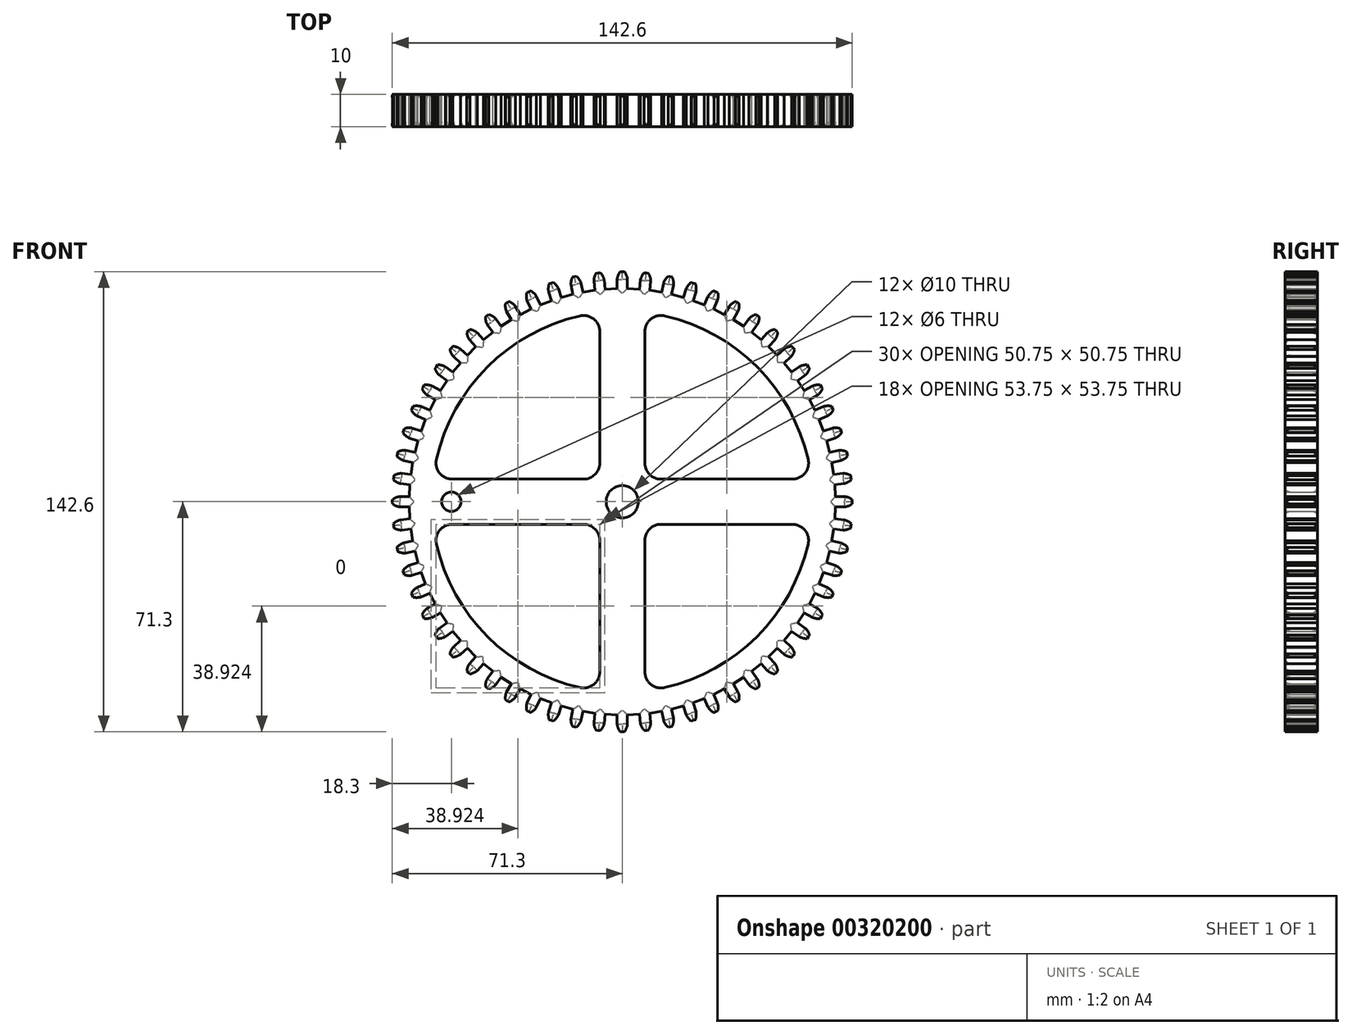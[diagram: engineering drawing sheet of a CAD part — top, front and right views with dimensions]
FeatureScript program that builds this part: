
annotation { "Feature Type Name" : "Feature", "Feature Type Description" : "" }
export const myFeature = defineFeature(function(context is Context, id is Id, definition is map)
    precondition{}
    {
        {
            var Q0;
            Q0=qCreatedBy(makeId("Front.planeOp"),FACE);
            var sketch = newSketch(context, id + "F0", { "sketchPlane" : qUnion([Q0])});
            skCircle(sketch, "E0", {"center": v(0, 0) * mm, "radius": 5 * mm});
            skLineSegment(sketch, "E1", {"start": v(1.6, 66.08) * mm, "end": v(1.6, 68.99) * mm});
            skArc(sketch, "E2", {"start": v(1.6, 67.83) * mm, "mid": v(1.47, 69.66) * mm, "end": v(0.66, 71.3) * mm});
            skLineSegment(sketch, "E3", {"start": v(0, 71.3) * mm, "end": v(0.66, 71.3) * mm});
            skLineSegment(sketch, "E4.MirrorCS", {"start": v(0, 71.3) * mm, "end": v(-0.66, 71.3) * mm});
            skArc(sketch, "E5.MirrorCS", {"start": v(-1.6, 67.83) * mm, "mid": v(-1.47, 69.66) * mm, "end": v(-0.66, 71.3) * mm});
            skLineSegment(sketch, "E6.MirrorCS", {"start": v(-1.6, 66.08) * mm, "end": v(-1.6, 68.99) * mm});
            skLineSegment(sketch, "E7.1.0", {"start": v(-8.5, 65.55) * mm, "end": v(-8.8, 68.44) * mm});
            skArc(sketch, "E7.1.1", {"start": v(-8.68, 67.3) * mm, "mid": v(-8.74, 69.12) * mm, "end": v(-8.1, 70.84) * mm});
            skLineSegment(sketch, "E7.1.2", {"start": v(-7.45, 70.9) * mm, "end": v(-8.1, 70.84) * mm});
            skLineSegment(sketch, "E7.1.3", {"start": v(-7.45, 70.9) * mm, "end": v(-6.8, 70.98) * mm});
            skArc(sketch, "E7.1.4", {"start": v(-5.5, 67.63) * mm, "mid": v(-5.82, 69.43) * mm, "end": v(-6.8, 70.98) * mm});
            skLineSegment(sketch, "E7.1.5", {"start": v(-5.32, 65.89) * mm, "end": v(-5.62, 68.78) * mm});
            skLineSegment(sketch, "E7.2.0", {"start": v(-15.3, 64.3) * mm, "end": v(-15.9, 67.15) * mm});
            skArc(sketch, "E7.2.1", {"start": v(-15.67, 66.02) * mm, "mid": v(-15.92, 67.83) * mm, "end": v(-15.47, 69.6) * mm});
            skLineSegment(sketch, "E7.2.2", {"start": v(-14.82, 69.74) * mm, "end": v(-15.47, 69.6) * mm});
            skLineSegment(sketch, "E7.2.3", {"start": v(-14.82, 69.74) * mm, "end": v(-14.18, 69.88) * mm});
            skArc(sketch, "E7.2.4", {"start": v(-12.54, 66.68) * mm, "mid": v(-13.05, 68.44) * mm, "end": v(-14.18, 69.88) * mm});
            skLineSegment(sketch, "E7.2.5", {"start": v(-12.17, 64.97) * mm, "end": v(-12.78, 67.81) * mm});
            skLineSegment(sketch, "E7.3.0", {"start": v(-21.94, 62.35) * mm, "end": v(-22.84, 65.12) * mm});
            skArc(sketch, "E7.3.1", {"start": v(-22.48, 64.02) * mm, "mid": v(-22.92, 65.8) * mm, "end": v(-22.66, 67.6) * mm});
            skLineSegment(sketch, "E7.3.2", {"start": v(-22.03, 67.81) * mm, "end": v(-22.66, 67.6) * mm});
            skLineSegment(sketch, "E7.3.3", {"start": v(-22.03, 67.81) * mm, "end": v(-21.4, 68.01) * mm});
            skArc(sketch, "E7.3.4", {"start": v(-19.44, 65) * mm, "mid": v(-20.13, 66.7) * mm, "end": v(-21.4, 68.01) * mm});
            skLineSegment(sketch, "E7.3.5", {"start": v(-18.9, 63.34) * mm, "end": v(-19.8, 66.1) * mm});
            skLineSegment(sketch, "E7.4.0", {"start": v(-28.34, 59.72) * mm, "end": v(-29.52, 62.37) * mm});
            skArc(sketch, "E7.4.1", {"start": v(-29.05, 61.32) * mm, "mid": v(-29.67, 63.04) * mm, "end": v(-29.6, 64.87) * mm});
            skLineSegment(sketch, "E7.4.2", {"start": v(-29, 65.14) * mm, "end": v(-29.6, 64.87) * mm});
            skLineSegment(sketch, "E7.4.3", {"start": v(-29, 65.14) * mm, "end": v(-28.4, 65.4) * mm});
            skArc(sketch, "E7.4.4", {"start": v(-26.13, 62.62) * mm, "mid": v(-26.99, 64.23) * mm, "end": v(-28.4, 65.4) * mm});
            skLineSegment(sketch, "E7.4.5", {"start": v(-25.42, 61.02) * mm, "end": v(-26.6, 63.68) * mm});
            skLineSegment(sketch, "E7.5.0", {"start": v(-34.43, 56.43) * mm, "end": v(-35.88, 58.95) * mm});
            skArc(sketch, "E7.5.1", {"start": v(-35.3, 57.94) * mm, "mid": v(-36.1, 59.59) * mm, "end": v(-36.22, 61.42) * mm});
            skLineSegment(sketch, "E7.5.2", {"start": v(-35.65, 61.75) * mm, "end": v(-36.22, 61.42) * mm});
            skLineSegment(sketch, "E7.5.3", {"start": v(-35.65, 61.75) * mm, "end": v(-35.08, 62.07) * mm});
            skArc(sketch, "E7.5.4", {"start": v(-32.53, 59.54) * mm, "mid": v(-33.56, 61.06) * mm, "end": v(-35.08, 62.07) * mm});
            skLineSegment(sketch, "E7.5.5", {"start": v(-31.65, 58.03) * mm, "end": v(-33.1, 60.55) * mm});
            skLineSegment(sketch, "E7.6.0", {"start": v(-40.14, 52.52) * mm, "end": v(-41.85, 54.87) * mm});
            skArc(sketch, "E7.6.1", {"start": v(-41.16, 53.94) * mm, "mid": v(-42.13, 55.49) * mm, "end": v(-42.44, 57.3) * mm});
            skLineSegment(sketch, "E7.6.2", {"start": v(-41.9, 57.68) * mm, "end": v(-42.44, 57.3) * mm});
            skLineSegment(sketch, "E7.6.3", {"start": v(-41.9, 57.68) * mm, "end": v(-41.38, 58.07) * mm});
            skArc(sketch, "E7.6.4", {"start": v(-38.58, 55.82) * mm, "mid": v(-39.75, 57.22) * mm, "end": v(-41.38, 58.07) * mm});
            skLineSegment(sketch, "E7.6.5", {"start": v(-37.55, 54.4) * mm, "end": v(-39.26, 56.75) * mm});
            skLineSegment(sketch, "E7.7.0", {"start": v(-45.4, 48.04) * mm, "end": v(-47.35, 50.2) * mm});
            skArc(sketch, "E7.7.1", {"start": v(-46.58, 49.34) * mm, "mid": v(-47.7, 50.78) * mm, "end": v(-48.2, 52.54) * mm});
            skLineSegment(sketch, "E7.7.2", {"start": v(-47.7, 52.99) * mm, "end": v(-48.2, 52.54) * mm});
            skLineSegment(sketch, "E7.7.3", {"start": v(-47.7, 52.99) * mm, "end": v(-47.22, 53.42) * mm});
            skArc(sketch, "E7.7.4", {"start": v(-44.2, 51.48) * mm, "mid": v(-45.52, 52.75) * mm, "end": v(-47.22, 53.42) * mm});
            skLineSegment(sketch, "E7.7.5", {"start": v(-43.03, 50.18) * mm, "end": v(-44.97, 52.34) * mm});
            skLineSegment(sketch, "E7.8.0", {"start": v(-50.18, 43.03) * mm, "end": v(-52.34, 44.97) * mm});
            skArc(sketch, "E7.8.1", {"start": v(-51.48, 44.2) * mm, "mid": v(-52.75, 45.52) * mm, "end": v(-53.42, 47.22) * mm});
            skLineSegment(sketch, "E7.8.2", {"start": v(-52.99, 47.7) * mm, "end": v(-53.42, 47.22) * mm});
            skLineSegment(sketch, "E7.8.3", {"start": v(-52.99, 47.7) * mm, "end": v(-52.54, 48.2) * mm});
            skArc(sketch, "E7.8.4", {"start": v(-49.34, 46.58) * mm, "mid": v(-50.78, 47.7) * mm, "end": v(-52.54, 48.2) * mm});
            skLineSegment(sketch, "E7.8.5", {"start": v(-48.04, 45.4) * mm, "end": v(-50.2, 47.35) * mm});
            skLineSegment(sketch, "E7.9.0", {"start": v(-54.4, 37.55) * mm, "end": v(-56.75, 39.26) * mm});
            skArc(sketch, "E7.9.1", {"start": v(-55.82, 38.58) * mm, "mid": v(-57.22, 39.75) * mm, "end": v(-58.07, 41.38) * mm});
            skLineSegment(sketch, "E7.9.2", {"start": v(-57.68, 41.9) * mm, "end": v(-58.07, 41.38) * mm});
            skLineSegment(sketch, "E7.9.3", {"start": v(-57.68, 41.9) * mm, "end": v(-57.3, 42.44) * mm});
            skArc(sketch, "E7.9.4", {"start": v(-53.94, 41.16) * mm, "mid": v(-55.49, 42.13) * mm, "end": v(-57.3, 42.44) * mm});
            skLineSegment(sketch, "E7.9.5", {"start": v(-52.52, 40.14) * mm, "end": v(-54.87, 41.85) * mm});
            skLineSegment(sketch, "E7.10.0", {"start": v(-58.03, 31.65) * mm, "end": v(-60.55, 33.1) * mm});
            skArc(sketch, "E7.10.1", {"start": v(-59.54, 32.53) * mm, "mid": v(-61.06, 33.56) * mm, "end": v(-62.07, 35.08) * mm});
            skLineSegment(sketch, "E7.10.2", {"start": v(-61.75, 35.65) * mm, "end": v(-62.07, 35.08) * mm});
            skLineSegment(sketch, "E7.10.3", {"start": v(-61.75, 35.65) * mm, "end": v(-61.42, 36.22) * mm});
            skArc(sketch, "E7.10.4", {"start": v(-57.94, 35.3) * mm, "mid": v(-59.59, 36.1) * mm, "end": v(-61.42, 36.22) * mm});
            skLineSegment(sketch, "E7.10.5", {"start": v(-56.43, 34.43) * mm, "end": v(-58.95, 35.88) * mm});
            skLineSegment(sketch, "E7.11.0", {"start": v(-61.02, 25.42) * mm, "end": v(-63.68, 26.6) * mm});
            skArc(sketch, "E7.11.1", {"start": v(-62.62, 26.13) * mm, "mid": v(-64.23, 26.99) * mm, "end": v(-65.4, 28.4) * mm});
            skLineSegment(sketch, "E7.11.2", {"start": v(-65.14, 29) * mm, "end": v(-65.4, 28.4) * mm});
            skLineSegment(sketch, "E7.11.3", {"start": v(-65.14, 29) * mm, "end": v(-64.87, 29.6) * mm});
            skArc(sketch, "E7.11.4", {"start": v(-61.32, 29.05) * mm, "mid": v(-63.04, 29.67) * mm, "end": v(-64.87, 29.6) * mm});
            skLineSegment(sketch, "E7.11.5", {"start": v(-59.72, 28.34) * mm, "end": v(-62.37, 29.52) * mm});
            skLineSegment(sketch, "E7.12.0", {"start": v(-63.34, 18.9) * mm, "end": v(-66.1, 19.8) * mm});
            skArc(sketch, "E7.12.1", {"start": v(-65, 19.44) * mm, "mid": v(-66.7, 20.13) * mm, "end": v(-68.01, 21.4) * mm});
            skLineSegment(sketch, "E7.12.2", {"start": v(-67.81, 22.03) * mm, "end": v(-68.01, 21.4) * mm});
            skLineSegment(sketch, "E7.12.3", {"start": v(-67.81, 22.03) * mm, "end": v(-67.6, 22.66) * mm});
            skArc(sketch, "E7.12.4", {"start": v(-64.02, 22.48) * mm, "mid": v(-65.8, 22.92) * mm, "end": v(-67.6, 22.66) * mm});
            skLineSegment(sketch, "E7.12.5", {"start": v(-62.35, 21.94) * mm, "end": v(-65.12, 22.84) * mm});
            skLineSegment(sketch, "E7.13.0", {"start": v(-64.97, 12.17) * mm, "end": v(-67.81, 12.78) * mm});
            skArc(sketch, "E7.13.1", {"start": v(-66.68, 12.54) * mm, "mid": v(-68.44, 13.05) * mm, "end": v(-69.88, 14.18) * mm});
            skLineSegment(sketch, "E7.13.2", {"start": v(-69.74, 14.82) * mm, "end": v(-69.88, 14.18) * mm});
            skLineSegment(sketch, "E7.13.3", {"start": v(-69.74, 14.82) * mm, "end": v(-69.6, 15.47) * mm});
            skArc(sketch, "E7.13.4", {"start": v(-66.02, 15.67) * mm, "mid": v(-67.83, 15.92) * mm, "end": v(-69.6, 15.47) * mm});
            skLineSegment(sketch, "E7.13.5", {"start": v(-64.3, 15.3) * mm, "end": v(-67.15, 15.9) * mm});
            skLineSegment(sketch, "E7.14.0", {"start": v(-65.89, 5.32) * mm, "end": v(-68.78, 5.62) * mm});
            skArc(sketch, "E7.14.1", {"start": v(-67.63, 5.5) * mm, "mid": v(-69.43, 5.82) * mm, "end": v(-70.98, 6.8) * mm});
            skLineSegment(sketch, "E7.14.2", {"start": v(-70.9, 7.45) * mm, "end": v(-70.98, 6.8) * mm});
            skLineSegment(sketch, "E7.14.3", {"start": v(-70.9, 7.45) * mm, "end": v(-70.84, 8.1) * mm});
            skArc(sketch, "E7.14.4", {"start": v(-67.3, 8.68) * mm, "mid": v(-69.12, 8.74) * mm, "end": v(-70.84, 8.1) * mm});
            skLineSegment(sketch, "E7.14.5", {"start": v(-65.55, 8.5) * mm, "end": v(-68.44, 8.8) * mm});
            skLineSegment(sketch, "E7.15.0", {"start": v(-66.08, -1.6) * mm, "end": v(-68.99, -1.6) * mm});
            skArc(sketch, "E7.15.1", {"start": v(-67.83, -1.6) * mm, "mid": v(-69.66, -1.47) * mm, "end": v(-71.3, -0.66) * mm});
            skLineSegment(sketch, "E7.15.2", {"start": v(-71.3, 0) * mm, "end": v(-71.3, -0.66) * mm});
            skLineSegment(sketch, "E7.15.3", {"start": v(-71.3, 0) * mm, "end": v(-71.3, 0.66) * mm});
            skArc(sketch, "E7.15.4", {"start": v(-67.83, 1.6) * mm, "mid": v(-69.66, 1.47) * mm, "end": v(-71.3, 0.66) * mm});
            skLineSegment(sketch, "E7.15.5", {"start": v(-66.08, 1.6) * mm, "end": v(-68.99, 1.6) * mm});
            skLineSegment(sketch, "E7.16.0", {"start": v(-65.55, -8.5) * mm, "end": v(-68.44, -8.8) * mm});
            skArc(sketch, "E7.16.1", {"start": v(-67.3, -8.68) * mm, "mid": v(-69.12, -8.74) * mm, "end": v(-70.84, -8.1) * mm});
            skLineSegment(sketch, "E7.16.2", {"start": v(-70.9, -7.45) * mm, "end": v(-70.84, -8.1) * mm});
            skLineSegment(sketch, "E7.16.3", {"start": v(-70.9, -7.45) * mm, "end": v(-70.98, -6.8) * mm});
            skArc(sketch, "E7.16.4", {"start": v(-67.63, -5.5) * mm, "mid": v(-69.43, -5.82) * mm, "end": v(-70.98, -6.8) * mm});
            skLineSegment(sketch, "E7.16.5", {"start": v(-65.89, -5.32) * mm, "end": v(-68.78, -5.62) * mm});
            skLineSegment(sketch, "E7.17.0", {"start": v(-64.3, -15.3) * mm, "end": v(-67.15, -15.9) * mm});
            skArc(sketch, "E7.17.1", {"start": v(-66.02, -15.67) * mm, "mid": v(-67.83, -15.92) * mm, "end": v(-69.6, -15.47) * mm});
            skLineSegment(sketch, "E7.17.2", {"start": v(-69.74, -14.82) * mm, "end": v(-69.6, -15.47) * mm});
            skLineSegment(sketch, "E7.17.3", {"start": v(-69.74, -14.82) * mm, "end": v(-69.88, -14.18) * mm});
            skArc(sketch, "E7.17.4", {"start": v(-66.68, -12.54) * mm, "mid": v(-68.44, -13.05) * mm, "end": v(-69.88, -14.18) * mm});
            skLineSegment(sketch, "E7.17.5", {"start": v(-64.97, -12.17) * mm, "end": v(-67.81, -12.78) * mm});
            skLineSegment(sketch, "E7.18.0", {"start": v(-62.35, -21.94) * mm, "end": v(-65.12, -22.84) * mm});
            skArc(sketch, "E7.18.1", {"start": v(-64.02, -22.48) * mm, "mid": v(-65.8, -22.92) * mm, "end": v(-67.6, -22.66) * mm});
            skLineSegment(sketch, "E7.18.2", {"start": v(-67.81, -22.03) * mm, "end": v(-67.6, -22.66) * mm});
            skLineSegment(sketch, "E7.18.3", {"start": v(-67.81, -22.03) * mm, "end": v(-68.01, -21.4) * mm});
            skArc(sketch, "E7.18.4", {"start": v(-65, -19.44) * mm, "mid": v(-66.7, -20.13) * mm, "end": v(-68.01, -21.4) * mm});
            skLineSegment(sketch, "E7.18.5", {"start": v(-63.34, -18.9) * mm, "end": v(-66.1, -19.8) * mm});
            skLineSegment(sketch, "E7.19.0", {"start": v(-59.72, -28.34) * mm, "end": v(-62.37, -29.52) * mm});
            skArc(sketch, "E7.19.1", {"start": v(-61.32, -29.05) * mm, "mid": v(-63.04, -29.67) * mm, "end": v(-64.87, -29.6) * mm});
            skLineSegment(sketch, "E7.19.2", {"start": v(-65.14, -29) * mm, "end": v(-64.87, -29.6) * mm});
            skLineSegment(sketch, "E7.19.3", {"start": v(-65.14, -29) * mm, "end": v(-65.4, -28.4) * mm});
            skArc(sketch, "E7.19.4", {"start": v(-62.62, -26.13) * mm, "mid": v(-64.23, -26.99) * mm, "end": v(-65.4, -28.4) * mm});
            skLineSegment(sketch, "E7.19.5", {"start": v(-61.02, -25.42) * mm, "end": v(-63.68, -26.6) * mm});
            skLineSegment(sketch, "E7.20.0", {"start": v(-56.43, -34.43) * mm, "end": v(-58.95, -35.88) * mm});
            skArc(sketch, "E7.20.1", {"start": v(-57.94, -35.3) * mm, "mid": v(-59.59, -36.1) * mm, "end": v(-61.42, -36.22) * mm});
            skLineSegment(sketch, "E7.20.2", {"start": v(-61.75, -35.65) * mm, "end": v(-61.42, -36.22) * mm});
            skLineSegment(sketch, "E7.20.3", {"start": v(-61.75, -35.65) * mm, "end": v(-62.07, -35.08) * mm});
            skArc(sketch, "E7.20.4", {"start": v(-59.54, -32.53) * mm, "mid": v(-61.06, -33.56) * mm, "end": v(-62.07, -35.08) * mm});
            skLineSegment(sketch, "E7.20.5", {"start": v(-58.03, -31.65) * mm, "end": v(-60.55, -33.1) * mm});
            skLineSegment(sketch, "E7.21.0", {"start": v(-52.52, -40.14) * mm, "end": v(-54.87, -41.85) * mm});
            skArc(sketch, "E7.21.1", {"start": v(-53.94, -41.16) * mm, "mid": v(-55.49, -42.13) * mm, "end": v(-57.3, -42.44) * mm});
            skLineSegment(sketch, "E7.21.2", {"start": v(-57.68, -41.9) * mm, "end": v(-57.3, -42.44) * mm});
            skLineSegment(sketch, "E7.21.3", {"start": v(-57.68, -41.9) * mm, "end": v(-58.07, -41.38) * mm});
            skArc(sketch, "E7.21.4", {"start": v(-55.82, -38.58) * mm, "mid": v(-57.22, -39.75) * mm, "end": v(-58.07, -41.38) * mm});
            skLineSegment(sketch, "E7.21.5", {"start": v(-54.4, -37.55) * mm, "end": v(-56.75, -39.26) * mm});
            skLineSegment(sketch, "E7.22.0", {"start": v(-48.04, -45.4) * mm, "end": v(-50.2, -47.35) * mm});
            skArc(sketch, "E7.22.1", {"start": v(-49.34, -46.58) * mm, "mid": v(-50.78, -47.7) * mm, "end": v(-52.54, -48.2) * mm});
            skLineSegment(sketch, "E7.22.2", {"start": v(-52.99, -47.7) * mm, "end": v(-52.54, -48.2) * mm});
            skLineSegment(sketch, "E7.22.3", {"start": v(-52.99, -47.7) * mm, "end": v(-53.42, -47.22) * mm});
            skArc(sketch, "E7.22.4", {"start": v(-51.48, -44.2) * mm, "mid": v(-52.75, -45.52) * mm, "end": v(-53.42, -47.22) * mm});
            skLineSegment(sketch, "E7.22.5", {"start": v(-50.18, -43.03) * mm, "end": v(-52.34, -44.97) * mm});
            skLineSegment(sketch, "E7.23.0", {"start": v(-43.03, -50.18) * mm, "end": v(-44.97, -52.34) * mm});
            skArc(sketch, "E7.23.1", {"start": v(-44.2, -51.48) * mm, "mid": v(-45.52, -52.75) * mm, "end": v(-47.22, -53.42) * mm});
            skLineSegment(sketch, "E7.23.2", {"start": v(-47.7, -52.99) * mm, "end": v(-47.22, -53.42) * mm});
            skLineSegment(sketch, "E7.23.3", {"start": v(-47.7, -52.99) * mm, "end": v(-48.2, -52.54) * mm});
            skArc(sketch, "E7.23.4", {"start": v(-46.58, -49.34) * mm, "mid": v(-47.7, -50.78) * mm, "end": v(-48.2, -52.54) * mm});
            skLineSegment(sketch, "E7.23.5", {"start": v(-45.4, -48.04) * mm, "end": v(-47.35, -50.2) * mm});
            skLineSegment(sketch, "E7.24.0", {"start": v(-37.55, -54.4) * mm, "end": v(-39.26, -56.75) * mm});
            skArc(sketch, "E7.24.1", {"start": v(-38.58, -55.82) * mm, "mid": v(-39.75, -57.22) * mm, "end": v(-41.38, -58.07) * mm});
            skLineSegment(sketch, "E7.24.2", {"start": v(-41.9, -57.68) * mm, "end": v(-41.38, -58.07) * mm});
            skLineSegment(sketch, "E7.24.3", {"start": v(-41.9, -57.68) * mm, "end": v(-42.44, -57.3) * mm});
            skArc(sketch, "E7.24.4", {"start": v(-41.16, -53.94) * mm, "mid": v(-42.13, -55.49) * mm, "end": v(-42.44, -57.3) * mm});
            skLineSegment(sketch, "E7.24.5", {"start": v(-40.14, -52.52) * mm, "end": v(-41.85, -54.87) * mm});
            skLineSegment(sketch, "E7.25.0", {"start": v(-31.65, -58.03) * mm, "end": v(-33.1, -60.55) * mm});
            skArc(sketch, "E7.25.1", {"start": v(-32.53, -59.54) * mm, "mid": v(-33.56, -61.06) * mm, "end": v(-35.08, -62.07) * mm});
            skLineSegment(sketch, "E7.25.2", {"start": v(-35.65, -61.75) * mm, "end": v(-35.08, -62.07) * mm});
            skLineSegment(sketch, "E7.25.3", {"start": v(-35.65, -61.75) * mm, "end": v(-36.22, -61.42) * mm});
            skArc(sketch, "E7.25.4", {"start": v(-35.3, -57.94) * mm, "mid": v(-36.1, -59.59) * mm, "end": v(-36.22, -61.42) * mm});
            skLineSegment(sketch, "E7.25.5", {"start": v(-34.43, -56.43) * mm, "end": v(-35.88, -58.95) * mm});
            skLineSegment(sketch, "E7.26.0", {"start": v(-25.42, -61.02) * mm, "end": v(-26.6, -63.68) * mm});
            skArc(sketch, "E7.26.1", {"start": v(-26.13, -62.62) * mm, "mid": v(-26.99, -64.23) * mm, "end": v(-28.4, -65.4) * mm});
            skLineSegment(sketch, "E7.26.2", {"start": v(-29, -65.14) * mm, "end": v(-28.4, -65.4) * mm});
            skLineSegment(sketch, "E7.26.3", {"start": v(-29, -65.14) * mm, "end": v(-29.6, -64.87) * mm});
            skArc(sketch, "E7.26.4", {"start": v(-29.05, -61.32) * mm, "mid": v(-29.67, -63.04) * mm, "end": v(-29.6, -64.87) * mm});
            skLineSegment(sketch, "E7.26.5", {"start": v(-28.34, -59.72) * mm, "end": v(-29.52, -62.37) * mm});
            skLineSegment(sketch, "E7.27.0", {"start": v(-18.9, -63.34) * mm, "end": v(-19.8, -66.1) * mm});
            skArc(sketch, "E7.27.1", {"start": v(-19.44, -65) * mm, "mid": v(-20.13, -66.7) * mm, "end": v(-21.4, -68.01) * mm});
            skLineSegment(sketch, "E7.27.2", {"start": v(-22.03, -67.81) * mm, "end": v(-21.4, -68.01) * mm});
            skLineSegment(sketch, "E7.27.3", {"start": v(-22.03, -67.81) * mm, "end": v(-22.66, -67.6) * mm});
            skArc(sketch, "E7.27.4", {"start": v(-22.48, -64.02) * mm, "mid": v(-22.92, -65.8) * mm, "end": v(-22.66, -67.6) * mm});
            skLineSegment(sketch, "E7.27.5", {"start": v(-21.94, -62.35) * mm, "end": v(-22.84, -65.12) * mm});
            skLineSegment(sketch, "E7.28.0", {"start": v(-12.17, -64.97) * mm, "end": v(-12.78, -67.81) * mm});
            skArc(sketch, "E7.28.1", {"start": v(-12.54, -66.68) * mm, "mid": v(-13.05, -68.44) * mm, "end": v(-14.18, -69.88) * mm});
            skLineSegment(sketch, "E7.28.2", {"start": v(-14.82, -69.74) * mm, "end": v(-14.18, -69.88) * mm});
            skLineSegment(sketch, "E7.28.3", {"start": v(-14.82, -69.74) * mm, "end": v(-15.47, -69.6) * mm});
            skArc(sketch, "E7.28.4", {"start": v(-15.67, -66.02) * mm, "mid": v(-15.92, -67.83) * mm, "end": v(-15.47, -69.6) * mm});
            skLineSegment(sketch, "E7.28.5", {"start": v(-15.3, -64.3) * mm, "end": v(-15.9, -67.15) * mm});
            skLineSegment(sketch, "E7.29.0", {"start": v(-5.32, -65.89) * mm, "end": v(-5.62, -68.78) * mm});
            skArc(sketch, "E7.29.1", {"start": v(-5.5, -67.63) * mm, "mid": v(-5.82, -69.43) * mm, "end": v(-6.8, -70.98) * mm});
            skLineSegment(sketch, "E7.29.2", {"start": v(-7.45, -70.9) * mm, "end": v(-6.8, -70.98) * mm});
            skLineSegment(sketch, "E7.29.3", {"start": v(-7.45, -70.9) * mm, "end": v(-8.1, -70.84) * mm});
            skArc(sketch, "E7.29.4", {"start": v(-8.68, -67.3) * mm, "mid": v(-8.74, -69.12) * mm, "end": v(-8.1, -70.84) * mm});
            skLineSegment(sketch, "E7.29.5", {"start": v(-8.5, -65.55) * mm, "end": v(-8.8, -68.44) * mm});
            skLineSegment(sketch, "E7.30.0", {"start": v(1.6, -66.08) * mm, "end": v(1.6, -68.99) * mm});
            skArc(sketch, "E7.30.1", {"start": v(1.6, -67.83) * mm, "mid": v(1.47, -69.66) * mm, "end": v(0.66, -71.3) * mm});
            skLineSegment(sketch, "E7.30.2", {"start": v(0, -71.3) * mm, "end": v(0.66, -71.3) * mm});
            skLineSegment(sketch, "E7.30.3", {"start": v(0, -71.3) * mm, "end": v(-0.66, -71.3) * mm});
            skArc(sketch, "E7.30.4", {"start": v(-1.6, -67.83) * mm, "mid": v(-1.47, -69.66) * mm, "end": v(-0.66, -71.3) * mm});
            skLineSegment(sketch, "E7.30.5", {"start": v(-1.6, -66.08) * mm, "end": v(-1.6, -68.99) * mm});
            skLineSegment(sketch, "E7.31.0", {"start": v(8.5, -65.55) * mm, "end": v(8.8, -68.44) * mm});
            skArc(sketch, "E7.31.1", {"start": v(8.68, -67.3) * mm, "mid": v(8.74, -69.12) * mm, "end": v(8.1, -70.84) * mm});
            skLineSegment(sketch, "E7.31.2", {"start": v(7.45, -70.9) * mm, "end": v(8.1, -70.84) * mm});
            skLineSegment(sketch, "E7.31.3", {"start": v(7.45, -70.9) * mm, "end": v(6.8, -70.98) * mm});
            skArc(sketch, "E7.31.4", {"start": v(5.5, -67.63) * mm, "mid": v(5.82, -69.43) * mm, "end": v(6.8, -70.98) * mm});
            skLineSegment(sketch, "E7.31.5", {"start": v(5.32, -65.89) * mm, "end": v(5.62, -68.78) * mm});
            skLineSegment(sketch, "E7.32.0", {"start": v(15.3, -64.3) * mm, "end": v(15.9, -67.15) * mm});
            skArc(sketch, "E7.32.1", {"start": v(15.67, -66.02) * mm, "mid": v(15.92, -67.83) * mm, "end": v(15.47, -69.6) * mm});
            skLineSegment(sketch, "E7.32.2", {"start": v(14.82, -69.74) * mm, "end": v(15.47, -69.6) * mm});
            skLineSegment(sketch, "E7.32.3", {"start": v(14.82, -69.74) * mm, "end": v(14.18, -69.88) * mm});
            skArc(sketch, "E7.32.4", {"start": v(12.54, -66.68) * mm, "mid": v(13.05, -68.44) * mm, "end": v(14.18, -69.88) * mm});
            skLineSegment(sketch, "E7.32.5", {"start": v(12.17, -64.97) * mm, "end": v(12.78, -67.81) * mm});
            skLineSegment(sketch, "E7.33.0", {"start": v(21.94, -62.35) * mm, "end": v(22.84, -65.12) * mm});
            skArc(sketch, "E7.33.1", {"start": v(22.48, -64.02) * mm, "mid": v(22.92, -65.8) * mm, "end": v(22.66, -67.6) * mm});
            skLineSegment(sketch, "E7.33.2", {"start": v(22.03, -67.81) * mm, "end": v(22.66, -67.6) * mm});
            skLineSegment(sketch, "E7.33.3", {"start": v(22.03, -67.81) * mm, "end": v(21.4, -68.01) * mm});
            skArc(sketch, "E7.33.4", {"start": v(19.44, -65) * mm, "mid": v(20.13, -66.7) * mm, "end": v(21.4, -68.01) * mm});
            skLineSegment(sketch, "E7.33.5", {"start": v(18.9, -63.34) * mm, "end": v(19.8, -66.1) * mm});
            skLineSegment(sketch, "E7.34.0", {"start": v(28.34, -59.72) * mm, "end": v(29.52, -62.37) * mm});
            skArc(sketch, "E7.34.1", {"start": v(29.05, -61.32) * mm, "mid": v(29.67, -63.04) * mm, "end": v(29.6, -64.87) * mm});
            skLineSegment(sketch, "E7.34.2", {"start": v(29, -65.14) * mm, "end": v(29.6, -64.87) * mm});
            skLineSegment(sketch, "E7.34.3", {"start": v(29, -65.14) * mm, "end": v(28.4, -65.4) * mm});
            skArc(sketch, "E7.34.4", {"start": v(26.13, -62.62) * mm, "mid": v(26.99, -64.23) * mm, "end": v(28.4, -65.4) * mm});
            skLineSegment(sketch, "E7.34.5", {"start": v(25.42, -61.02) * mm, "end": v(26.6, -63.68) * mm});
            skLineSegment(sketch, "E7.35.0", {"start": v(34.43, -56.43) * mm, "end": v(35.88, -58.95) * mm});
            skArc(sketch, "E7.35.1", {"start": v(35.3, -57.94) * mm, "mid": v(36.1, -59.59) * mm, "end": v(36.22, -61.42) * mm});
            skLineSegment(sketch, "E7.35.2", {"start": v(35.65, -61.75) * mm, "end": v(36.22, -61.42) * mm});
            skLineSegment(sketch, "E7.35.3", {"start": v(35.65, -61.75) * mm, "end": v(35.08, -62.07) * mm});
            skArc(sketch, "E7.35.4", {"start": v(32.53, -59.54) * mm, "mid": v(33.56, -61.06) * mm, "end": v(35.08, -62.07) * mm});
            skLineSegment(sketch, "E7.35.5", {"start": v(31.65, -58.03) * mm, "end": v(33.1, -60.55) * mm});
            skLineSegment(sketch, "E7.36.0", {"start": v(40.14, -52.52) * mm, "end": v(41.85, -54.87) * mm});
            skArc(sketch, "E7.36.1", {"start": v(41.16, -53.94) * mm, "mid": v(42.13, -55.49) * mm, "end": v(42.44, -57.3) * mm});
            skLineSegment(sketch, "E7.36.2", {"start": v(41.9, -57.68) * mm, "end": v(42.44, -57.3) * mm});
            skLineSegment(sketch, "E7.36.3", {"start": v(41.9, -57.68) * mm, "end": v(41.38, -58.07) * mm});
            skArc(sketch, "E7.36.4", {"start": v(38.58, -55.82) * mm, "mid": v(39.75, -57.22) * mm, "end": v(41.38, -58.07) * mm});
            skLineSegment(sketch, "E7.36.5", {"start": v(37.55, -54.4) * mm, "end": v(39.26, -56.75) * mm});
            skLineSegment(sketch, "E7.37.0", {"start": v(45.4, -48.04) * mm, "end": v(47.35, -50.2) * mm});
            skArc(sketch, "E7.37.1", {"start": v(46.58, -49.34) * mm, "mid": v(47.7, -50.78) * mm, "end": v(48.2, -52.54) * mm});
            skLineSegment(sketch, "E7.37.2", {"start": v(47.7, -52.99) * mm, "end": v(48.2, -52.54) * mm});
            skLineSegment(sketch, "E7.37.3", {"start": v(47.7, -52.99) * mm, "end": v(47.22, -53.42) * mm});
            skArc(sketch, "E7.37.4", {"start": v(44.2, -51.48) * mm, "mid": v(45.52, -52.75) * mm, "end": v(47.22, -53.42) * mm});
            skLineSegment(sketch, "E7.37.5", {"start": v(43.03, -50.18) * mm, "end": v(44.97, -52.34) * mm});
            skLineSegment(sketch, "E7.38.0", {"start": v(50.18, -43.03) * mm, "end": v(52.34, -44.97) * mm});
            skArc(sketch, "E7.38.1", {"start": v(51.48, -44.2) * mm, "mid": v(52.75, -45.52) * mm, "end": v(53.42, -47.22) * mm});
            skLineSegment(sketch, "E7.38.2", {"start": v(52.99, -47.7) * mm, "end": v(53.42, -47.22) * mm});
            skLineSegment(sketch, "E7.38.3", {"start": v(52.99, -47.7) * mm, "end": v(52.54, -48.2) * mm});
            skArc(sketch, "E7.38.4", {"start": v(49.34, -46.58) * mm, "mid": v(50.78, -47.7) * mm, "end": v(52.54, -48.2) * mm});
            skLineSegment(sketch, "E7.38.5", {"start": v(48.04, -45.4) * mm, "end": v(50.2, -47.35) * mm});
            skLineSegment(sketch, "E7.39.0", {"start": v(54.4, -37.55) * mm, "end": v(56.75, -39.26) * mm});
            skArc(sketch, "E7.39.1", {"start": v(55.82, -38.58) * mm, "mid": v(57.22, -39.75) * mm, "end": v(58.07, -41.38) * mm});
            skLineSegment(sketch, "E7.39.2", {"start": v(57.68, -41.9) * mm, "end": v(58.07, -41.38) * mm});
            skLineSegment(sketch, "E7.39.3", {"start": v(57.68, -41.9) * mm, "end": v(57.3, -42.44) * mm});
            skArc(sketch, "E7.39.4", {"start": v(53.94, -41.16) * mm, "mid": v(55.49, -42.13) * mm, "end": v(57.3, -42.44) * mm});
            skLineSegment(sketch, "E7.39.5", {"start": v(52.52, -40.14) * mm, "end": v(54.87, -41.85) * mm});
            skLineSegment(sketch, "E7.40.0", {"start": v(58.03, -31.65) * mm, "end": v(60.55, -33.1) * mm});
            skArc(sketch, "E7.40.1", {"start": v(59.54, -32.53) * mm, "mid": v(61.06, -33.56) * mm, "end": v(62.07, -35.08) * mm});
            skLineSegment(sketch, "E7.40.2", {"start": v(61.75, -35.65) * mm, "end": v(62.07, -35.08) * mm});
            skLineSegment(sketch, "E7.40.3", {"start": v(61.75, -35.65) * mm, "end": v(61.42, -36.22) * mm});
            skArc(sketch, "E7.40.4", {"start": v(57.94, -35.3) * mm, "mid": v(59.59, -36.1) * mm, "end": v(61.42, -36.22) * mm});
            skLineSegment(sketch, "E7.40.5", {"start": v(56.43, -34.43) * mm, "end": v(58.95, -35.88) * mm});
            skLineSegment(sketch, "E7.41.0", {"start": v(61.02, -25.42) * mm, "end": v(63.68, -26.6) * mm});
            skArc(sketch, "E7.41.1", {"start": v(62.62, -26.13) * mm, "mid": v(64.23, -26.99) * mm, "end": v(65.4, -28.4) * mm});
            skLineSegment(sketch, "E7.41.2", {"start": v(65.14, -29) * mm, "end": v(65.4, -28.4) * mm});
            skLineSegment(sketch, "E7.41.3", {"start": v(65.14, -29) * mm, "end": v(64.87, -29.6) * mm});
            skArc(sketch, "E7.41.4", {"start": v(61.32, -29.05) * mm, "mid": v(63.04, -29.67) * mm, "end": v(64.87, -29.6) * mm});
            skLineSegment(sketch, "E7.41.5", {"start": v(59.72, -28.34) * mm, "end": v(62.37, -29.52) * mm});
            skLineSegment(sketch, "E7.42.0", {"start": v(63.34, -18.9) * mm, "end": v(66.1, -19.8) * mm});
            skArc(sketch, "E7.42.1", {"start": v(65, -19.44) * mm, "mid": v(66.7, -20.13) * mm, "end": v(68.01, -21.4) * mm});
            skLineSegment(sketch, "E7.42.2", {"start": v(67.81, -22.03) * mm, "end": v(68.01, -21.4) * mm});
            skLineSegment(sketch, "E7.42.3", {"start": v(67.81, -22.03) * mm, "end": v(67.6, -22.66) * mm});
            skArc(sketch, "E7.42.4", {"start": v(64.02, -22.48) * mm, "mid": v(65.8, -22.92) * mm, "end": v(67.6, -22.66) * mm});
            skLineSegment(sketch, "E7.42.5", {"start": v(62.35, -21.94) * mm, "end": v(65.12, -22.84) * mm});
            skLineSegment(sketch, "E7.43.0", {"start": v(64.97, -12.17) * mm, "end": v(67.81, -12.78) * mm});
            skArc(sketch, "E7.43.1", {"start": v(66.68, -12.54) * mm, "mid": v(68.44, -13.05) * mm, "end": v(69.88, -14.18) * mm});
            skLineSegment(sketch, "E7.43.2", {"start": v(69.74, -14.82) * mm, "end": v(69.88, -14.18) * mm});
            skLineSegment(sketch, "E7.43.3", {"start": v(69.74, -14.82) * mm, "end": v(69.6, -15.47) * mm});
            skArc(sketch, "E7.43.4", {"start": v(66.02, -15.67) * mm, "mid": v(67.83, -15.92) * mm, "end": v(69.6, -15.47) * mm});
            skLineSegment(sketch, "E7.43.5", {"start": v(64.3, -15.3) * mm, "end": v(67.15, -15.9) * mm});
            skLineSegment(sketch, "E7.44.0", {"start": v(65.89, -5.32) * mm, "end": v(68.78, -5.62) * mm});
            skArc(sketch, "E7.44.1", {"start": v(67.63, -5.5) * mm, "mid": v(69.43, -5.82) * mm, "end": v(70.98, -6.8) * mm});
            skLineSegment(sketch, "E7.44.2", {"start": v(70.9, -7.45) * mm, "end": v(70.98, -6.8) * mm});
            skLineSegment(sketch, "E7.44.3", {"start": v(70.9, -7.45) * mm, "end": v(70.84, -8.1) * mm});
            skArc(sketch, "E7.44.4", {"start": v(67.3, -8.68) * mm, "mid": v(69.12, -8.74) * mm, "end": v(70.84, -8.1) * mm});
            skLineSegment(sketch, "E7.44.5", {"start": v(65.55, -8.5) * mm, "end": v(68.44, -8.8) * mm});
            skLineSegment(sketch, "E7.45.0", {"start": v(66.08, 1.6) * mm, "end": v(68.99, 1.6) * mm});
            skArc(sketch, "E7.45.1", {"start": v(67.83, 1.6) * mm, "mid": v(69.66, 1.47) * mm, "end": v(71.3, 0.66) * mm});
            skLineSegment(sketch, "E7.45.2", {"start": v(71.3, 0) * mm, "end": v(71.3, 0.66) * mm});
            skLineSegment(sketch, "E7.45.3", {"start": v(71.3, 0) * mm, "end": v(71.3, -0.66) * mm});
            skArc(sketch, "E7.45.4", {"start": v(67.83, -1.6) * mm, "mid": v(69.66, -1.47) * mm, "end": v(71.3, -0.66) * mm});
            skLineSegment(sketch, "E7.45.5", {"start": v(66.08, -1.6) * mm, "end": v(68.99, -1.6) * mm});
            skLineSegment(sketch, "E7.46.0", {"start": v(65.55, 8.5) * mm, "end": v(68.44, 8.8) * mm});
            skArc(sketch, "E7.46.1", {"start": v(67.3, 8.68) * mm, "mid": v(69.12, 8.74) * mm, "end": v(70.84, 8.1) * mm});
            skLineSegment(sketch, "E7.46.2", {"start": v(70.9, 7.45) * mm, "end": v(70.84, 8.1) * mm});
            skLineSegment(sketch, "E7.46.3", {"start": v(70.9, 7.45) * mm, "end": v(70.98, 6.8) * mm});
            skArc(sketch, "E7.46.4", {"start": v(67.63, 5.5) * mm, "mid": v(69.43, 5.82) * mm, "end": v(70.98, 6.8) * mm});
            skLineSegment(sketch, "E7.46.5", {"start": v(65.89, 5.32) * mm, "end": v(68.78, 5.62) * mm});
            skLineSegment(sketch, "E7.47.0", {"start": v(64.3, 15.3) * mm, "end": v(67.15, 15.9) * mm});
            skArc(sketch, "E7.47.1", {"start": v(66.02, 15.67) * mm, "mid": v(67.83, 15.92) * mm, "end": v(69.6, 15.47) * mm});
            skLineSegment(sketch, "E7.47.2", {"start": v(69.74, 14.82) * mm, "end": v(69.6, 15.47) * mm});
            skLineSegment(sketch, "E7.47.3", {"start": v(69.74, 14.82) * mm, "end": v(69.88, 14.18) * mm});
            skArc(sketch, "E7.47.4", {"start": v(66.68, 12.54) * mm, "mid": v(68.44, 13.05) * mm, "end": v(69.88, 14.18) * mm});
            skLineSegment(sketch, "E7.47.5", {"start": v(64.97, 12.17) * mm, "end": v(67.81, 12.78) * mm});
            skLineSegment(sketch, "E7.48.0", {"start": v(62.35, 21.94) * mm, "end": v(65.12, 22.84) * mm});
            skArc(sketch, "E7.48.1", {"start": v(64.02, 22.48) * mm, "mid": v(65.8, 22.92) * mm, "end": v(67.6, 22.66) * mm});
            skLineSegment(sketch, "E7.48.2", {"start": v(67.81, 22.03) * mm, "end": v(67.6, 22.66) * mm});
            skLineSegment(sketch, "E7.48.3", {"start": v(67.81, 22.03) * mm, "end": v(68.01, 21.4) * mm});
            skArc(sketch, "E7.48.4", {"start": v(65, 19.44) * mm, "mid": v(66.7, 20.13) * mm, "end": v(68.01, 21.4) * mm});
            skLineSegment(sketch, "E7.48.5", {"start": v(63.34, 18.9) * mm, "end": v(66.1, 19.8) * mm});
            skLineSegment(sketch, "E7.49.0", {"start": v(59.72, 28.34) * mm, "end": v(62.37, 29.52) * mm});
            skArc(sketch, "E7.49.1", {"start": v(61.32, 29.05) * mm, "mid": v(63.04, 29.67) * mm, "end": v(64.87, 29.6) * mm});
            skLineSegment(sketch, "E7.49.2", {"start": v(65.14, 29) * mm, "end": v(64.87, 29.6) * mm});
            skLineSegment(sketch, "E7.49.3", {"start": v(65.14, 29) * mm, "end": v(65.4, 28.4) * mm});
            skArc(sketch, "E7.49.4", {"start": v(62.62, 26.13) * mm, "mid": v(64.23, 26.99) * mm, "end": v(65.4, 28.4) * mm});
            skLineSegment(sketch, "E7.49.5", {"start": v(61.02, 25.42) * mm, "end": v(63.68, 26.6) * mm});
            skLineSegment(sketch, "E7.50.0", {"start": v(56.43, 34.43) * mm, "end": v(58.95, 35.88) * mm});
            skArc(sketch, "E7.50.1", {"start": v(57.94, 35.3) * mm, "mid": v(59.59, 36.1) * mm, "end": v(61.42, 36.22) * mm});
            skLineSegment(sketch, "E7.50.2", {"start": v(61.75, 35.65) * mm, "end": v(61.42, 36.22) * mm});
            skLineSegment(sketch, "E7.50.3", {"start": v(61.75, 35.65) * mm, "end": v(62.07, 35.08) * mm});
            skArc(sketch, "E7.50.4", {"start": v(59.54, 32.53) * mm, "mid": v(61.06, 33.56) * mm, "end": v(62.07, 35.08) * mm});
            skLineSegment(sketch, "E7.50.5", {"start": v(58.03, 31.65) * mm, "end": v(60.55, 33.1) * mm});
            skLineSegment(sketch, "E7.51.0", {"start": v(52.52, 40.14) * mm, "end": v(54.87, 41.85) * mm});
            skArc(sketch, "E7.51.1", {"start": v(53.94, 41.16) * mm, "mid": v(55.49, 42.13) * mm, "end": v(57.3, 42.44) * mm});
            skLineSegment(sketch, "E7.51.2", {"start": v(57.68, 41.9) * mm, "end": v(57.3, 42.44) * mm});
            skLineSegment(sketch, "E7.51.3", {"start": v(57.68, 41.9) * mm, "end": v(58.07, 41.38) * mm});
            skArc(sketch, "E7.51.4", {"start": v(55.82, 38.58) * mm, "mid": v(57.22, 39.75) * mm, "end": v(58.07, 41.38) * mm});
            skLineSegment(sketch, "E7.51.5", {"start": v(54.4, 37.55) * mm, "end": v(56.75, 39.26) * mm});
            skLineSegment(sketch, "E7.52.0", {"start": v(48.04, 45.4) * mm, "end": v(50.2, 47.35) * mm});
            skArc(sketch, "E7.52.1", {"start": v(49.34, 46.58) * mm, "mid": v(50.78, 47.7) * mm, "end": v(52.54, 48.2) * mm});
            skLineSegment(sketch, "E7.52.2", {"start": v(52.99, 47.7) * mm, "end": v(52.54, 48.2) * mm});
            skLineSegment(sketch, "E7.52.3", {"start": v(52.99, 47.7) * mm, "end": v(53.42, 47.22) * mm});
            skArc(sketch, "E7.52.4", {"start": v(51.48, 44.2) * mm, "mid": v(52.75, 45.52) * mm, "end": v(53.42, 47.22) * mm});
            skLineSegment(sketch, "E7.52.5", {"start": v(50.18, 43.03) * mm, "end": v(52.34, 44.97) * mm});
            skLineSegment(sketch, "E7.53.0", {"start": v(43.03, 50.18) * mm, "end": v(44.97, 52.34) * mm});
            skArc(sketch, "E7.53.1", {"start": v(44.2, 51.48) * mm, "mid": v(45.52, 52.75) * mm, "end": v(47.22, 53.42) * mm});
            skLineSegment(sketch, "E7.53.2", {"start": v(47.7, 52.99) * mm, "end": v(47.22, 53.42) * mm});
            skLineSegment(sketch, "E7.53.3", {"start": v(47.7, 52.99) * mm, "end": v(48.2, 52.54) * mm});
            skArc(sketch, "E7.53.4", {"start": v(46.58, 49.34) * mm, "mid": v(47.7, 50.78) * mm, "end": v(48.2, 52.54) * mm});
            skLineSegment(sketch, "E7.53.5", {"start": v(45.4, 48.04) * mm, "end": v(47.35, 50.2) * mm});
            skLineSegment(sketch, "E7.54.0", {"start": v(37.55, 54.4) * mm, "end": v(39.26, 56.75) * mm});
            skArc(sketch, "E7.54.1", {"start": v(38.58, 55.82) * mm, "mid": v(39.75, 57.22) * mm, "end": v(41.38, 58.07) * mm});
            skLineSegment(sketch, "E7.54.2", {"start": v(41.9, 57.68) * mm, "end": v(41.38, 58.07) * mm});
            skLineSegment(sketch, "E7.54.3", {"start": v(41.9, 57.68) * mm, "end": v(42.44, 57.3) * mm});
            skArc(sketch, "E7.54.4", {"start": v(41.16, 53.94) * mm, "mid": v(42.13, 55.49) * mm, "end": v(42.44, 57.3) * mm});
            skLineSegment(sketch, "E7.54.5", {"start": v(40.14, 52.52) * mm, "end": v(41.85, 54.87) * mm});
            skLineSegment(sketch, "E7.55.0", {"start": v(31.65, 58.03) * mm, "end": v(33.1, 60.55) * mm});
            skArc(sketch, "E7.55.1", {"start": v(32.53, 59.54) * mm, "mid": v(33.56, 61.06) * mm, "end": v(35.08, 62.07) * mm});
            skLineSegment(sketch, "E7.55.2", {"start": v(35.65, 61.75) * mm, "end": v(35.08, 62.07) * mm});
            skLineSegment(sketch, "E7.55.3", {"start": v(35.65, 61.75) * mm, "end": v(36.22, 61.42) * mm});
            skArc(sketch, "E7.55.4", {"start": v(35.3, 57.94) * mm, "mid": v(36.1, 59.59) * mm, "end": v(36.22, 61.42) * mm});
            skLineSegment(sketch, "E7.55.5", {"start": v(34.43, 56.43) * mm, "end": v(35.88, 58.95) * mm});
            skLineSegment(sketch, "E7.56.0", {"start": v(25.42, 61.02) * mm, "end": v(26.6, 63.68) * mm});
            skArc(sketch, "E7.56.1", {"start": v(26.13, 62.62) * mm, "mid": v(26.99, 64.23) * mm, "end": v(28.4, 65.4) * mm});
            skLineSegment(sketch, "E7.56.2", {"start": v(29, 65.14) * mm, "end": v(28.4, 65.4) * mm});
            skLineSegment(sketch, "E7.56.3", {"start": v(29, 65.14) * mm, "end": v(29.6, 64.87) * mm});
            skArc(sketch, "E7.56.4", {"start": v(29.05, 61.32) * mm, "mid": v(29.67, 63.04) * mm, "end": v(29.6, 64.87) * mm});
            skLineSegment(sketch, "E7.56.5", {"start": v(28.34, 59.72) * mm, "end": v(29.52, 62.37) * mm});
            skLineSegment(sketch, "E7.57.0", {"start": v(18.9, 63.34) * mm, "end": v(19.8, 66.1) * mm});
            skArc(sketch, "E7.57.1", {"start": v(19.44, 65) * mm, "mid": v(20.13, 66.7) * mm, "end": v(21.4, 68.01) * mm});
            skLineSegment(sketch, "E7.57.2", {"start": v(22.03, 67.81) * mm, "end": v(21.4, 68.01) * mm});
            skLineSegment(sketch, "E7.57.3", {"start": v(22.03, 67.81) * mm, "end": v(22.66, 67.6) * mm});
            skArc(sketch, "E7.57.4", {"start": v(22.48, 64.02) * mm, "mid": v(22.92, 65.8) * mm, "end": v(22.66, 67.6) * mm});
            skLineSegment(sketch, "E7.57.5", {"start": v(21.94, 62.35) * mm, "end": v(22.84, 65.12) * mm});
            skLineSegment(sketch, "E7.58.0", {"start": v(12.17, 64.97) * mm, "end": v(12.78, 67.81) * mm});
            skArc(sketch, "E7.58.1", {"start": v(12.54, 66.68) * mm, "mid": v(13.05, 68.44) * mm, "end": v(14.18, 69.88) * mm});
            skLineSegment(sketch, "E7.58.2", {"start": v(14.82, 69.74) * mm, "end": v(14.18, 69.88) * mm});
            skLineSegment(sketch, "E7.58.3", {"start": v(14.82, 69.74) * mm, "end": v(15.47, 69.6) * mm});
            skArc(sketch, "E7.58.4", {"start": v(15.67, 66.02) * mm, "mid": v(15.92, 67.83) * mm, "end": v(15.47, 69.6) * mm});
            skLineSegment(sketch, "E7.58.5", {"start": v(15.3, 64.3) * mm, "end": v(15.9, 67.15) * mm});
            skLineSegment(sketch, "E7.59.0", {"start": v(5.32, 65.89) * mm, "end": v(5.62, 68.78) * mm});
            skArc(sketch, "E7.59.1", {"start": v(5.5, 67.63) * mm, "mid": v(5.82, 69.43) * mm, "end": v(6.8, 70.98) * mm});
            skLineSegment(sketch, "E7.59.2", {"start": v(7.45, 70.9) * mm, "end": v(6.8, 70.98) * mm});
            skLineSegment(sketch, "E7.59.3", {"start": v(7.45, 70.9) * mm, "end": v(8.1, 70.84) * mm});
            skArc(sketch, "E7.59.4", {"start": v(8.68, 67.3) * mm, "mid": v(8.74, 69.12) * mm, "end": v(8.1, 70.84) * mm});
            skLineSegment(sketch, "E7.59.5", {"start": v(8.5, 65.55) * mm, "end": v(8.8, 68.44) * mm});
            skArc(sketch, "E8", {"start": v(-57.63, 13.1) * mm, "mid": v(-41.8, 41.8) * mm, "end": v(-13.1, 57.63) * mm});
            skLineSegment(sketch, "E9", {"start": v(-52.75, 7) * mm, "end": v(-12, 7) * mm});
            skLineSegment(sketch, "E10", {"start": v(-7, 12) * mm, "end": v(-7, 52.75) * mm});
            skPoint(sketch, "E11.visualSharp", {"position": v(-7, 58.68) * mm});
            skArc(sketch, "E11.filletArc", {"start": v(-7, 52.75) * mm, "mid": v(-8.88, 56.66) * mm, "end": v(-13.1, 57.63) * mm});
            skPoint(sketch, "E12.visualSharp", {"position": v(-58.68, 7) * mm});
            skArc(sketch, "E12.filletArc", {"start": v(-57.63, 13.1) * mm, "mid": v(-56.66, 8.88) * mm, "end": v(-52.75, 7) * mm});
            skPoint(sketch, "E13.visualSharp", {"position": v(-7, 7) * mm});
            skArc(sketch, "E13.filletArc", {"start": v(-12, 7) * mm, "mid": v(-8.46, 8.46) * mm, "end": v(-7, 12) * mm});
            skLineSegment(sketch, "E14.MirrorCS", {"start": v(7, 12) * mm, "end": v(7, 52.75) * mm});
            skArc(sketch, "E15.MirrorCS", {"start": v(7, 52.75) * mm, "mid": v(8.88, 56.66) * mm, "end": v(13.1, 57.63) * mm});
            skArc(sketch, "E16.MirrorCS", {"start": v(57.63, 13.1) * mm, "mid": v(41.8, 41.8) * mm, "end": v(13.1, 57.63) * mm});
            skArc(sketch, "E17.MirrorCS", {"start": v(57.63, 13.1) * mm, "mid": v(56.66, 8.88) * mm, "end": v(52.75, 7) * mm});
            skLineSegment(sketch, "E18.MirrorCS", {"start": v(52.75, 7) * mm, "end": v(12, 7) * mm});
            skArc(sketch, "E19.MirrorCS", {"start": v(12, 7) * mm, "mid": v(8.46, 8.46) * mm, "end": v(7, 12) * mm});
            skArc(sketch, "E20.MirrorCS", {"start": v(12, -7) * mm, "mid": v(8.46, -8.46) * mm, "end": v(7, -12) * mm});
            skLineSegment(sketch, "E21.MirrorCS", {"start": v(7, -12) * mm, "end": v(7, -52.75) * mm});
            skArc(sketch, "E22.MirrorCS", {"start": v(7, -52.75) * mm, "mid": v(8.88, -56.66) * mm, "end": v(13.1, -57.63) * mm});
            skArc(sketch, "E23.MirrorCS", {"start": v(57.63, -13.1) * mm, "mid": v(41.8, -41.8) * mm, "end": v(13.1, -57.63) * mm});
            skArc(sketch, "E24.MirrorCS", {"start": v(57.63, -13.1) * mm, "mid": v(56.66, -8.88) * mm, "end": v(52.75, -7) * mm});
            skLineSegment(sketch, "E25.MirrorCS", {"start": v(52.75, -7) * mm, "end": v(12, -7) * mm});
            skPoint(sketch, "E26.MirrorP", {"position": v(-7, -58.68) * mm});
            skLineSegment(sketch, "E27.MirrorCS", {"start": v(-7, -12) * mm, "end": v(-7, -52.75) * mm});
            skArc(sketch, "E28.MirrorCS", {"start": v(-57.63, -13.1) * mm, "mid": v(-56.66, -8.88) * mm, "end": v(-52.75, -7) * mm});
            skLineSegment(sketch, "E29.MirrorCS", {"start": v(-52.75, -7) * mm, "end": v(-12, -7) * mm});
            skArc(sketch, "E30.MirrorCS", {"start": v(-57.63, -13.1) * mm, "mid": v(-41.8, -41.8) * mm, "end": v(-13.1, -57.63) * mm});
            skArc(sketch, "E31.MirrorCS", {"start": v(-7, -52.75) * mm, "mid": v(-8.88, -56.66) * mm, "end": v(-13.1, -57.63) * mm});
            skArc(sketch, "E32.MirrorCS", {"start": v(-12, -7) * mm, "mid": v(-8.46, -8.46) * mm, "end": v(-7, -12) * mm});
            skLineSegment(sketch, "E33", {"start": v(-5.32, 65.89) * mm, "end": v(-1.6, 66.08) * mm});
            skLineSegment(sketch, "E34.1.0", {"start": v(-12.17, 64.97) * mm, "end": v(-8.5, 65.55) * mm});
            skLineSegment(sketch, "E34.2.0", {"start": v(-18.9, 63.34) * mm, "end": v(-15.3, 64.3) * mm});
            skLineSegment(sketch, "E34.3.0", {"start": v(-25.42, 61.02) * mm, "end": v(-21.94, 62.35) * mm});
            skLineSegment(sketch, "E34.4.0", {"start": v(-31.65, 58.03) * mm, "end": v(-28.34, 59.72) * mm});
            skLineSegment(sketch, "E34.5.0", {"start": v(-37.55, 54.4) * mm, "end": v(-34.43, 56.43) * mm});
            skLineSegment(sketch, "E34.6.0", {"start": v(-43.03, 50.18) * mm, "end": v(-40.14, 52.52) * mm});
            skLineSegment(sketch, "E34.7.0", {"start": v(-48.04, 45.4) * mm, "end": v(-45.4, 48.04) * mm});
            skLineSegment(sketch, "E34.8.0", {"start": v(-52.52, 40.14) * mm, "end": v(-50.18, 43.03) * mm});
            skLineSegment(sketch, "E34.9.0", {"start": v(-56.43, 34.43) * mm, "end": v(-54.4, 37.55) * mm});
            skLineSegment(sketch, "E34.10.0", {"start": v(-59.72, 28.34) * mm, "end": v(-58.03, 31.65) * mm});
            skLineSegment(sketch, "E34.11.0", {"start": v(-62.35, 21.94) * mm, "end": v(-61.02, 25.42) * mm});
            skLineSegment(sketch, "E34.12.0", {"start": v(-64.3, 15.3) * mm, "end": v(-63.34, 18.9) * mm});
            skLineSegment(sketch, "E34.13.0", {"start": v(-65.55, 8.5) * mm, "end": v(-64.97, 12.17) * mm});
            skLineSegment(sketch, "E34.14.0", {"start": v(-66.08, 1.6) * mm, "end": v(-65.89, 5.32) * mm});
            skLineSegment(sketch, "E34.15.0", {"start": v(-65.89, -5.32) * mm, "end": v(-66.08, -1.6) * mm});
            skLineSegment(sketch, "E34.16.0", {"start": v(-64.97, -12.17) * mm, "end": v(-65.55, -8.5) * mm});
            skLineSegment(sketch, "E34.17.0", {"start": v(-63.34, -18.9) * mm, "end": v(-64.3, -15.3) * mm});
            skLineSegment(sketch, "E34.18.0", {"start": v(-61.02, -25.42) * mm, "end": v(-62.35, -21.94) * mm});
            skLineSegment(sketch, "E34.19.0", {"start": v(-58.03, -31.65) * mm, "end": v(-59.72, -28.34) * mm});
            skLineSegment(sketch, "E34.20.0", {"start": v(-54.4, -37.55) * mm, "end": v(-56.43, -34.43) * mm});
            skLineSegment(sketch, "E34.21.0", {"start": v(-50.18, -43.03) * mm, "end": v(-52.52, -40.14) * mm});
            skLineSegment(sketch, "E34.22.0", {"start": v(-45.4, -48.04) * mm, "end": v(-48.04, -45.4) * mm});
            skLineSegment(sketch, "E34.23.0", {"start": v(-40.14, -52.52) * mm, "end": v(-43.03, -50.18) * mm});
            skLineSegment(sketch, "E34.24.0", {"start": v(-34.43, -56.43) * mm, "end": v(-37.55, -54.4) * mm});
            skLineSegment(sketch, "E34.25.0", {"start": v(-28.34, -59.72) * mm, "end": v(-31.65, -58.03) * mm});
            skLineSegment(sketch, "E34.26.0", {"start": v(-21.94, -62.35) * mm, "end": v(-25.42, -61.02) * mm});
            skLineSegment(sketch, "E34.27.0", {"start": v(-15.3, -64.3) * mm, "end": v(-18.9, -63.34) * mm});
            skLineSegment(sketch, "E34.28.0", {"start": v(-8.5, -65.55) * mm, "end": v(-12.17, -64.97) * mm});
            skLineSegment(sketch, "E34.29.0", {"start": v(-1.6, -66.08) * mm, "end": v(-5.32, -65.89) * mm});
            skLineSegment(sketch, "E34.30.0", {"start": v(5.32, -65.89) * mm, "end": v(1.6, -66.08) * mm});
            skLineSegment(sketch, "E34.31.0", {"start": v(12.17, -64.97) * mm, "end": v(8.5, -65.55) * mm});
            skLineSegment(sketch, "E34.32.0", {"start": v(18.9, -63.34) * mm, "end": v(15.3, -64.3) * mm});
            skLineSegment(sketch, "E34.33.0", {"start": v(25.42, -61.02) * mm, "end": v(21.94, -62.35) * mm});
            skLineSegment(sketch, "E34.34.0", {"start": v(31.65, -58.03) * mm, "end": v(28.34, -59.72) * mm});
            skLineSegment(sketch, "E34.35.0", {"start": v(37.55, -54.4) * mm, "end": v(34.43, -56.43) * mm});
            skLineSegment(sketch, "E34.36.0", {"start": v(43.03, -50.18) * mm, "end": v(40.14, -52.52) * mm});
            skLineSegment(sketch, "E34.37.0", {"start": v(48.04, -45.4) * mm, "end": v(45.4, -48.04) * mm});
            skLineSegment(sketch, "E34.38.0", {"start": v(52.52, -40.14) * mm, "end": v(50.18, -43.03) * mm});
            skLineSegment(sketch, "E34.39.0", {"start": v(56.43, -34.43) * mm, "end": v(54.4, -37.55) * mm});
            skLineSegment(sketch, "E34.40.0", {"start": v(59.72, -28.34) * mm, "end": v(58.03, -31.65) * mm});
            skLineSegment(sketch, "E34.41.0", {"start": v(62.35, -21.94) * mm, "end": v(61.02, -25.42) * mm});
            skLineSegment(sketch, "E34.42.0", {"start": v(64.3, -15.3) * mm, "end": v(63.34, -18.9) * mm});
            skLineSegment(sketch, "E34.43.0", {"start": v(65.55, -8.5) * mm, "end": v(64.97, -12.17) * mm});
            skLineSegment(sketch, "E34.44.0", {"start": v(66.08, -1.6) * mm, "end": v(65.89, -5.32) * mm});
            skLineSegment(sketch, "E34.45.0", {"start": v(65.89, 5.32) * mm, "end": v(66.08, 1.6) * mm});
            skLineSegment(sketch, "E34.46.0", {"start": v(64.97, 12.17) * mm, "end": v(65.55, 8.5) * mm});
            skLineSegment(sketch, "E34.47.0", {"start": v(63.34, 18.9) * mm, "end": v(64.3, 15.3) * mm});
            skLineSegment(sketch, "E34.48.0", {"start": v(61.02, 25.42) * mm, "end": v(62.35, 21.94) * mm});
            skLineSegment(sketch, "E34.49.0", {"start": v(58.03, 31.65) * mm, "end": v(59.72, 28.34) * mm});
            skLineSegment(sketch, "E34.50.0", {"start": v(54.4, 37.55) * mm, "end": v(56.43, 34.43) * mm});
            skLineSegment(sketch, "E34.51.0", {"start": v(50.18, 43.03) * mm, "end": v(52.52, 40.14) * mm});
            skLineSegment(sketch, "E34.52.0", {"start": v(45.4, 48.04) * mm, "end": v(48.04, 45.4) * mm});
            skLineSegment(sketch, "E34.53.0", {"start": v(40.14, 52.52) * mm, "end": v(43.03, 50.18) * mm});
            skLineSegment(sketch, "E34.54.0", {"start": v(34.43, 56.43) * mm, "end": v(37.55, 54.4) * mm});
            skLineSegment(sketch, "E34.55.0", {"start": v(28.34, 59.72) * mm, "end": v(31.65, 58.03) * mm});
            skLineSegment(sketch, "E34.56.0", {"start": v(21.94, 62.35) * mm, "end": v(25.42, 61.02) * mm});
            skLineSegment(sketch, "E34.57.0", {"start": v(15.3, 64.3) * mm, "end": v(18.9, 63.34) * mm});
            skLineSegment(sketch, "E34.58.0", {"start": v(8.5, 65.55) * mm, "end": v(12.17, 64.97) * mm});
            skLineSegment(sketch, "E34.59.0", {"start": v(1.6, 66.08) * mm, "end": v(5.32, 65.89) * mm});
            skCircle(sketch, "E35", {"center": v(-53, 0) * mm, "radius": 3 * mm});
            skSolve(sketch);
        }
        {
            var Q0;
            Q0=makeQuery(id+"F0.imprint","IMPRINT",FACE,{"disambiguationData":[TD([[makeQuery(id+"F0.imprint","IMPRINT",EDGE,{"derivedFrom":sQuery(id+"F0.wireOp",EDGE,"E0")}),-1.0]])]});
            extrude(context, id + "F1", {"entities" : qUnion([Q0]), "endBound" : BoundingType.SYMMETRIC, "depth" : 10 * mm});
        }
        {
            var Q0;
            Q0=makeQuery(id+"F1.opExtrude","SWEPT_BODY",BODY,{"disambiguationData":[OSD([sQuery(id+"F0.wireOp",EDGE,"E0"),sQuery(id+"F0.wireOp",EDGE,"E1"),sQuery(id+"F0.wireOp",EDGE,"E2"),sQuery(id+"F0.wireOp",EDGE,"E3"),sQuery(id+"F0.wireOp",EDGE,"E4.MirrorCS"),sQuery(id+"F0.wireOp",EDGE,"E5.MirrorCS"),sQuery(id+"F0.wireOp",EDGE,"E6.MirrorCS"),sQuery(id+"F0.wireOp",EDGE,"E7.1.0"),sQuery(id+"F0.wireOp",EDGE,"E7.1.1"),sQuery(id+"F0.wireOp",EDGE,"E7.1.2"),sQuery(id+"F0.wireOp",EDGE,"E7.1.3"),sQuery(id+"F0.wireOp",EDGE,"E7.1.4"),sQuery(id+"F0.wireOp",EDGE,"E7.1.5"),sQuery(id+"F0.wireOp",EDGE,"E7.2.0"),sQuery(id+"F0.wireOp",EDGE,"E7.2.1"),sQuery(id+"F0.wireOp",EDGE,"E7.2.2"),sQuery(id+"F0.wireOp",EDGE,"E7.2.3"),sQuery(id+"F0.wireOp",EDGE,"E7.2.4"),sQuery(id+"F0.wireOp",EDGE,"E7.2.5"),sQuery(id+"F0.wireOp",EDGE,"E7.3.0"),sQuery(id+"F0.wireOp",EDGE,"E7.3.1"),sQuery(id+"F0.wireOp",EDGE,"E7.3.2"),sQuery(id+"F0.wireOp",EDGE,"E7.3.3"),sQuery(id+"F0.wireOp",EDGE,"E7.3.4"),sQuery(id+"F0.wireOp",EDGE,"E7.3.5"),sQuery(id+"F0.wireOp",EDGE,"E7.4.0"),sQuery(id+"F0.wireOp",EDGE,"E7.4.1"),sQuery(id+"F0.wireOp",EDGE,"E7.4.2"),sQuery(id+"F0.wireOp",EDGE,"E7.4.3"),sQuery(id+"F0.wireOp",EDGE,"E7.4.4"),sQuery(id+"F0.wireOp",EDGE,"E7.4.5"),sQuery(id+"F0.wireOp",EDGE,"E7.5.0"),sQuery(id+"F0.wireOp",EDGE,"E7.5.1"),sQuery(id+"F0.wireOp",EDGE,"E7.5.2"),sQuery(id+"F0.wireOp",EDGE,"E7.5.3"),sQuery(id+"F0.wireOp",EDGE,"E7.5.4"),sQuery(id+"F0.wireOp",EDGE,"E7.5.5"),sQuery(id+"F0.wireOp",EDGE,"E7.6.0"),sQuery(id+"F0.wireOp",EDGE,"E7.6.1"),sQuery(id+"F0.wireOp",EDGE,"E7.6.2"),sQuery(id+"F0.wireOp",EDGE,"E7.6.3"),sQuery(id+"F0.wireOp",EDGE,"E7.6.4"),sQuery(id+"F0.wireOp",EDGE,"E7.6.5"),sQuery(id+"F0.wireOp",EDGE,"E7.7.0"),sQuery(id+"F0.wireOp",EDGE,"E7.7.1"),sQuery(id+"F0.wireOp",EDGE,"E7.7.2"),sQuery(id+"F0.wireOp",EDGE,"E7.7.3"),sQuery(id+"F0.wireOp",EDGE,"E7.7.4"),sQuery(id+"F0.wireOp",EDGE,"E7.7.5"),sQuery(id+"F0.wireOp",EDGE,"E7.8.0"),sQuery(id+"F0.wireOp",EDGE,"E7.8.1"),sQuery(id+"F0.wireOp",EDGE,"E7.8.2"),sQuery(id+"F0.wireOp",EDGE,"E7.8.3"),sQuery(id+"F0.wireOp",EDGE,"E7.8.4"),sQuery(id+"F0.wireOp",EDGE,"E7.8.5"),sQuery(id+"F0.wireOp",EDGE,"E7.9.0"),sQuery(id+"F0.wireOp",EDGE,"E7.9.1"),sQuery(id+"F0.wireOp",EDGE,"E7.9.2"),sQuery(id+"F0.wireOp",EDGE,"E7.9.3"),sQuery(id+"F0.wireOp",EDGE,"E7.9.4"),sQuery(id+"F0.wireOp",EDGE,"E7.9.5"),sQuery(id+"F0.wireOp",EDGE,"E7.10.0"),sQuery(id+"F0.wireOp",EDGE,"E7.10.1"),sQuery(id+"F0.wireOp",EDGE,"E7.10.2"),sQuery(id+"F0.wireOp",EDGE,"E7.10.3"),sQuery(id+"F0.wireOp",EDGE,"E7.10.4"),sQuery(id+"F0.wireOp",EDGE,"E7.10.5"),sQuery(id+"F0.wireOp",EDGE,"E7.11.0"),sQuery(id+"F0.wireOp",EDGE,"E7.11.1"),sQuery(id+"F0.wireOp",EDGE,"E7.11.2"),sQuery(id+"F0.wireOp",EDGE,"E7.11.3"),sQuery(id+"F0.wireOp",EDGE,"E7.11.4"),sQuery(id+"F0.wireOp",EDGE,"E7.11.5"),sQuery(id+"F0.wireOp",EDGE,"E7.12.0"),sQuery(id+"F0.wireOp",EDGE,"E7.12.1"),sQuery(id+"F0.wireOp",EDGE,"E7.12.2"),sQuery(id+"F0.wireOp",EDGE,"E7.12.3"),sQuery(id+"F0.wireOp",EDGE,"E7.12.4"),sQuery(id+"F0.wireOp",EDGE,"E7.12.5"),sQuery(id+"F0.wireOp",EDGE,"E7.13.0"),sQuery(id+"F0.wireOp",EDGE,"E7.13.1"),sQuery(id+"F0.wireOp",EDGE,"E7.13.2"),sQuery(id+"F0.wireOp",EDGE,"E7.13.3"),sQuery(id+"F0.wireOp",EDGE,"E7.13.4"),sQuery(id+"F0.wireOp",EDGE,"E7.13.5"),sQuery(id+"F0.wireOp",EDGE,"E7.14.0"),sQuery(id+"F0.wireOp",EDGE,"E7.14.1"),sQuery(id+"F0.wireOp",EDGE,"E7.14.2"),sQuery(id+"F0.wireOp",EDGE,"E7.14.3"),sQuery(id+"F0.wireOp",EDGE,"E7.14.4"),sQuery(id+"F0.wireOp",EDGE,"E7.14.5"),sQuery(id+"F0.wireOp",EDGE,"E7.15.0"),sQuery(id+"F0.wireOp",EDGE,"E7.15.1"),sQuery(id+"F0.wireOp",EDGE,"E7.15.2"),sQuery(id+"F0.wireOp",EDGE,"E7.15.3"),sQuery(id+"F0.wireOp",EDGE,"E7.15.4"),sQuery(id+"F0.wireOp",EDGE,"E7.15.5"),sQuery(id+"F0.wireOp",EDGE,"E7.16.0"),sQuery(id+"F0.wireOp",EDGE,"E7.16.1"),sQuery(id+"F0.wireOp",EDGE,"E7.16.2"),sQuery(id+"F0.wireOp",EDGE,"E7.16.3"),sQuery(id+"F0.wireOp",EDGE,"E7.16.4"),sQuery(id+"F0.wireOp",EDGE,"E7.16.5"),sQuery(id+"F0.wireOp",EDGE,"E7.17.0"),sQuery(id+"F0.wireOp",EDGE,"E7.17.1"),sQuery(id+"F0.wireOp",EDGE,"E7.17.2"),sQuery(id+"F0.wireOp",EDGE,"E7.17.3"),sQuery(id+"F0.wireOp",EDGE,"E7.17.4"),sQuery(id+"F0.wireOp",EDGE,"E7.17.5"),sQuery(id+"F0.wireOp",EDGE,"E7.18.0"),sQuery(id+"F0.wireOp",EDGE,"E7.18.1"),sQuery(id+"F0.wireOp",EDGE,"E7.18.2"),sQuery(id+"F0.wireOp",EDGE,"E7.18.3"),sQuery(id+"F0.wireOp",EDGE,"E7.18.4"),sQuery(id+"F0.wireOp",EDGE,"E7.18.5"),sQuery(id+"F0.wireOp",EDGE,"E7.19.0"),sQuery(id+"F0.wireOp",EDGE,"E7.19.1"),sQuery(id+"F0.wireOp",EDGE,"E7.19.2"),sQuery(id+"F0.wireOp",EDGE,"E7.19.3"),sQuery(id+"F0.wireOp",EDGE,"E7.19.4"),sQuery(id+"F0.wireOp",EDGE,"E7.19.5"),sQuery(id+"F0.wireOp",EDGE,"E7.20.0"),sQuery(id+"F0.wireOp",EDGE,"E7.20.1"),sQuery(id+"F0.wireOp",EDGE,"E7.20.2"),sQuery(id+"F0.wireOp",EDGE,"E7.20.3"),sQuery(id+"F0.wireOp",EDGE,"E7.20.4"),sQuery(id+"F0.wireOp",EDGE,"E7.20.5"),sQuery(id+"F0.wireOp",EDGE,"E7.21.0"),sQuery(id+"F0.wireOp",EDGE,"E7.21.1"),sQuery(id+"F0.wireOp",EDGE,"E7.21.2"),sQuery(id+"F0.wireOp",EDGE,"E7.21.3"),sQuery(id+"F0.wireOp",EDGE,"E7.21.4"),sQuery(id+"F0.wireOp",EDGE,"E7.21.5"),sQuery(id+"F0.wireOp",EDGE,"E7.22.0"),sQuery(id+"F0.wireOp",EDGE,"E7.22.1"),sQuery(id+"F0.wireOp",EDGE,"E7.22.2"),sQuery(id+"F0.wireOp",EDGE,"E7.22.3"),sQuery(id+"F0.wireOp",EDGE,"E7.22.4"),sQuery(id+"F0.wireOp",EDGE,"E7.22.5"),sQuery(id+"F0.wireOp",EDGE,"E7.23.0"),sQuery(id+"F0.wireOp",EDGE,"E7.23.1"),sQuery(id+"F0.wireOp",EDGE,"E7.23.2"),sQuery(id+"F0.wireOp",EDGE,"E7.23.3"),sQuery(id+"F0.wireOp",EDGE,"E7.23.4"),sQuery(id+"F0.wireOp",EDGE,"E7.23.5"),sQuery(id+"F0.wireOp",EDGE,"E7.24.0"),sQuery(id+"F0.wireOp",EDGE,"E7.24.1"),sQuery(id+"F0.wireOp",EDGE,"E7.24.2"),sQuery(id+"F0.wireOp",EDGE,"E7.24.3"),sQuery(id+"F0.wireOp",EDGE,"E7.24.4"),sQuery(id+"F0.wireOp",EDGE,"E7.24.5"),sQuery(id+"F0.wireOp",EDGE,"E7.25.0"),sQuery(id+"F0.wireOp",EDGE,"E7.25.1"),sQuery(id+"F0.wireOp",EDGE,"E7.25.2"),sQuery(id+"F0.wireOp",EDGE,"E7.25.3"),sQuery(id+"F0.wireOp",EDGE,"E7.25.4"),sQuery(id+"F0.wireOp",EDGE,"E7.25.5"),sQuery(id+"F0.wireOp",EDGE,"E7.26.0"),sQuery(id+"F0.wireOp",EDGE,"E7.26.1"),sQuery(id+"F0.wireOp",EDGE,"E7.26.2"),sQuery(id+"F0.wireOp",EDGE,"E7.26.3"),sQuery(id+"F0.wireOp",EDGE,"E7.26.4"),sQuery(id+"F0.wireOp",EDGE,"E7.26.5"),sQuery(id+"F0.wireOp",EDGE,"E7.27.0"),sQuery(id+"F0.wireOp",EDGE,"E7.27.1"),sQuery(id+"F0.wireOp",EDGE,"E7.27.2"),sQuery(id+"F0.wireOp",EDGE,"E7.27.3"),sQuery(id+"F0.wireOp",EDGE,"E7.27.4"),sQuery(id+"F0.wireOp",EDGE,"E7.27.5"),sQuery(id+"F0.wireOp",EDGE,"E7.28.0"),sQuery(id+"F0.wireOp",EDGE,"E7.28.1"),sQuery(id+"F0.wireOp",EDGE,"E7.28.2"),sQuery(id+"F0.wireOp",EDGE,"E7.28.3"),sQuery(id+"F0.wireOp",EDGE,"E7.28.4"),sQuery(id+"F0.wireOp",EDGE,"E7.28.5"),sQuery(id+"F0.wireOp",EDGE,"E7.29.0"),sQuery(id+"F0.wireOp",EDGE,"E7.29.1"),sQuery(id+"F0.wireOp",EDGE,"E7.29.2"),sQuery(id+"F0.wireOp",EDGE,"E7.29.3"),sQuery(id+"F0.wireOp",EDGE,"E7.29.4"),sQuery(id+"F0.wireOp",EDGE,"E7.29.5"),sQuery(id+"F0.wireOp",EDGE,"E7.30.0"),sQuery(id+"F0.wireOp",EDGE,"E7.30.1"),sQuery(id+"F0.wireOp",EDGE,"E7.30.2"),sQuery(id+"F0.wireOp",EDGE,"E7.30.3"),sQuery(id+"F0.wireOp",EDGE,"E7.30.4"),sQuery(id+"F0.wireOp",EDGE,"E7.30.5"),sQuery(id+"F0.wireOp",EDGE,"E7.31.0"),sQuery(id+"F0.wireOp",EDGE,"E7.31.1"),sQuery(id+"F0.wireOp",EDGE,"E7.31.2"),sQuery(id+"F0.wireOp",EDGE,"E7.31.3"),sQuery(id+"F0.wireOp",EDGE,"E7.31.4"),sQuery(id+"F0.wireOp",EDGE,"E7.31.5"),sQuery(id+"F0.wireOp",EDGE,"E7.32.0"),sQuery(id+"F0.wireOp",EDGE,"E7.32.1"),sQuery(id+"F0.wireOp",EDGE,"E7.32.2"),sQuery(id+"F0.wireOp",EDGE,"E7.32.3"),sQuery(id+"F0.wireOp",EDGE,"E7.32.4"),sQuery(id+"F0.wireOp",EDGE,"E7.32.5"),sQuery(id+"F0.wireOp",EDGE,"E7.33.0"),sQuery(id+"F0.wireOp",EDGE,"E7.33.1"),sQuery(id+"F0.wireOp",EDGE,"E7.33.2"),sQuery(id+"F0.wireOp",EDGE,"E7.33.3"),sQuery(id+"F0.wireOp",EDGE,"E7.33.4"),sQuery(id+"F0.wireOp",EDGE,"E7.33.5"),sQuery(id+"F0.wireOp",EDGE,"E7.34.0"),sQuery(id+"F0.wireOp",EDGE,"E7.34.1"),sQuery(id+"F0.wireOp",EDGE,"E7.34.2"),sQuery(id+"F0.wireOp",EDGE,"E7.34.3"),sQuery(id+"F0.wireOp",EDGE,"E7.34.4"),sQuery(id+"F0.wireOp",EDGE,"E7.34.5"),sQuery(id+"F0.wireOp",EDGE,"E7.35.0"),sQuery(id+"F0.wireOp",EDGE,"E7.35.1"),sQuery(id+"F0.wireOp",EDGE,"E7.35.2"),sQuery(id+"F0.wireOp",EDGE,"E7.35.3"),sQuery(id+"F0.wireOp",EDGE,"E7.35.4"),sQuery(id+"F0.wireOp",EDGE,"E7.35.5"),sQuery(id+"F0.wireOp",EDGE,"E7.36.0"),sQuery(id+"F0.wireOp",EDGE,"E7.36.1"),sQuery(id+"F0.wireOp",EDGE,"E7.36.2"),sQuery(id+"F0.wireOp",EDGE,"E7.36.3"),sQuery(id+"F0.wireOp",EDGE,"E7.36.4"),sQuery(id+"F0.wireOp",EDGE,"E7.36.5"),sQuery(id+"F0.wireOp",EDGE,"E7.37.0"),sQuery(id+"F0.wireOp",EDGE,"E7.37.1"),sQuery(id+"F0.wireOp",EDGE,"E7.37.2"),sQuery(id+"F0.wireOp",EDGE,"E7.37.3"),sQuery(id+"F0.wireOp",EDGE,"E7.37.4"),sQuery(id+"F0.wireOp",EDGE,"E7.37.5"),sQuery(id+"F0.wireOp",EDGE,"E7.38.0"),sQuery(id+"F0.wireOp",EDGE,"E7.38.1"),sQuery(id+"F0.wireOp",EDGE,"E7.38.2"),sQuery(id+"F0.wireOp",EDGE,"E7.38.3"),sQuery(id+"F0.wireOp",EDGE,"E7.38.4"),sQuery(id+"F0.wireOp",EDGE,"E7.38.5"),sQuery(id+"F0.wireOp",EDGE,"E7.39.0"),sQuery(id+"F0.wireOp",EDGE,"E7.39.1"),sQuery(id+"F0.wireOp",EDGE,"E7.39.2"),sQuery(id+"F0.wireOp",EDGE,"E7.39.3"),sQuery(id+"F0.wireOp",EDGE,"E7.39.4"),sQuery(id+"F0.wireOp",EDGE,"E7.39.5"),sQuery(id+"F0.wireOp",EDGE,"E7.40.0"),sQuery(id+"F0.wireOp",EDGE,"E7.40.1"),sQuery(id+"F0.wireOp",EDGE,"E7.40.2"),sQuery(id+"F0.wireOp",EDGE,"E7.40.3"),sQuery(id+"F0.wireOp",EDGE,"E7.40.4"),sQuery(id+"F0.wireOp",EDGE,"E7.40.5"),sQuery(id+"F0.wireOp",EDGE,"E7.41.0"),sQuery(id+"F0.wireOp",EDGE,"E7.41.1"),sQuery(id+"F0.wireOp",EDGE,"E7.41.2"),sQuery(id+"F0.wireOp",EDGE,"E7.41.3"),sQuery(id+"F0.wireOp",EDGE,"E7.41.4"),sQuery(id+"F0.wireOp",EDGE,"E7.41.5"),sQuery(id+"F0.wireOp",EDGE,"E7.42.0"),sQuery(id+"F0.wireOp",EDGE,"E7.42.1"),sQuery(id+"F0.wireOp",EDGE,"E7.42.2"),sQuery(id+"F0.wireOp",EDGE,"E7.42.3"),sQuery(id+"F0.wireOp",EDGE,"E7.42.4"),sQuery(id+"F0.wireOp",EDGE,"E7.42.5"),sQuery(id+"F0.wireOp",EDGE,"E7.43.0"),sQuery(id+"F0.wireOp",EDGE,"E7.43.1"),sQuery(id+"F0.wireOp",EDGE,"E7.43.2"),sQuery(id+"F0.wireOp",EDGE,"E7.43.3"),sQuery(id+"F0.wireOp",EDGE,"E7.43.4"),sQuery(id+"F0.wireOp",EDGE,"E7.43.5"),sQuery(id+"F0.wireOp",EDGE,"E7.44.0"),sQuery(id+"F0.wireOp",EDGE,"E7.44.1"),sQuery(id+"F0.wireOp",EDGE,"E7.44.2"),sQuery(id+"F0.wireOp",EDGE,"E7.44.3"),sQuery(id+"F0.wireOp",EDGE,"E7.44.4"),sQuery(id+"F0.wireOp",EDGE,"E7.44.5"),sQuery(id+"F0.wireOp",EDGE,"E7.45.0"),sQuery(id+"F0.wireOp",EDGE,"E7.45.1"),sQuery(id+"F0.wireOp",EDGE,"E7.45.2"),sQuery(id+"F0.wireOp",EDGE,"E7.45.3"),sQuery(id+"F0.wireOp",EDGE,"E7.45.4"),sQuery(id+"F0.wireOp",EDGE,"E7.45.5"),sQuery(id+"F0.wireOp",EDGE,"E7.46.0"),sQuery(id+"F0.wireOp",EDGE,"E7.46.1"),sQuery(id+"F0.wireOp",EDGE,"E7.46.2"),sQuery(id+"F0.wireOp",EDGE,"E7.46.3"),sQuery(id+"F0.wireOp",EDGE,"E7.46.4"),sQuery(id+"F0.wireOp",EDGE,"E7.46.5"),sQuery(id+"F0.wireOp",EDGE,"E7.47.0"),sQuery(id+"F0.wireOp",EDGE,"E7.47.1"),sQuery(id+"F0.wireOp",EDGE,"E7.47.2"),sQuery(id+"F0.wireOp",EDGE,"E7.47.3"),sQuery(id+"F0.wireOp",EDGE,"E7.47.4"),sQuery(id+"F0.wireOp",EDGE,"E7.47.5"),sQuery(id+"F0.wireOp",EDGE,"E7.48.0"),sQuery(id+"F0.wireOp",EDGE,"E7.48.1"),sQuery(id+"F0.wireOp",EDGE,"E7.48.2"),sQuery(id+"F0.wireOp",EDGE,"E7.48.3"),sQuery(id+"F0.wireOp",EDGE,"E7.48.4"),sQuery(id+"F0.wireOp",EDGE,"E7.48.5"),sQuery(id+"F0.wireOp",EDGE,"E7.49.0"),sQuery(id+"F0.wireOp",EDGE,"E7.49.1"),sQuery(id+"F0.wireOp",EDGE,"E7.49.2"),sQuery(id+"F0.wireOp",EDGE,"E7.49.3"),sQuery(id+"F0.wireOp",EDGE,"E7.49.4"),sQuery(id+"F0.wireOp",EDGE,"E7.49.5"),sQuery(id+"F0.wireOp",EDGE,"E7.50.0"),sQuery(id+"F0.wireOp",EDGE,"E7.50.1"),sQuery(id+"F0.wireOp",EDGE,"E7.50.2"),sQuery(id+"F0.wireOp",EDGE,"E7.50.3"),sQuery(id+"F0.wireOp",EDGE,"E7.50.4"),sQuery(id+"F0.wireOp",EDGE,"E7.50.5"),sQuery(id+"F0.wireOp",EDGE,"E7.51.0"),sQuery(id+"F0.wireOp",EDGE,"E7.51.1"),sQuery(id+"F0.wireOp",EDGE,"E7.51.2"),sQuery(id+"F0.wireOp",EDGE,"E7.51.3"),sQuery(id+"F0.wireOp",EDGE,"E7.51.4"),sQuery(id+"F0.wireOp",EDGE,"E7.51.5"),sQuery(id+"F0.wireOp",EDGE,"E7.52.0"),sQuery(id+"F0.wireOp",EDGE,"E7.52.1"),sQuery(id+"F0.wireOp",EDGE,"E7.52.2"),sQuery(id+"F0.wireOp",EDGE,"E7.52.3"),sQuery(id+"F0.wireOp",EDGE,"E7.52.4"),sQuery(id+"F0.wireOp",EDGE,"E7.52.5"),sQuery(id+"F0.wireOp",EDGE,"E7.53.0"),sQuery(id+"F0.wireOp",EDGE,"E7.53.1"),sQuery(id+"F0.wireOp",EDGE,"E7.53.2"),sQuery(id+"F0.wireOp",EDGE,"E7.53.3"),sQuery(id+"F0.wireOp",EDGE,"E7.53.4"),sQuery(id+"F0.wireOp",EDGE,"E7.53.5"),sQuery(id+"F0.wireOp",EDGE,"E7.54.0"),sQuery(id+"F0.wireOp",EDGE,"E7.54.1"),sQuery(id+"F0.wireOp",EDGE,"E7.54.2"),sQuery(id+"F0.wireOp",EDGE,"E7.54.3"),sQuery(id+"F0.wireOp",EDGE,"E7.54.4"),sQuery(id+"F0.wireOp",EDGE,"E7.54.5"),sQuery(id+"F0.wireOp",EDGE,"E7.55.0"),sQuery(id+"F0.wireOp",EDGE,"E7.55.1"),sQuery(id+"F0.wireOp",EDGE,"E7.55.2"),sQuery(id+"F0.wireOp",EDGE,"E7.55.3"),sQuery(id+"F0.wireOp",EDGE,"E7.55.4"),sQuery(id+"F0.wireOp",EDGE,"E7.55.5"),sQuery(id+"F0.wireOp",EDGE,"E7.56.0"),sQuery(id+"F0.wireOp",EDGE,"E7.56.1"),sQuery(id+"F0.wireOp",EDGE,"E7.56.2"),sQuery(id+"F0.wireOp",EDGE,"E7.56.3"),sQuery(id+"F0.wireOp",EDGE,"E7.56.4"),sQuery(id+"F0.wireOp",EDGE,"E7.56.5"),sQuery(id+"F0.wireOp",EDGE,"E7.57.0"),sQuery(id+"F0.wireOp",EDGE,"E7.57.1"),sQuery(id+"F0.wireOp",EDGE,"E7.57.2"),sQuery(id+"F0.wireOp",EDGE,"E7.57.3"),sQuery(id+"F0.wireOp",EDGE,"E7.57.4"),sQuery(id+"F0.wireOp",EDGE,"E7.57.5"),sQuery(id+"F0.wireOp",EDGE,"E7.58.0"),sQuery(id+"F0.wireOp",EDGE,"E7.58.1"),sQuery(id+"F0.wireOp",EDGE,"E7.58.2"),sQuery(id+"F0.wireOp",EDGE,"E7.58.3"),sQuery(id+"F0.wireOp",EDGE,"E7.58.4"),sQuery(id+"F0.wireOp",EDGE,"E7.58.5"),sQuery(id+"F0.wireOp",EDGE,"E7.59.0"),sQuery(id+"F0.wireOp",EDGE,"E7.59.1"),sQuery(id+"F0.wireOp",EDGE,"E7.59.2"),sQuery(id+"F0.wireOp",EDGE,"E7.59.3"),sQuery(id+"F0.wireOp",EDGE,"E7.59.4"),sQuery(id+"F0.wireOp",EDGE,"E7.59.5"),sQuery(id+"F0.wireOp",EDGE,"E8"),sQuery(id+"F0.wireOp",EDGE,"E9"),sQuery(id+"F0.wireOp",EDGE,"E10"),sQuery(id+"F0.wireOp",EDGE,"E11.filletArc"),sQuery(id+"F0.wireOp",EDGE,"E12.filletArc"),sQuery(id+"F0.wireOp",EDGE,"E13.filletArc"),sQuery(id+"F0.wireOp",EDGE,"E14.MirrorCS"),sQuery(id+"F0.wireOp",EDGE,"E15.MirrorCS"),sQuery(id+"F0.wireOp",EDGE,"E16.MirrorCS"),sQuery(id+"F0.wireOp",EDGE,"E17.MirrorCS"),sQuery(id+"F0.wireOp",EDGE,"E18.MirrorCS"),sQuery(id+"F0.wireOp",EDGE,"E19.MirrorCS"),sQuery(id+"F0.wireOp",EDGE,"E21.MirrorCS"),sQuery(id+"F0.wireOp",EDGE,"E22.MirrorCS"),sQuery(id+"F0.wireOp",EDGE,"E23.MirrorCS"),sQuery(id+"F0.wireOp",EDGE,"E24.MirrorCS"),sQuery(id+"F0.wireOp",EDGE,"E25.MirrorCS"),sQuery(id+"F0.wireOp",EDGE,"E20.MirrorCS"),sQuery(id+"F0.wireOp",EDGE,"E27.MirrorCS"),sQuery(id+"F0.wireOp",EDGE,"E28.MirrorCS"),sQuery(id+"F0.wireOp",EDGE,"E29.MirrorCS"),sQuery(id+"F0.wireOp",EDGE,"E30.MirrorCS"),sQuery(id+"F0.wireOp",EDGE,"E31.MirrorCS"),sQuery(id+"F0.wireOp",EDGE,"E32.MirrorCS"),sQuery(id+"F0.wireOp",EDGE,"E33"),sQuery(id+"F0.wireOp",EDGE,"E34.1.0"),sQuery(id+"F0.wireOp",EDGE,"E34.2.0"),sQuery(id+"F0.wireOp",EDGE,"E34.3.0"),sQuery(id+"F0.wireOp",EDGE,"E34.4.0"),sQuery(id+"F0.wireOp",EDGE,"E34.5.0"),sQuery(id+"F0.wireOp",EDGE,"E34.6.0"),sQuery(id+"F0.wireOp",EDGE,"E34.7.0"),sQuery(id+"F0.wireOp",EDGE,"E34.8.0"),sQuery(id+"F0.wireOp",EDGE,"E34.9.0"),sQuery(id+"F0.wireOp",EDGE,"E34.10.0"),sQuery(id+"F0.wireOp",EDGE,"E34.11.0"),sQuery(id+"F0.wireOp",EDGE,"E34.12.0"),sQuery(id+"F0.wireOp",EDGE,"E34.13.0"),sQuery(id+"F0.wireOp",EDGE,"E34.14.0"),sQuery(id+"F0.wireOp",EDGE,"E34.15.0"),sQuery(id+"F0.wireOp",EDGE,"E34.16.0"),sQuery(id+"F0.wireOp",EDGE,"E34.17.0"),sQuery(id+"F0.wireOp",EDGE,"E34.18.0"),sQuery(id+"F0.wireOp",EDGE,"E34.19.0"),sQuery(id+"F0.wireOp",EDGE,"E34.20.0"),sQuery(id+"F0.wireOp",EDGE,"E34.21.0"),sQuery(id+"F0.wireOp",EDGE,"E34.22.0"),sQuery(id+"F0.wireOp",EDGE,"E34.23.0"),sQuery(id+"F0.wireOp",EDGE,"E34.24.0"),sQuery(id+"F0.wireOp",EDGE,"E34.25.0"),sQuery(id+"F0.wireOp",EDGE,"E34.26.0"),sQuery(id+"F0.wireOp",EDGE,"E34.27.0"),sQuery(id+"F0.wireOp",EDGE,"E34.28.0"),sQuery(id+"F0.wireOp",EDGE,"E34.29.0"),sQuery(id+"F0.wireOp",EDGE,"E34.30.0"),sQuery(id+"F0.wireOp",EDGE,"E34.31.0"),sQuery(id+"F0.wireOp",EDGE,"E34.32.0"),sQuery(id+"F0.wireOp",EDGE,"E34.33.0"),sQuery(id+"F0.wireOp",EDGE,"E34.34.0"),sQuery(id+"F0.wireOp",EDGE,"E34.35.0"),sQuery(id+"F0.wireOp",EDGE,"E34.36.0"),sQuery(id+"F0.wireOp",EDGE,"E34.37.0"),sQuery(id+"F0.wireOp",EDGE,"E34.38.0"),sQuery(id+"F0.wireOp",EDGE,"E34.39.0"),sQuery(id+"F0.wireOp",EDGE,"E34.40.0"),sQuery(id+"F0.wireOp",EDGE,"E34.41.0"),sQuery(id+"F0.wireOp",EDGE,"E34.42.0"),sQuery(id+"F0.wireOp",EDGE,"E34.43.0"),sQuery(id+"F0.wireOp",EDGE,"E34.44.0"),sQuery(id+"F0.wireOp",EDGE,"E34.45.0"),sQuery(id+"F0.wireOp",EDGE,"E34.46.0"),sQuery(id+"F0.wireOp",EDGE,"E34.47.0"),sQuery(id+"F0.wireOp",EDGE,"E34.48.0"),sQuery(id+"F0.wireOp",EDGE,"E34.49.0"),sQuery(id+"F0.wireOp",EDGE,"E34.50.0"),sQuery(id+"F0.wireOp",EDGE,"E34.51.0"),sQuery(id+"F0.wireOp",EDGE,"E34.52.0"),sQuery(id+"F0.wireOp",EDGE,"E34.53.0"),sQuery(id+"F0.wireOp",EDGE,"E34.54.0"),sQuery(id+"F0.wireOp",EDGE,"E34.55.0"),sQuery(id+"F0.wireOp",EDGE,"E34.56.0"),sQuery(id+"F0.wireOp",EDGE,"E34.57.0"),sQuery(id+"F0.wireOp",EDGE,"E34.58.0"),sQuery(id+"F0.wireOp",EDGE,"E34.59.0")])]});
            transform(context, id + "F2", {"entities" : qUnion([Q0]), "transformType" : TransformType.TRANSLATION_3D, "dx" : 0 * mm, "dy" : 0 * mm, "dz" : 0 * mm, "makeCopy" : true});
        }
        {
            var Q0;
            Q0=makeQuery(id+"F1.opExtrude","SWEPT_BODY",BODY,{"disambiguationData":[OSD([sQuery(id+"F0.wireOp",EDGE,"E0"),sQuery(id+"F0.wireOp",EDGE,"E1"),sQuery(id+"F0.wireOp",EDGE,"E2"),sQuery(id+"F0.wireOp",EDGE,"E3"),sQuery(id+"F0.wireOp",EDGE,"E4.MirrorCS"),sQuery(id+"F0.wireOp",EDGE,"E5.MirrorCS"),sQuery(id+"F0.wireOp",EDGE,"E6.MirrorCS"),sQuery(id+"F0.wireOp",EDGE,"E7.1.0"),sQuery(id+"F0.wireOp",EDGE,"E7.1.1"),sQuery(id+"F0.wireOp",EDGE,"E7.1.2"),sQuery(id+"F0.wireOp",EDGE,"E7.1.3"),sQuery(id+"F0.wireOp",EDGE,"E7.1.4"),sQuery(id+"F0.wireOp",EDGE,"E7.1.5"),sQuery(id+"F0.wireOp",EDGE,"E7.2.0"),sQuery(id+"F0.wireOp",EDGE,"E7.2.1"),sQuery(id+"F0.wireOp",EDGE,"E7.2.2"),sQuery(id+"F0.wireOp",EDGE,"E7.2.3"),sQuery(id+"F0.wireOp",EDGE,"E7.2.4"),sQuery(id+"F0.wireOp",EDGE,"E7.2.5"),sQuery(id+"F0.wireOp",EDGE,"E7.3.0"),sQuery(id+"F0.wireOp",EDGE,"E7.3.1"),sQuery(id+"F0.wireOp",EDGE,"E7.3.2"),sQuery(id+"F0.wireOp",EDGE,"E7.3.3"),sQuery(id+"F0.wireOp",EDGE,"E7.3.4"),sQuery(id+"F0.wireOp",EDGE,"E7.3.5"),sQuery(id+"F0.wireOp",EDGE,"E7.4.0"),sQuery(id+"F0.wireOp",EDGE,"E7.4.1"),sQuery(id+"F0.wireOp",EDGE,"E7.4.2"),sQuery(id+"F0.wireOp",EDGE,"E7.4.3"),sQuery(id+"F0.wireOp",EDGE,"E7.4.4"),sQuery(id+"F0.wireOp",EDGE,"E7.4.5"),sQuery(id+"F0.wireOp",EDGE,"E7.5.0"),sQuery(id+"F0.wireOp",EDGE,"E7.5.1"),sQuery(id+"F0.wireOp",EDGE,"E7.5.2"),sQuery(id+"F0.wireOp",EDGE,"E7.5.3"),sQuery(id+"F0.wireOp",EDGE,"E7.5.4"),sQuery(id+"F0.wireOp",EDGE,"E7.5.5"),sQuery(id+"F0.wireOp",EDGE,"E7.6.0"),sQuery(id+"F0.wireOp",EDGE,"E7.6.1"),sQuery(id+"F0.wireOp",EDGE,"E7.6.2"),sQuery(id+"F0.wireOp",EDGE,"E7.6.3"),sQuery(id+"F0.wireOp",EDGE,"E7.6.4"),sQuery(id+"F0.wireOp",EDGE,"E7.6.5"),sQuery(id+"F0.wireOp",EDGE,"E7.7.0"),sQuery(id+"F0.wireOp",EDGE,"E7.7.1"),sQuery(id+"F0.wireOp",EDGE,"E7.7.2"),sQuery(id+"F0.wireOp",EDGE,"E7.7.3"),sQuery(id+"F0.wireOp",EDGE,"E7.7.4"),sQuery(id+"F0.wireOp",EDGE,"E7.7.5"),sQuery(id+"F0.wireOp",EDGE,"E7.8.0"),sQuery(id+"F0.wireOp",EDGE,"E7.8.1"),sQuery(id+"F0.wireOp",EDGE,"E7.8.2"),sQuery(id+"F0.wireOp",EDGE,"E7.8.3"),sQuery(id+"F0.wireOp",EDGE,"E7.8.4"),sQuery(id+"F0.wireOp",EDGE,"E7.8.5"),sQuery(id+"F0.wireOp",EDGE,"E7.9.0"),sQuery(id+"F0.wireOp",EDGE,"E7.9.1"),sQuery(id+"F0.wireOp",EDGE,"E7.9.2"),sQuery(id+"F0.wireOp",EDGE,"E7.9.3"),sQuery(id+"F0.wireOp",EDGE,"E7.9.4"),sQuery(id+"F0.wireOp",EDGE,"E7.9.5"),sQuery(id+"F0.wireOp",EDGE,"E7.10.0"),sQuery(id+"F0.wireOp",EDGE,"E7.10.1"),sQuery(id+"F0.wireOp",EDGE,"E7.10.2"),sQuery(id+"F0.wireOp",EDGE,"E7.10.3"),sQuery(id+"F0.wireOp",EDGE,"E7.10.4"),sQuery(id+"F0.wireOp",EDGE,"E7.10.5"),sQuery(id+"F0.wireOp",EDGE,"E7.11.0"),sQuery(id+"F0.wireOp",EDGE,"E7.11.1"),sQuery(id+"F0.wireOp",EDGE,"E7.11.2"),sQuery(id+"F0.wireOp",EDGE,"E7.11.3"),sQuery(id+"F0.wireOp",EDGE,"E7.11.4"),sQuery(id+"F0.wireOp",EDGE,"E7.11.5"),sQuery(id+"F0.wireOp",EDGE,"E7.12.0"),sQuery(id+"F0.wireOp",EDGE,"E7.12.1"),sQuery(id+"F0.wireOp",EDGE,"E7.12.2"),sQuery(id+"F0.wireOp",EDGE,"E7.12.3"),sQuery(id+"F0.wireOp",EDGE,"E7.12.4"),sQuery(id+"F0.wireOp",EDGE,"E7.12.5"),sQuery(id+"F0.wireOp",EDGE,"E7.13.0"),sQuery(id+"F0.wireOp",EDGE,"E7.13.1"),sQuery(id+"F0.wireOp",EDGE,"E7.13.2"),sQuery(id+"F0.wireOp",EDGE,"E7.13.3"),sQuery(id+"F0.wireOp",EDGE,"E7.13.4"),sQuery(id+"F0.wireOp",EDGE,"E7.13.5"),sQuery(id+"F0.wireOp",EDGE,"E7.14.0"),sQuery(id+"F0.wireOp",EDGE,"E7.14.1"),sQuery(id+"F0.wireOp",EDGE,"E7.14.2"),sQuery(id+"F0.wireOp",EDGE,"E7.14.3"),sQuery(id+"F0.wireOp",EDGE,"E7.14.4"),sQuery(id+"F0.wireOp",EDGE,"E7.14.5"),sQuery(id+"F0.wireOp",EDGE,"E7.15.0"),sQuery(id+"F0.wireOp",EDGE,"E7.15.1"),sQuery(id+"F0.wireOp",EDGE,"E7.15.2"),sQuery(id+"F0.wireOp",EDGE,"E7.15.3"),sQuery(id+"F0.wireOp",EDGE,"E7.15.4"),sQuery(id+"F0.wireOp",EDGE,"E7.15.5"),sQuery(id+"F0.wireOp",EDGE,"E7.16.0"),sQuery(id+"F0.wireOp",EDGE,"E7.16.1"),sQuery(id+"F0.wireOp",EDGE,"E7.16.2"),sQuery(id+"F0.wireOp",EDGE,"E7.16.3"),sQuery(id+"F0.wireOp",EDGE,"E7.16.4"),sQuery(id+"F0.wireOp",EDGE,"E7.16.5"),sQuery(id+"F0.wireOp",EDGE,"E7.17.0"),sQuery(id+"F0.wireOp",EDGE,"E7.17.1"),sQuery(id+"F0.wireOp",EDGE,"E7.17.2"),sQuery(id+"F0.wireOp",EDGE,"E7.17.3"),sQuery(id+"F0.wireOp",EDGE,"E7.17.4"),sQuery(id+"F0.wireOp",EDGE,"E7.17.5"),sQuery(id+"F0.wireOp",EDGE,"E7.18.0"),sQuery(id+"F0.wireOp",EDGE,"E7.18.1"),sQuery(id+"F0.wireOp",EDGE,"E7.18.2"),sQuery(id+"F0.wireOp",EDGE,"E7.18.3"),sQuery(id+"F0.wireOp",EDGE,"E7.18.4"),sQuery(id+"F0.wireOp",EDGE,"E7.18.5"),sQuery(id+"F0.wireOp",EDGE,"E7.19.0"),sQuery(id+"F0.wireOp",EDGE,"E7.19.1"),sQuery(id+"F0.wireOp",EDGE,"E7.19.2"),sQuery(id+"F0.wireOp",EDGE,"E7.19.3"),sQuery(id+"F0.wireOp",EDGE,"E7.19.4"),sQuery(id+"F0.wireOp",EDGE,"E7.19.5"),sQuery(id+"F0.wireOp",EDGE,"E7.20.0"),sQuery(id+"F0.wireOp",EDGE,"E7.20.1"),sQuery(id+"F0.wireOp",EDGE,"E7.20.2"),sQuery(id+"F0.wireOp",EDGE,"E7.20.3"),sQuery(id+"F0.wireOp",EDGE,"E7.20.4"),sQuery(id+"F0.wireOp",EDGE,"E7.20.5"),sQuery(id+"F0.wireOp",EDGE,"E7.21.0"),sQuery(id+"F0.wireOp",EDGE,"E7.21.1"),sQuery(id+"F0.wireOp",EDGE,"E7.21.2"),sQuery(id+"F0.wireOp",EDGE,"E7.21.3"),sQuery(id+"F0.wireOp",EDGE,"E7.21.4"),sQuery(id+"F0.wireOp",EDGE,"E7.21.5"),sQuery(id+"F0.wireOp",EDGE,"E7.22.0"),sQuery(id+"F0.wireOp",EDGE,"E7.22.1"),sQuery(id+"F0.wireOp",EDGE,"E7.22.2"),sQuery(id+"F0.wireOp",EDGE,"E7.22.3"),sQuery(id+"F0.wireOp",EDGE,"E7.22.4"),sQuery(id+"F0.wireOp",EDGE,"E7.22.5"),sQuery(id+"F0.wireOp",EDGE,"E7.23.0"),sQuery(id+"F0.wireOp",EDGE,"E7.23.1"),sQuery(id+"F0.wireOp",EDGE,"E7.23.2"),sQuery(id+"F0.wireOp",EDGE,"E7.23.3"),sQuery(id+"F0.wireOp",EDGE,"E7.23.4"),sQuery(id+"F0.wireOp",EDGE,"E7.23.5"),sQuery(id+"F0.wireOp",EDGE,"E7.24.0"),sQuery(id+"F0.wireOp",EDGE,"E7.24.1"),sQuery(id+"F0.wireOp",EDGE,"E7.24.2"),sQuery(id+"F0.wireOp",EDGE,"E7.24.3"),sQuery(id+"F0.wireOp",EDGE,"E7.24.4"),sQuery(id+"F0.wireOp",EDGE,"E7.24.5"),sQuery(id+"F0.wireOp",EDGE,"E7.25.0"),sQuery(id+"F0.wireOp",EDGE,"E7.25.1"),sQuery(id+"F0.wireOp",EDGE,"E7.25.2"),sQuery(id+"F0.wireOp",EDGE,"E7.25.3"),sQuery(id+"F0.wireOp",EDGE,"E7.25.4"),sQuery(id+"F0.wireOp",EDGE,"E7.25.5"),sQuery(id+"F0.wireOp",EDGE,"E7.26.0"),sQuery(id+"F0.wireOp",EDGE,"E7.26.1"),sQuery(id+"F0.wireOp",EDGE,"E7.26.2"),sQuery(id+"F0.wireOp",EDGE,"E7.26.3"),sQuery(id+"F0.wireOp",EDGE,"E7.26.4"),sQuery(id+"F0.wireOp",EDGE,"E7.26.5"),sQuery(id+"F0.wireOp",EDGE,"E7.27.0"),sQuery(id+"F0.wireOp",EDGE,"E7.27.1"),sQuery(id+"F0.wireOp",EDGE,"E7.27.2"),sQuery(id+"F0.wireOp",EDGE,"E7.27.3"),sQuery(id+"F0.wireOp",EDGE,"E7.27.4"),sQuery(id+"F0.wireOp",EDGE,"E7.27.5"),sQuery(id+"F0.wireOp",EDGE,"E7.28.0"),sQuery(id+"F0.wireOp",EDGE,"E7.28.1"),sQuery(id+"F0.wireOp",EDGE,"E7.28.2"),sQuery(id+"F0.wireOp",EDGE,"E7.28.3"),sQuery(id+"F0.wireOp",EDGE,"E7.28.4"),sQuery(id+"F0.wireOp",EDGE,"E7.28.5"),sQuery(id+"F0.wireOp",EDGE,"E7.29.0"),sQuery(id+"F0.wireOp",EDGE,"E7.29.1"),sQuery(id+"F0.wireOp",EDGE,"E7.29.2"),sQuery(id+"F0.wireOp",EDGE,"E7.29.3"),sQuery(id+"F0.wireOp",EDGE,"E7.29.4"),sQuery(id+"F0.wireOp",EDGE,"E7.29.5"),sQuery(id+"F0.wireOp",EDGE,"E7.30.0"),sQuery(id+"F0.wireOp",EDGE,"E7.30.1"),sQuery(id+"F0.wireOp",EDGE,"E7.30.2"),sQuery(id+"F0.wireOp",EDGE,"E7.30.3"),sQuery(id+"F0.wireOp",EDGE,"E7.30.4"),sQuery(id+"F0.wireOp",EDGE,"E7.30.5"),sQuery(id+"F0.wireOp",EDGE,"E7.31.0"),sQuery(id+"F0.wireOp",EDGE,"E7.31.1"),sQuery(id+"F0.wireOp",EDGE,"E7.31.2"),sQuery(id+"F0.wireOp",EDGE,"E7.31.3"),sQuery(id+"F0.wireOp",EDGE,"E7.31.4"),sQuery(id+"F0.wireOp",EDGE,"E7.31.5"),sQuery(id+"F0.wireOp",EDGE,"E7.32.0"),sQuery(id+"F0.wireOp",EDGE,"E7.32.1"),sQuery(id+"F0.wireOp",EDGE,"E7.32.2"),sQuery(id+"F0.wireOp",EDGE,"E7.32.3"),sQuery(id+"F0.wireOp",EDGE,"E7.32.4"),sQuery(id+"F0.wireOp",EDGE,"E7.32.5"),sQuery(id+"F0.wireOp",EDGE,"E7.33.0"),sQuery(id+"F0.wireOp",EDGE,"E7.33.1"),sQuery(id+"F0.wireOp",EDGE,"E7.33.2"),sQuery(id+"F0.wireOp",EDGE,"E7.33.3"),sQuery(id+"F0.wireOp",EDGE,"E7.33.4"),sQuery(id+"F0.wireOp",EDGE,"E7.33.5"),sQuery(id+"F0.wireOp",EDGE,"E7.34.0"),sQuery(id+"F0.wireOp",EDGE,"E7.34.1"),sQuery(id+"F0.wireOp",EDGE,"E7.34.2"),sQuery(id+"F0.wireOp",EDGE,"E7.34.3"),sQuery(id+"F0.wireOp",EDGE,"E7.34.4"),sQuery(id+"F0.wireOp",EDGE,"E7.34.5"),sQuery(id+"F0.wireOp",EDGE,"E7.35.0"),sQuery(id+"F0.wireOp",EDGE,"E7.35.1"),sQuery(id+"F0.wireOp",EDGE,"E7.35.2"),sQuery(id+"F0.wireOp",EDGE,"E7.35.3"),sQuery(id+"F0.wireOp",EDGE,"E7.35.4"),sQuery(id+"F0.wireOp",EDGE,"E7.35.5"),sQuery(id+"F0.wireOp",EDGE,"E7.36.0"),sQuery(id+"F0.wireOp",EDGE,"E7.36.1"),sQuery(id+"F0.wireOp",EDGE,"E7.36.2"),sQuery(id+"F0.wireOp",EDGE,"E7.36.3"),sQuery(id+"F0.wireOp",EDGE,"E7.36.4"),sQuery(id+"F0.wireOp",EDGE,"E7.36.5"),sQuery(id+"F0.wireOp",EDGE,"E7.37.0"),sQuery(id+"F0.wireOp",EDGE,"E7.37.1"),sQuery(id+"F0.wireOp",EDGE,"E7.37.2"),sQuery(id+"F0.wireOp",EDGE,"E7.37.3"),sQuery(id+"F0.wireOp",EDGE,"E7.37.4"),sQuery(id+"F0.wireOp",EDGE,"E7.37.5"),sQuery(id+"F0.wireOp",EDGE,"E7.38.0"),sQuery(id+"F0.wireOp",EDGE,"E7.38.1"),sQuery(id+"F0.wireOp",EDGE,"E7.38.2"),sQuery(id+"F0.wireOp",EDGE,"E7.38.3"),sQuery(id+"F0.wireOp",EDGE,"E7.38.4"),sQuery(id+"F0.wireOp",EDGE,"E7.38.5"),sQuery(id+"F0.wireOp",EDGE,"E7.39.0"),sQuery(id+"F0.wireOp",EDGE,"E7.39.1"),sQuery(id+"F0.wireOp",EDGE,"E7.39.2"),sQuery(id+"F0.wireOp",EDGE,"E7.39.3"),sQuery(id+"F0.wireOp",EDGE,"E7.39.4"),sQuery(id+"F0.wireOp",EDGE,"E7.39.5"),sQuery(id+"F0.wireOp",EDGE,"E7.40.0"),sQuery(id+"F0.wireOp",EDGE,"E7.40.1"),sQuery(id+"F0.wireOp",EDGE,"E7.40.2"),sQuery(id+"F0.wireOp",EDGE,"E7.40.3"),sQuery(id+"F0.wireOp",EDGE,"E7.40.4"),sQuery(id+"F0.wireOp",EDGE,"E7.40.5"),sQuery(id+"F0.wireOp",EDGE,"E7.41.0"),sQuery(id+"F0.wireOp",EDGE,"E7.41.1"),sQuery(id+"F0.wireOp",EDGE,"E7.41.2"),sQuery(id+"F0.wireOp",EDGE,"E7.41.3"),sQuery(id+"F0.wireOp",EDGE,"E7.41.4"),sQuery(id+"F0.wireOp",EDGE,"E7.41.5"),sQuery(id+"F0.wireOp",EDGE,"E7.42.0"),sQuery(id+"F0.wireOp",EDGE,"E7.42.1"),sQuery(id+"F0.wireOp",EDGE,"E7.42.2"),sQuery(id+"F0.wireOp",EDGE,"E7.42.3"),sQuery(id+"F0.wireOp",EDGE,"E7.42.4"),sQuery(id+"F0.wireOp",EDGE,"E7.42.5"),sQuery(id+"F0.wireOp",EDGE,"E7.43.0"),sQuery(id+"F0.wireOp",EDGE,"E7.43.1"),sQuery(id+"F0.wireOp",EDGE,"E7.43.2"),sQuery(id+"F0.wireOp",EDGE,"E7.43.3"),sQuery(id+"F0.wireOp",EDGE,"E7.43.4"),sQuery(id+"F0.wireOp",EDGE,"E7.43.5"),sQuery(id+"F0.wireOp",EDGE,"E7.44.0"),sQuery(id+"F0.wireOp",EDGE,"E7.44.1"),sQuery(id+"F0.wireOp",EDGE,"E7.44.2"),sQuery(id+"F0.wireOp",EDGE,"E7.44.3"),sQuery(id+"F0.wireOp",EDGE,"E7.44.4"),sQuery(id+"F0.wireOp",EDGE,"E7.44.5"),sQuery(id+"F0.wireOp",EDGE,"E7.45.0"),sQuery(id+"F0.wireOp",EDGE,"E7.45.1"),sQuery(id+"F0.wireOp",EDGE,"E7.45.2"),sQuery(id+"F0.wireOp",EDGE,"E7.45.3"),sQuery(id+"F0.wireOp",EDGE,"E7.45.4"),sQuery(id+"F0.wireOp",EDGE,"E7.45.5"),sQuery(id+"F0.wireOp",EDGE,"E7.46.0"),sQuery(id+"F0.wireOp",EDGE,"E7.46.1"),sQuery(id+"F0.wireOp",EDGE,"E7.46.2"),sQuery(id+"F0.wireOp",EDGE,"E7.46.3"),sQuery(id+"F0.wireOp",EDGE,"E7.46.4"),sQuery(id+"F0.wireOp",EDGE,"E7.46.5"),sQuery(id+"F0.wireOp",EDGE,"E7.47.0"),sQuery(id+"F0.wireOp",EDGE,"E7.47.1"),sQuery(id+"F0.wireOp",EDGE,"E7.47.2"),sQuery(id+"F0.wireOp",EDGE,"E7.47.3"),sQuery(id+"F0.wireOp",EDGE,"E7.47.4"),sQuery(id+"F0.wireOp",EDGE,"E7.47.5"),sQuery(id+"F0.wireOp",EDGE,"E7.48.0"),sQuery(id+"F0.wireOp",EDGE,"E7.48.1"),sQuery(id+"F0.wireOp",EDGE,"E7.48.2"),sQuery(id+"F0.wireOp",EDGE,"E7.48.3"),sQuery(id+"F0.wireOp",EDGE,"E7.48.4"),sQuery(id+"F0.wireOp",EDGE,"E7.48.5"),sQuery(id+"F0.wireOp",EDGE,"E7.49.0"),sQuery(id+"F0.wireOp",EDGE,"E7.49.1"),sQuery(id+"F0.wireOp",EDGE,"E7.49.2"),sQuery(id+"F0.wireOp",EDGE,"E7.49.3"),sQuery(id+"F0.wireOp",EDGE,"E7.49.4"),sQuery(id+"F0.wireOp",EDGE,"E7.49.5"),sQuery(id+"F0.wireOp",EDGE,"E7.50.0"),sQuery(id+"F0.wireOp",EDGE,"E7.50.1"),sQuery(id+"F0.wireOp",EDGE,"E7.50.2"),sQuery(id+"F0.wireOp",EDGE,"E7.50.3"),sQuery(id+"F0.wireOp",EDGE,"E7.50.4"),sQuery(id+"F0.wireOp",EDGE,"E7.50.5"),sQuery(id+"F0.wireOp",EDGE,"E7.51.0"),sQuery(id+"F0.wireOp",EDGE,"E7.51.1"),sQuery(id+"F0.wireOp",EDGE,"E7.51.2"),sQuery(id+"F0.wireOp",EDGE,"E7.51.3"),sQuery(id+"F0.wireOp",EDGE,"E7.51.4"),sQuery(id+"F0.wireOp",EDGE,"E7.51.5"),sQuery(id+"F0.wireOp",EDGE,"E7.52.0"),sQuery(id+"F0.wireOp",EDGE,"E7.52.1"),sQuery(id+"F0.wireOp",EDGE,"E7.52.2"),sQuery(id+"F0.wireOp",EDGE,"E7.52.3"),sQuery(id+"F0.wireOp",EDGE,"E7.52.4"),sQuery(id+"F0.wireOp",EDGE,"E7.52.5"),sQuery(id+"F0.wireOp",EDGE,"E7.53.0"),sQuery(id+"F0.wireOp",EDGE,"E7.53.1"),sQuery(id+"F0.wireOp",EDGE,"E7.53.2"),sQuery(id+"F0.wireOp",EDGE,"E7.53.3"),sQuery(id+"F0.wireOp",EDGE,"E7.53.4"),sQuery(id+"F0.wireOp",EDGE,"E7.53.5"),sQuery(id+"F0.wireOp",EDGE,"E7.54.0"),sQuery(id+"F0.wireOp",EDGE,"E7.54.1"),sQuery(id+"F0.wireOp",EDGE,"E7.54.2"),sQuery(id+"F0.wireOp",EDGE,"E7.54.3"),sQuery(id+"F0.wireOp",EDGE,"E7.54.4"),sQuery(id+"F0.wireOp",EDGE,"E7.54.5"),sQuery(id+"F0.wireOp",EDGE,"E7.55.0"),sQuery(id+"F0.wireOp",EDGE,"E7.55.1"),sQuery(id+"F0.wireOp",EDGE,"E7.55.2"),sQuery(id+"F0.wireOp",EDGE,"E7.55.3"),sQuery(id+"F0.wireOp",EDGE,"E7.55.4"),sQuery(id+"F0.wireOp",EDGE,"E7.55.5"),sQuery(id+"F0.wireOp",EDGE,"E7.56.0"),sQuery(id+"F0.wireOp",EDGE,"E7.56.1"),sQuery(id+"F0.wireOp",EDGE,"E7.56.2"),sQuery(id+"F0.wireOp",EDGE,"E7.56.3"),sQuery(id+"F0.wireOp",EDGE,"E7.56.4"),sQuery(id+"F0.wireOp",EDGE,"E7.56.5"),sQuery(id+"F0.wireOp",EDGE,"E7.57.0"),sQuery(id+"F0.wireOp",EDGE,"E7.57.1"),sQuery(id+"F0.wireOp",EDGE,"E7.57.2"),sQuery(id+"F0.wireOp",EDGE,"E7.57.3"),sQuery(id+"F0.wireOp",EDGE,"E7.57.4"),sQuery(id+"F0.wireOp",EDGE,"E7.57.5"),sQuery(id+"F0.wireOp",EDGE,"E7.58.0"),sQuery(id+"F0.wireOp",EDGE,"E7.58.1"),sQuery(id+"F0.wireOp",EDGE,"E7.58.2"),sQuery(id+"F0.wireOp",EDGE,"E7.58.3"),sQuery(id+"F0.wireOp",EDGE,"E7.58.4"),sQuery(id+"F0.wireOp",EDGE,"E7.58.5"),sQuery(id+"F0.wireOp",EDGE,"E7.59.0"),sQuery(id+"F0.wireOp",EDGE,"E7.59.1"),sQuery(id+"F0.wireOp",EDGE,"E7.59.2"),sQuery(id+"F0.wireOp",EDGE,"E7.59.3"),sQuery(id+"F0.wireOp",EDGE,"E7.59.4"),sQuery(id+"F0.wireOp",EDGE,"E7.59.5"),sQuery(id+"F0.wireOp",EDGE,"E8"),sQuery(id+"F0.wireOp",EDGE,"E9"),sQuery(id+"F0.wireOp",EDGE,"E10"),sQuery(id+"F0.wireOp",EDGE,"E11.filletArc"),sQuery(id+"F0.wireOp",EDGE,"E12.filletArc"),sQuery(id+"F0.wireOp",EDGE,"E13.filletArc"),sQuery(id+"F0.wireOp",EDGE,"E14.MirrorCS"),sQuery(id+"F0.wireOp",EDGE,"E15.MirrorCS"),sQuery(id+"F0.wireOp",EDGE,"E16.MirrorCS"),sQuery(id+"F0.wireOp",EDGE,"E17.MirrorCS"),sQuery(id+"F0.wireOp",EDGE,"E18.MirrorCS"),sQuery(id+"F0.wireOp",EDGE,"E19.MirrorCS"),sQuery(id+"F0.wireOp",EDGE,"E21.MirrorCS"),sQuery(id+"F0.wireOp",EDGE,"E22.MirrorCS"),sQuery(id+"F0.wireOp",EDGE,"E23.MirrorCS"),sQuery(id+"F0.wireOp",EDGE,"E24.MirrorCS"),sQuery(id+"F0.wireOp",EDGE,"E25.MirrorCS"),sQuery(id+"F0.wireOp",EDGE,"E20.MirrorCS"),sQuery(id+"F0.wireOp",EDGE,"E27.MirrorCS"),sQuery(id+"F0.wireOp",EDGE,"E28.MirrorCS"),sQuery(id+"F0.wireOp",EDGE,"E29.MirrorCS"),sQuery(id+"F0.wireOp",EDGE,"E30.MirrorCS"),sQuery(id+"F0.wireOp",EDGE,"E31.MirrorCS"),sQuery(id+"F0.wireOp",EDGE,"E32.MirrorCS"),sQuery(id+"F0.wireOp",EDGE,"E33"),sQuery(id+"F0.wireOp",EDGE,"E34.1.0"),sQuery(id+"F0.wireOp",EDGE,"E34.2.0"),sQuery(id+"F0.wireOp",EDGE,"E34.3.0"),sQuery(id+"F0.wireOp",EDGE,"E34.4.0"),sQuery(id+"F0.wireOp",EDGE,"E34.5.0"),sQuery(id+"F0.wireOp",EDGE,"E34.6.0"),sQuery(id+"F0.wireOp",EDGE,"E34.7.0"),sQuery(id+"F0.wireOp",EDGE,"E34.8.0"),sQuery(id+"F0.wireOp",EDGE,"E34.9.0"),sQuery(id+"F0.wireOp",EDGE,"E34.10.0"),sQuery(id+"F0.wireOp",EDGE,"E34.11.0"),sQuery(id+"F0.wireOp",EDGE,"E34.12.0"),sQuery(id+"F0.wireOp",EDGE,"E34.13.0"),sQuery(id+"F0.wireOp",EDGE,"E34.14.0"),sQuery(id+"F0.wireOp",EDGE,"E34.15.0"),sQuery(id+"F0.wireOp",EDGE,"E34.16.0"),sQuery(id+"F0.wireOp",EDGE,"E34.17.0"),sQuery(id+"F0.wireOp",EDGE,"E34.18.0"),sQuery(id+"F0.wireOp",EDGE,"E34.19.0"),sQuery(id+"F0.wireOp",EDGE,"E34.20.0"),sQuery(id+"F0.wireOp",EDGE,"E34.21.0"),sQuery(id+"F0.wireOp",EDGE,"E34.22.0"),sQuery(id+"F0.wireOp",EDGE,"E34.23.0"),sQuery(id+"F0.wireOp",EDGE,"E34.24.0"),sQuery(id+"F0.wireOp",EDGE,"E34.25.0"),sQuery(id+"F0.wireOp",EDGE,"E34.26.0"),sQuery(id+"F0.wireOp",EDGE,"E34.27.0"),sQuery(id+"F0.wireOp",EDGE,"E34.28.0"),sQuery(id+"F0.wireOp",EDGE,"E34.29.0"),sQuery(id+"F0.wireOp",EDGE,"E34.30.0"),sQuery(id+"F0.wireOp",EDGE,"E34.31.0"),sQuery(id+"F0.wireOp",EDGE,"E34.32.0"),sQuery(id+"F0.wireOp",EDGE,"E34.33.0"),sQuery(id+"F0.wireOp",EDGE,"E34.34.0"),sQuery(id+"F0.wireOp",EDGE,"E34.35.0"),sQuery(id+"F0.wireOp",EDGE,"E34.36.0"),sQuery(id+"F0.wireOp",EDGE,"E34.37.0"),sQuery(id+"F0.wireOp",EDGE,"E34.38.0"),sQuery(id+"F0.wireOp",EDGE,"E34.39.0"),sQuery(id+"F0.wireOp",EDGE,"E34.40.0"),sQuery(id+"F0.wireOp",EDGE,"E34.41.0"),sQuery(id+"F0.wireOp",EDGE,"E34.42.0"),sQuery(id+"F0.wireOp",EDGE,"E34.43.0"),sQuery(id+"F0.wireOp",EDGE,"E34.44.0"),sQuery(id+"F0.wireOp",EDGE,"E34.45.0"),sQuery(id+"F0.wireOp",EDGE,"E34.46.0"),sQuery(id+"F0.wireOp",EDGE,"E34.47.0"),sQuery(id+"F0.wireOp",EDGE,"E34.48.0"),sQuery(id+"F0.wireOp",EDGE,"E34.49.0"),sQuery(id+"F0.wireOp",EDGE,"E34.50.0"),sQuery(id+"F0.wireOp",EDGE,"E34.51.0"),sQuery(id+"F0.wireOp",EDGE,"E34.52.0"),sQuery(id+"F0.wireOp",EDGE,"E34.53.0"),sQuery(id+"F0.wireOp",EDGE,"E34.54.0"),sQuery(id+"F0.wireOp",EDGE,"E34.55.0"),sQuery(id+"F0.wireOp",EDGE,"E34.56.0"),sQuery(id+"F0.wireOp",EDGE,"E34.57.0"),sQuery(id+"F0.wireOp",EDGE,"E34.58.0"),sQuery(id+"F0.wireOp",EDGE,"E34.59.0")])]});
            transform(context, id + "F3", {"entities" : qUnion([Q0]), "transformType" : TransformType.TRANSLATION_3D, "dx" : 0 * mm, "dy" : 0 * mm, "dz" : 0 * mm, "makeCopy" : true});
        }
        {
            var Q0;
            Q0=makeQuery(id+"F3.opPattern","COPY",BODY,{"derivedFrom":makeQuery(id+"F1.opExtrude","SWEPT_BODY",BODY,{"disambiguationData":[OSD([sQuery(id+"F0.wireOp",EDGE,"E0"),sQuery(id+"F0.wireOp",EDGE,"E1"),sQuery(id+"F0.wireOp",EDGE,"E2"),sQuery(id+"F0.wireOp",EDGE,"E3"),sQuery(id+"F0.wireOp",EDGE,"E4.MirrorCS"),sQuery(id+"F0.wireOp",EDGE,"E5.MirrorCS"),sQuery(id+"F0.wireOp",EDGE,"E6.MirrorCS"),sQuery(id+"F0.wireOp",EDGE,"E7.1.0"),sQuery(id+"F0.wireOp",EDGE,"E7.1.1"),sQuery(id+"F0.wireOp",EDGE,"E7.1.2"),sQuery(id+"F0.wireOp",EDGE,"E7.1.3"),sQuery(id+"F0.wireOp",EDGE,"E7.1.4"),sQuery(id+"F0.wireOp",EDGE,"E7.1.5"),sQuery(id+"F0.wireOp",EDGE,"E7.2.0"),sQuery(id+"F0.wireOp",EDGE,"E7.2.1"),sQuery(id+"F0.wireOp",EDGE,"E7.2.2"),sQuery(id+"F0.wireOp",EDGE,"E7.2.3"),sQuery(id+"F0.wireOp",EDGE,"E7.2.4"),sQuery(id+"F0.wireOp",EDGE,"E7.2.5"),sQuery(id+"F0.wireOp",EDGE,"E7.3.0"),sQuery(id+"F0.wireOp",EDGE,"E7.3.1"),sQuery(id+"F0.wireOp",EDGE,"E7.3.2"),sQuery(id+"F0.wireOp",EDGE,"E7.3.3"),sQuery(id+"F0.wireOp",EDGE,"E7.3.4"),sQuery(id+"F0.wireOp",EDGE,"E7.3.5"),sQuery(id+"F0.wireOp",EDGE,"E7.4.0"),sQuery(id+"F0.wireOp",EDGE,"E7.4.1"),sQuery(id+"F0.wireOp",EDGE,"E7.4.2"),sQuery(id+"F0.wireOp",EDGE,"E7.4.3"),sQuery(id+"F0.wireOp",EDGE,"E7.4.4"),sQuery(id+"F0.wireOp",EDGE,"E7.4.5"),sQuery(id+"F0.wireOp",EDGE,"E7.5.0"),sQuery(id+"F0.wireOp",EDGE,"E7.5.1"),sQuery(id+"F0.wireOp",EDGE,"E7.5.2"),sQuery(id+"F0.wireOp",EDGE,"E7.5.3"),sQuery(id+"F0.wireOp",EDGE,"E7.5.4"),sQuery(id+"F0.wireOp",EDGE,"E7.5.5"),sQuery(id+"F0.wireOp",EDGE,"E7.6.0"),sQuery(id+"F0.wireOp",EDGE,"E7.6.1"),sQuery(id+"F0.wireOp",EDGE,"E7.6.2"),sQuery(id+"F0.wireOp",EDGE,"E7.6.3"),sQuery(id+"F0.wireOp",EDGE,"E7.6.4"),sQuery(id+"F0.wireOp",EDGE,"E7.6.5"),sQuery(id+"F0.wireOp",EDGE,"E7.7.0"),sQuery(id+"F0.wireOp",EDGE,"E7.7.1"),sQuery(id+"F0.wireOp",EDGE,"E7.7.2"),sQuery(id+"F0.wireOp",EDGE,"E7.7.3"),sQuery(id+"F0.wireOp",EDGE,"E7.7.4"),sQuery(id+"F0.wireOp",EDGE,"E7.7.5"),sQuery(id+"F0.wireOp",EDGE,"E7.8.0"),sQuery(id+"F0.wireOp",EDGE,"E7.8.1"),sQuery(id+"F0.wireOp",EDGE,"E7.8.2"),sQuery(id+"F0.wireOp",EDGE,"E7.8.3"),sQuery(id+"F0.wireOp",EDGE,"E7.8.4"),sQuery(id+"F0.wireOp",EDGE,"E7.8.5"),sQuery(id+"F0.wireOp",EDGE,"E7.9.0"),sQuery(id+"F0.wireOp",EDGE,"E7.9.1"),sQuery(id+"F0.wireOp",EDGE,"E7.9.2"),sQuery(id+"F0.wireOp",EDGE,"E7.9.3"),sQuery(id+"F0.wireOp",EDGE,"E7.9.4"),sQuery(id+"F0.wireOp",EDGE,"E7.9.5"),sQuery(id+"F0.wireOp",EDGE,"E7.10.0"),sQuery(id+"F0.wireOp",EDGE,"E7.10.1"),sQuery(id+"F0.wireOp",EDGE,"E7.10.2"),sQuery(id+"F0.wireOp",EDGE,"E7.10.3"),sQuery(id+"F0.wireOp",EDGE,"E7.10.4"),sQuery(id+"F0.wireOp",EDGE,"E7.10.5"),sQuery(id+"F0.wireOp",EDGE,"E7.11.0"),sQuery(id+"F0.wireOp",EDGE,"E7.11.1"),sQuery(id+"F0.wireOp",EDGE,"E7.11.2"),sQuery(id+"F0.wireOp",EDGE,"E7.11.3"),sQuery(id+"F0.wireOp",EDGE,"E7.11.4"),sQuery(id+"F0.wireOp",EDGE,"E7.11.5"),sQuery(id+"F0.wireOp",EDGE,"E7.12.0"),sQuery(id+"F0.wireOp",EDGE,"E7.12.1"),sQuery(id+"F0.wireOp",EDGE,"E7.12.2"),sQuery(id+"F0.wireOp",EDGE,"E7.12.3"),sQuery(id+"F0.wireOp",EDGE,"E7.12.4"),sQuery(id+"F0.wireOp",EDGE,"E7.12.5"),sQuery(id+"F0.wireOp",EDGE,"E7.13.0"),sQuery(id+"F0.wireOp",EDGE,"E7.13.1"),sQuery(id+"F0.wireOp",EDGE,"E7.13.2"),sQuery(id+"F0.wireOp",EDGE,"E7.13.3"),sQuery(id+"F0.wireOp",EDGE,"E7.13.4"),sQuery(id+"F0.wireOp",EDGE,"E7.13.5"),sQuery(id+"F0.wireOp",EDGE,"E7.14.0"),sQuery(id+"F0.wireOp",EDGE,"E7.14.1"),sQuery(id+"F0.wireOp",EDGE,"E7.14.2"),sQuery(id+"F0.wireOp",EDGE,"E7.14.3"),sQuery(id+"F0.wireOp",EDGE,"E7.14.4"),sQuery(id+"F0.wireOp",EDGE,"E7.14.5"),sQuery(id+"F0.wireOp",EDGE,"E7.15.0"),sQuery(id+"F0.wireOp",EDGE,"E7.15.1"),sQuery(id+"F0.wireOp",EDGE,"E7.15.2"),sQuery(id+"F0.wireOp",EDGE,"E7.15.3"),sQuery(id+"F0.wireOp",EDGE,"E7.15.4"),sQuery(id+"F0.wireOp",EDGE,"E7.15.5"),sQuery(id+"F0.wireOp",EDGE,"E7.16.0"),sQuery(id+"F0.wireOp",EDGE,"E7.16.1"),sQuery(id+"F0.wireOp",EDGE,"E7.16.2"),sQuery(id+"F0.wireOp",EDGE,"E7.16.3"),sQuery(id+"F0.wireOp",EDGE,"E7.16.4"),sQuery(id+"F0.wireOp",EDGE,"E7.16.5"),sQuery(id+"F0.wireOp",EDGE,"E7.17.0"),sQuery(id+"F0.wireOp",EDGE,"E7.17.1"),sQuery(id+"F0.wireOp",EDGE,"E7.17.2"),sQuery(id+"F0.wireOp",EDGE,"E7.17.3"),sQuery(id+"F0.wireOp",EDGE,"E7.17.4"),sQuery(id+"F0.wireOp",EDGE,"E7.17.5"),sQuery(id+"F0.wireOp",EDGE,"E7.18.0"),sQuery(id+"F0.wireOp",EDGE,"E7.18.1"),sQuery(id+"F0.wireOp",EDGE,"E7.18.2"),sQuery(id+"F0.wireOp",EDGE,"E7.18.3"),sQuery(id+"F0.wireOp",EDGE,"E7.18.4"),sQuery(id+"F0.wireOp",EDGE,"E7.18.5"),sQuery(id+"F0.wireOp",EDGE,"E7.19.0"),sQuery(id+"F0.wireOp",EDGE,"E7.19.1"),sQuery(id+"F0.wireOp",EDGE,"E7.19.2"),sQuery(id+"F0.wireOp",EDGE,"E7.19.3"),sQuery(id+"F0.wireOp",EDGE,"E7.19.4"),sQuery(id+"F0.wireOp",EDGE,"E7.19.5"),sQuery(id+"F0.wireOp",EDGE,"E7.20.0"),sQuery(id+"F0.wireOp",EDGE,"E7.20.1"),sQuery(id+"F0.wireOp",EDGE,"E7.20.2"),sQuery(id+"F0.wireOp",EDGE,"E7.20.3"),sQuery(id+"F0.wireOp",EDGE,"E7.20.4"),sQuery(id+"F0.wireOp",EDGE,"E7.20.5"),sQuery(id+"F0.wireOp",EDGE,"E7.21.0"),sQuery(id+"F0.wireOp",EDGE,"E7.21.1"),sQuery(id+"F0.wireOp",EDGE,"E7.21.2"),sQuery(id+"F0.wireOp",EDGE,"E7.21.3"),sQuery(id+"F0.wireOp",EDGE,"E7.21.4"),sQuery(id+"F0.wireOp",EDGE,"E7.21.5"),sQuery(id+"F0.wireOp",EDGE,"E7.22.0"),sQuery(id+"F0.wireOp",EDGE,"E7.22.1"),sQuery(id+"F0.wireOp",EDGE,"E7.22.2"),sQuery(id+"F0.wireOp",EDGE,"E7.22.3"),sQuery(id+"F0.wireOp",EDGE,"E7.22.4"),sQuery(id+"F0.wireOp",EDGE,"E7.22.5"),sQuery(id+"F0.wireOp",EDGE,"E7.23.0"),sQuery(id+"F0.wireOp",EDGE,"E7.23.1"),sQuery(id+"F0.wireOp",EDGE,"E7.23.2"),sQuery(id+"F0.wireOp",EDGE,"E7.23.3"),sQuery(id+"F0.wireOp",EDGE,"E7.23.4"),sQuery(id+"F0.wireOp",EDGE,"E7.23.5"),sQuery(id+"F0.wireOp",EDGE,"E7.24.0"),sQuery(id+"F0.wireOp",EDGE,"E7.24.1"),sQuery(id+"F0.wireOp",EDGE,"E7.24.2"),sQuery(id+"F0.wireOp",EDGE,"E7.24.3"),sQuery(id+"F0.wireOp",EDGE,"E7.24.4"),sQuery(id+"F0.wireOp",EDGE,"E7.24.5"),sQuery(id+"F0.wireOp",EDGE,"E7.25.0"),sQuery(id+"F0.wireOp",EDGE,"E7.25.1"),sQuery(id+"F0.wireOp",EDGE,"E7.25.2"),sQuery(id+"F0.wireOp",EDGE,"E7.25.3"),sQuery(id+"F0.wireOp",EDGE,"E7.25.4"),sQuery(id+"F0.wireOp",EDGE,"E7.25.5"),sQuery(id+"F0.wireOp",EDGE,"E7.26.0"),sQuery(id+"F0.wireOp",EDGE,"E7.26.1"),sQuery(id+"F0.wireOp",EDGE,"E7.26.2"),sQuery(id+"F0.wireOp",EDGE,"E7.26.3"),sQuery(id+"F0.wireOp",EDGE,"E7.26.4"),sQuery(id+"F0.wireOp",EDGE,"E7.26.5"),sQuery(id+"F0.wireOp",EDGE,"E7.27.0"),sQuery(id+"F0.wireOp",EDGE,"E7.27.1"),sQuery(id+"F0.wireOp",EDGE,"E7.27.2"),sQuery(id+"F0.wireOp",EDGE,"E7.27.3"),sQuery(id+"F0.wireOp",EDGE,"E7.27.4"),sQuery(id+"F0.wireOp",EDGE,"E7.27.5"),sQuery(id+"F0.wireOp",EDGE,"E7.28.0"),sQuery(id+"F0.wireOp",EDGE,"E7.28.1"),sQuery(id+"F0.wireOp",EDGE,"E7.28.2"),sQuery(id+"F0.wireOp",EDGE,"E7.28.3"),sQuery(id+"F0.wireOp",EDGE,"E7.28.4"),sQuery(id+"F0.wireOp",EDGE,"E7.28.5"),sQuery(id+"F0.wireOp",EDGE,"E7.29.0"),sQuery(id+"F0.wireOp",EDGE,"E7.29.1"),sQuery(id+"F0.wireOp",EDGE,"E7.29.2"),sQuery(id+"F0.wireOp",EDGE,"E7.29.3"),sQuery(id+"F0.wireOp",EDGE,"E7.29.4"),sQuery(id+"F0.wireOp",EDGE,"E7.29.5"),sQuery(id+"F0.wireOp",EDGE,"E7.30.0"),sQuery(id+"F0.wireOp",EDGE,"E7.30.1"),sQuery(id+"F0.wireOp",EDGE,"E7.30.2"),sQuery(id+"F0.wireOp",EDGE,"E7.30.3"),sQuery(id+"F0.wireOp",EDGE,"E7.30.4"),sQuery(id+"F0.wireOp",EDGE,"E7.30.5"),sQuery(id+"F0.wireOp",EDGE,"E7.31.0"),sQuery(id+"F0.wireOp",EDGE,"E7.31.1"),sQuery(id+"F0.wireOp",EDGE,"E7.31.2"),sQuery(id+"F0.wireOp",EDGE,"E7.31.3"),sQuery(id+"F0.wireOp",EDGE,"E7.31.4"),sQuery(id+"F0.wireOp",EDGE,"E7.31.5"),sQuery(id+"F0.wireOp",EDGE,"E7.32.0"),sQuery(id+"F0.wireOp",EDGE,"E7.32.1"),sQuery(id+"F0.wireOp",EDGE,"E7.32.2"),sQuery(id+"F0.wireOp",EDGE,"E7.32.3"),sQuery(id+"F0.wireOp",EDGE,"E7.32.4"),sQuery(id+"F0.wireOp",EDGE,"E7.32.5"),sQuery(id+"F0.wireOp",EDGE,"E7.33.0"),sQuery(id+"F0.wireOp",EDGE,"E7.33.1"),sQuery(id+"F0.wireOp",EDGE,"E7.33.2"),sQuery(id+"F0.wireOp",EDGE,"E7.33.3"),sQuery(id+"F0.wireOp",EDGE,"E7.33.4"),sQuery(id+"F0.wireOp",EDGE,"E7.33.5"),sQuery(id+"F0.wireOp",EDGE,"E7.34.0"),sQuery(id+"F0.wireOp",EDGE,"E7.34.1"),sQuery(id+"F0.wireOp",EDGE,"E7.34.2"),sQuery(id+"F0.wireOp",EDGE,"E7.34.3"),sQuery(id+"F0.wireOp",EDGE,"E7.34.4"),sQuery(id+"F0.wireOp",EDGE,"E7.34.5"),sQuery(id+"F0.wireOp",EDGE,"E7.35.0"),sQuery(id+"F0.wireOp",EDGE,"E7.35.1"),sQuery(id+"F0.wireOp",EDGE,"E7.35.2"),sQuery(id+"F0.wireOp",EDGE,"E7.35.3"),sQuery(id+"F0.wireOp",EDGE,"E7.35.4"),sQuery(id+"F0.wireOp",EDGE,"E7.35.5"),sQuery(id+"F0.wireOp",EDGE,"E7.36.0"),sQuery(id+"F0.wireOp",EDGE,"E7.36.1"),sQuery(id+"F0.wireOp",EDGE,"E7.36.2"),sQuery(id+"F0.wireOp",EDGE,"E7.36.3"),sQuery(id+"F0.wireOp",EDGE,"E7.36.4"),sQuery(id+"F0.wireOp",EDGE,"E7.36.5"),sQuery(id+"F0.wireOp",EDGE,"E7.37.0"),sQuery(id+"F0.wireOp",EDGE,"E7.37.1"),sQuery(id+"F0.wireOp",EDGE,"E7.37.2"),sQuery(id+"F0.wireOp",EDGE,"E7.37.3"),sQuery(id+"F0.wireOp",EDGE,"E7.37.4"),sQuery(id+"F0.wireOp",EDGE,"E7.37.5"),sQuery(id+"F0.wireOp",EDGE,"E7.38.0"),sQuery(id+"F0.wireOp",EDGE,"E7.38.1"),sQuery(id+"F0.wireOp",EDGE,"E7.38.2"),sQuery(id+"F0.wireOp",EDGE,"E7.38.3"),sQuery(id+"F0.wireOp",EDGE,"E7.38.4"),sQuery(id+"F0.wireOp",EDGE,"E7.38.5"),sQuery(id+"F0.wireOp",EDGE,"E7.39.0"),sQuery(id+"F0.wireOp",EDGE,"E7.39.1"),sQuery(id+"F0.wireOp",EDGE,"E7.39.2"),sQuery(id+"F0.wireOp",EDGE,"E7.39.3"),sQuery(id+"F0.wireOp",EDGE,"E7.39.4"),sQuery(id+"F0.wireOp",EDGE,"E7.39.5"),sQuery(id+"F0.wireOp",EDGE,"E7.40.0"),sQuery(id+"F0.wireOp",EDGE,"E7.40.1"),sQuery(id+"F0.wireOp",EDGE,"E7.40.2"),sQuery(id+"F0.wireOp",EDGE,"E7.40.3"),sQuery(id+"F0.wireOp",EDGE,"E7.40.4"),sQuery(id+"F0.wireOp",EDGE,"E7.40.5"),sQuery(id+"F0.wireOp",EDGE,"E7.41.0"),sQuery(id+"F0.wireOp",EDGE,"E7.41.1"),sQuery(id+"F0.wireOp",EDGE,"E7.41.2"),sQuery(id+"F0.wireOp",EDGE,"E7.41.3"),sQuery(id+"F0.wireOp",EDGE,"E7.41.4"),sQuery(id+"F0.wireOp",EDGE,"E7.41.5"),sQuery(id+"F0.wireOp",EDGE,"E7.42.0"),sQuery(id+"F0.wireOp",EDGE,"E7.42.1"),sQuery(id+"F0.wireOp",EDGE,"E7.42.2"),sQuery(id+"F0.wireOp",EDGE,"E7.42.3"),sQuery(id+"F0.wireOp",EDGE,"E7.42.4"),sQuery(id+"F0.wireOp",EDGE,"E7.42.5"),sQuery(id+"F0.wireOp",EDGE,"E7.43.0"),sQuery(id+"F0.wireOp",EDGE,"E7.43.1"),sQuery(id+"F0.wireOp",EDGE,"E7.43.2"),sQuery(id+"F0.wireOp",EDGE,"E7.43.3"),sQuery(id+"F0.wireOp",EDGE,"E7.43.4"),sQuery(id+"F0.wireOp",EDGE,"E7.43.5"),sQuery(id+"F0.wireOp",EDGE,"E7.44.0"),sQuery(id+"F0.wireOp",EDGE,"E7.44.1"),sQuery(id+"F0.wireOp",EDGE,"E7.44.2"),sQuery(id+"F0.wireOp",EDGE,"E7.44.3"),sQuery(id+"F0.wireOp",EDGE,"E7.44.4"),sQuery(id+"F0.wireOp",EDGE,"E7.44.5"),sQuery(id+"F0.wireOp",EDGE,"E7.45.0"),sQuery(id+"F0.wireOp",EDGE,"E7.45.1"),sQuery(id+"F0.wireOp",EDGE,"E7.45.2"),sQuery(id+"F0.wireOp",EDGE,"E7.45.3"),sQuery(id+"F0.wireOp",EDGE,"E7.45.4"),sQuery(id+"F0.wireOp",EDGE,"E7.45.5"),sQuery(id+"F0.wireOp",EDGE,"E7.46.0"),sQuery(id+"F0.wireOp",EDGE,"E7.46.1"),sQuery(id+"F0.wireOp",EDGE,"E7.46.2"),sQuery(id+"F0.wireOp",EDGE,"E7.46.3"),sQuery(id+"F0.wireOp",EDGE,"E7.46.4"),sQuery(id+"F0.wireOp",EDGE,"E7.46.5"),sQuery(id+"F0.wireOp",EDGE,"E7.47.0"),sQuery(id+"F0.wireOp",EDGE,"E7.47.1"),sQuery(id+"F0.wireOp",EDGE,"E7.47.2"),sQuery(id+"F0.wireOp",EDGE,"E7.47.3"),sQuery(id+"F0.wireOp",EDGE,"E7.47.4"),sQuery(id+"F0.wireOp",EDGE,"E7.47.5"),sQuery(id+"F0.wireOp",EDGE,"E7.48.0"),sQuery(id+"F0.wireOp",EDGE,"E7.48.1"),sQuery(id+"F0.wireOp",EDGE,"E7.48.2"),sQuery(id+"F0.wireOp",EDGE,"E7.48.3"),sQuery(id+"F0.wireOp",EDGE,"E7.48.4"),sQuery(id+"F0.wireOp",EDGE,"E7.48.5"),sQuery(id+"F0.wireOp",EDGE,"E7.49.0"),sQuery(id+"F0.wireOp",EDGE,"E7.49.1"),sQuery(id+"F0.wireOp",EDGE,"E7.49.2"),sQuery(id+"F0.wireOp",EDGE,"E7.49.3"),sQuery(id+"F0.wireOp",EDGE,"E7.49.4"),sQuery(id+"F0.wireOp",EDGE,"E7.49.5"),sQuery(id+"F0.wireOp",EDGE,"E7.50.0"),sQuery(id+"F0.wireOp",EDGE,"E7.50.1"),sQuery(id+"F0.wireOp",EDGE,"E7.50.2"),sQuery(id+"F0.wireOp",EDGE,"E7.50.3"),sQuery(id+"F0.wireOp",EDGE,"E7.50.4"),sQuery(id+"F0.wireOp",EDGE,"E7.50.5"),sQuery(id+"F0.wireOp",EDGE,"E7.51.0"),sQuery(id+"F0.wireOp",EDGE,"E7.51.1"),sQuery(id+"F0.wireOp",EDGE,"E7.51.2"),sQuery(id+"F0.wireOp",EDGE,"E7.51.3"),sQuery(id+"F0.wireOp",EDGE,"E7.51.4"),sQuery(id+"F0.wireOp",EDGE,"E7.51.5"),sQuery(id+"F0.wireOp",EDGE,"E7.52.0"),sQuery(id+"F0.wireOp",EDGE,"E7.52.1"),sQuery(id+"F0.wireOp",EDGE,"E7.52.2"),sQuery(id+"F0.wireOp",EDGE,"E7.52.3"),sQuery(id+"F0.wireOp",EDGE,"E7.52.4"),sQuery(id+"F0.wireOp",EDGE,"E7.52.5"),sQuery(id+"F0.wireOp",EDGE,"E7.53.0"),sQuery(id+"F0.wireOp",EDGE,"E7.53.1"),sQuery(id+"F0.wireOp",EDGE,"E7.53.2"),sQuery(id+"F0.wireOp",EDGE,"E7.53.3"),sQuery(id+"F0.wireOp",EDGE,"E7.53.4"),sQuery(id+"F0.wireOp",EDGE,"E7.53.5"),sQuery(id+"F0.wireOp",EDGE,"E7.54.0"),sQuery(id+"F0.wireOp",EDGE,"E7.54.1"),sQuery(id+"F0.wireOp",EDGE,"E7.54.2"),sQuery(id+"F0.wireOp",EDGE,"E7.54.3"),sQuery(id+"F0.wireOp",EDGE,"E7.54.4"),sQuery(id+"F0.wireOp",EDGE,"E7.54.5"),sQuery(id+"F0.wireOp",EDGE,"E7.55.0"),sQuery(id+"F0.wireOp",EDGE,"E7.55.1"),sQuery(id+"F0.wireOp",EDGE,"E7.55.2"),sQuery(id+"F0.wireOp",EDGE,"E7.55.3"),sQuery(id+"F0.wireOp",EDGE,"E7.55.4"),sQuery(id+"F0.wireOp",EDGE,"E7.55.5"),sQuery(id+"F0.wireOp",EDGE,"E7.56.0"),sQuery(id+"F0.wireOp",EDGE,"E7.56.1"),sQuery(id+"F0.wireOp",EDGE,"E7.56.2"),sQuery(id+"F0.wireOp",EDGE,"E7.56.3"),sQuery(id+"F0.wireOp",EDGE,"E7.56.4"),sQuery(id+"F0.wireOp",EDGE,"E7.56.5"),sQuery(id+"F0.wireOp",EDGE,"E7.57.0"),sQuery(id+"F0.wireOp",EDGE,"E7.57.1"),sQuery(id+"F0.wireOp",EDGE,"E7.57.2"),sQuery(id+"F0.wireOp",EDGE,"E7.57.3"),sQuery(id+"F0.wireOp",EDGE,"E7.57.4"),sQuery(id+"F0.wireOp",EDGE,"E7.57.5"),sQuery(id+"F0.wireOp",EDGE,"E7.58.0"),sQuery(id+"F0.wireOp",EDGE,"E7.58.1"),sQuery(id+"F0.wireOp",EDGE,"E7.58.2"),sQuery(id+"F0.wireOp",EDGE,"E7.58.3"),sQuery(id+"F0.wireOp",EDGE,"E7.58.4"),sQuery(id+"F0.wireOp",EDGE,"E7.58.5"),sQuery(id+"F0.wireOp",EDGE,"E7.59.0"),sQuery(id+"F0.wireOp",EDGE,"E7.59.1"),sQuery(id+"F0.wireOp",EDGE,"E7.59.2"),sQuery(id+"F0.wireOp",EDGE,"E7.59.3"),sQuery(id+"F0.wireOp",EDGE,"E7.59.4"),sQuery(id+"F0.wireOp",EDGE,"E7.59.5"),sQuery(id+"F0.wireOp",EDGE,"E8"),sQuery(id+"F0.wireOp",EDGE,"E9"),sQuery(id+"F0.wireOp",EDGE,"E10"),sQuery(id+"F0.wireOp",EDGE,"E11.filletArc"),sQuery(id+"F0.wireOp",EDGE,"E12.filletArc"),sQuery(id+"F0.wireOp",EDGE,"E13.filletArc"),sQuery(id+"F0.wireOp",EDGE,"E14.MirrorCS"),sQuery(id+"F0.wireOp",EDGE,"E15.MirrorCS"),sQuery(id+"F0.wireOp",EDGE,"E16.MirrorCS"),sQuery(id+"F0.wireOp",EDGE,"E17.MirrorCS"),sQuery(id+"F0.wireOp",EDGE,"E18.MirrorCS"),sQuery(id+"F0.wireOp",EDGE,"E19.MirrorCS"),sQuery(id+"F0.wireOp",EDGE,"E21.MirrorCS"),sQuery(id+"F0.wireOp",EDGE,"E22.MirrorCS"),sQuery(id+"F0.wireOp",EDGE,"E23.MirrorCS"),sQuery(id+"F0.wireOp",EDGE,"E24.MirrorCS"),sQuery(id+"F0.wireOp",EDGE,"E25.MirrorCS"),sQuery(id+"F0.wireOp",EDGE,"E20.MirrorCS"),sQuery(id+"F0.wireOp",EDGE,"E27.MirrorCS"),sQuery(id+"F0.wireOp",EDGE,"E28.MirrorCS"),sQuery(id+"F0.wireOp",EDGE,"E29.MirrorCS"),sQuery(id+"F0.wireOp",EDGE,"E30.MirrorCS"),sQuery(id+"F0.wireOp",EDGE,"E31.MirrorCS"),sQuery(id+"F0.wireOp",EDGE,"E32.MirrorCS"),sQuery(id+"F0.wireOp",EDGE,"E33"),sQuery(id+"F0.wireOp",EDGE,"E34.1.0"),sQuery(id+"F0.wireOp",EDGE,"E34.2.0"),sQuery(id+"F0.wireOp",EDGE,"E34.3.0"),sQuery(id+"F0.wireOp",EDGE,"E34.4.0"),sQuery(id+"F0.wireOp",EDGE,"E34.5.0"),sQuery(id+"F0.wireOp",EDGE,"E34.6.0"),sQuery(id+"F0.wireOp",EDGE,"E34.7.0"),sQuery(id+"F0.wireOp",EDGE,"E34.8.0"),sQuery(id+"F0.wireOp",EDGE,"E34.9.0"),sQuery(id+"F0.wireOp",EDGE,"E34.10.0"),sQuery(id+"F0.wireOp",EDGE,"E34.11.0"),sQuery(id+"F0.wireOp",EDGE,"E34.12.0"),sQuery(id+"F0.wireOp",EDGE,"E34.13.0"),sQuery(id+"F0.wireOp",EDGE,"E34.14.0"),sQuery(id+"F0.wireOp",EDGE,"E34.15.0"),sQuery(id+"F0.wireOp",EDGE,"E34.16.0"),sQuery(id+"F0.wireOp",EDGE,"E34.17.0"),sQuery(id+"F0.wireOp",EDGE,"E34.18.0"),sQuery(id+"F0.wireOp",EDGE,"E34.19.0"),sQuery(id+"F0.wireOp",EDGE,"E34.20.0"),sQuery(id+"F0.wireOp",EDGE,"E34.21.0"),sQuery(id+"F0.wireOp",EDGE,"E34.22.0"),sQuery(id+"F0.wireOp",EDGE,"E34.23.0"),sQuery(id+"F0.wireOp",EDGE,"E34.24.0"),sQuery(id+"F0.wireOp",EDGE,"E34.25.0"),sQuery(id+"F0.wireOp",EDGE,"E34.26.0"),sQuery(id+"F0.wireOp",EDGE,"E34.27.0"),sQuery(id+"F0.wireOp",EDGE,"E34.28.0"),sQuery(id+"F0.wireOp",EDGE,"E34.29.0"),sQuery(id+"F0.wireOp",EDGE,"E34.30.0"),sQuery(id+"F0.wireOp",EDGE,"E34.31.0"),sQuery(id+"F0.wireOp",EDGE,"E34.32.0"),sQuery(id+"F0.wireOp",EDGE,"E34.33.0"),sQuery(id+"F0.wireOp",EDGE,"E34.34.0"),sQuery(id+"F0.wireOp",EDGE,"E34.35.0"),sQuery(id+"F0.wireOp",EDGE,"E34.36.0"),sQuery(id+"F0.wireOp",EDGE,"E34.37.0"),sQuery(id+"F0.wireOp",EDGE,"E34.38.0"),sQuery(id+"F0.wireOp",EDGE,"E34.39.0"),sQuery(id+"F0.wireOp",EDGE,"E34.40.0"),sQuery(id+"F0.wireOp",EDGE,"E34.41.0"),sQuery(id+"F0.wireOp",EDGE,"E34.42.0"),sQuery(id+"F0.wireOp",EDGE,"E34.43.0"),sQuery(id+"F0.wireOp",EDGE,"E34.44.0"),sQuery(id+"F0.wireOp",EDGE,"E34.45.0"),sQuery(id+"F0.wireOp",EDGE,"E34.46.0"),sQuery(id+"F0.wireOp",EDGE,"E34.47.0"),sQuery(id+"F0.wireOp",EDGE,"E34.48.0"),sQuery(id+"F0.wireOp",EDGE,"E34.49.0"),sQuery(id+"F0.wireOp",EDGE,"E34.50.0"),sQuery(id+"F0.wireOp",EDGE,"E34.51.0"),sQuery(id+"F0.wireOp",EDGE,"E34.52.0"),sQuery(id+"F0.wireOp",EDGE,"E34.53.0"),sQuery(id+"F0.wireOp",EDGE,"E34.54.0"),sQuery(id+"F0.wireOp",EDGE,"E34.55.0"),sQuery(id+"F0.wireOp",EDGE,"E34.56.0"),sQuery(id+"F0.wireOp",EDGE,"E34.57.0"),sQuery(id+"F0.wireOp",EDGE,"E34.58.0"),sQuery(id+"F0.wireOp",EDGE,"E34.59.0")])]}),"instanceName":"1"});
            transform(context, id + "F4", {"entities" : qUnion([Q0]), "transformType" : TransformType.TRANSLATION_3D, "dx" : 0 * mm, "dy" : 0 * mm, "dz" : 0 * mm, "makeCopy" : false});
        }
        {
            var Q0;
            Q0=makeQuery(id+"F1.opExtrude","CAP_EDGE",EDGE,{"disambiguationData":[OSD([sQuery(id+"F0.wireOp",EDGE,"E8")])],"isStart":false});
            var Q1;
            Q1=makeQuery(id+"F3.opPattern","COPY",FACE,{"derivedFrom":makeQuery(id+"F1.opExtrude","CAP_FACE",FACE,{"disambiguationData":[OSD([sQuery(id+"F0.wireOp",EDGE,"E0"),sQuery(id+"F0.wireOp",EDGE,"E1"),sQuery(id+"F0.wireOp",EDGE,"E2"),sQuery(id+"F0.wireOp",EDGE,"E3"),sQuery(id+"F0.wireOp",EDGE,"E4.MirrorCS"),sQuery(id+"F0.wireOp",EDGE,"E5.MirrorCS"),sQuery(id+"F0.wireOp",EDGE,"E6.MirrorCS"),sQuery(id+"F0.wireOp",EDGE,"E7.1.0"),sQuery(id+"F0.wireOp",EDGE,"E7.1.1"),sQuery(id+"F0.wireOp",EDGE,"E7.1.2"),sQuery(id+"F0.wireOp",EDGE,"E7.1.3"),sQuery(id+"F0.wireOp",EDGE,"E7.1.4"),sQuery(id+"F0.wireOp",EDGE,"E7.1.5"),sQuery(id+"F0.wireOp",EDGE,"E7.2.0"),sQuery(id+"F0.wireOp",EDGE,"E7.2.1"),sQuery(id+"F0.wireOp",EDGE,"E7.2.2"),sQuery(id+"F0.wireOp",EDGE,"E7.2.3"),sQuery(id+"F0.wireOp",EDGE,"E7.2.4"),sQuery(id+"F0.wireOp",EDGE,"E7.2.5"),sQuery(id+"F0.wireOp",EDGE,"E7.3.0"),sQuery(id+"F0.wireOp",EDGE,"E7.3.1"),sQuery(id+"F0.wireOp",EDGE,"E7.3.2"),sQuery(id+"F0.wireOp",EDGE,"E7.3.3"),sQuery(id+"F0.wireOp",EDGE,"E7.3.4"),sQuery(id+"F0.wireOp",EDGE,"E7.3.5"),sQuery(id+"F0.wireOp",EDGE,"E7.4.0"),sQuery(id+"F0.wireOp",EDGE,"E7.4.1"),sQuery(id+"F0.wireOp",EDGE,"E7.4.2"),sQuery(id+"F0.wireOp",EDGE,"E7.4.3"),sQuery(id+"F0.wireOp",EDGE,"E7.4.4"),sQuery(id+"F0.wireOp",EDGE,"E7.4.5"),sQuery(id+"F0.wireOp",EDGE,"E7.5.0"),sQuery(id+"F0.wireOp",EDGE,"E7.5.1"),sQuery(id+"F0.wireOp",EDGE,"E7.5.2"),sQuery(id+"F0.wireOp",EDGE,"E7.5.3"),sQuery(id+"F0.wireOp",EDGE,"E7.5.4"),sQuery(id+"F0.wireOp",EDGE,"E7.5.5"),sQuery(id+"F0.wireOp",EDGE,"E7.6.0"),sQuery(id+"F0.wireOp",EDGE,"E7.6.1"),sQuery(id+"F0.wireOp",EDGE,"E7.6.2"),sQuery(id+"F0.wireOp",EDGE,"E7.6.3"),sQuery(id+"F0.wireOp",EDGE,"E7.6.4"),sQuery(id+"F0.wireOp",EDGE,"E7.6.5"),sQuery(id+"F0.wireOp",EDGE,"E7.7.0"),sQuery(id+"F0.wireOp",EDGE,"E7.7.1"),sQuery(id+"F0.wireOp",EDGE,"E7.7.2"),sQuery(id+"F0.wireOp",EDGE,"E7.7.3"),sQuery(id+"F0.wireOp",EDGE,"E7.7.4"),sQuery(id+"F0.wireOp",EDGE,"E7.7.5"),sQuery(id+"F0.wireOp",EDGE,"E7.8.0"),sQuery(id+"F0.wireOp",EDGE,"E7.8.1"),sQuery(id+"F0.wireOp",EDGE,"E7.8.2"),sQuery(id+"F0.wireOp",EDGE,"E7.8.3"),sQuery(id+"F0.wireOp",EDGE,"E7.8.4"),sQuery(id+"F0.wireOp",EDGE,"E7.8.5"),sQuery(id+"F0.wireOp",EDGE,"E7.9.0"),sQuery(id+"F0.wireOp",EDGE,"E7.9.1"),sQuery(id+"F0.wireOp",EDGE,"E7.9.2"),sQuery(id+"F0.wireOp",EDGE,"E7.9.3"),sQuery(id+"F0.wireOp",EDGE,"E7.9.4"),sQuery(id+"F0.wireOp",EDGE,"E7.9.5"),sQuery(id+"F0.wireOp",EDGE,"E7.10.0"),sQuery(id+"F0.wireOp",EDGE,"E7.10.1"),sQuery(id+"F0.wireOp",EDGE,"E7.10.2"),sQuery(id+"F0.wireOp",EDGE,"E7.10.3"),sQuery(id+"F0.wireOp",EDGE,"E7.10.4"),sQuery(id+"F0.wireOp",EDGE,"E7.10.5"),sQuery(id+"F0.wireOp",EDGE,"E7.11.0"),sQuery(id+"F0.wireOp",EDGE,"E7.11.1"),sQuery(id+"F0.wireOp",EDGE,"E7.11.2"),sQuery(id+"F0.wireOp",EDGE,"E7.11.3"),sQuery(id+"F0.wireOp",EDGE,"E7.11.4"),sQuery(id+"F0.wireOp",EDGE,"E7.11.5"),sQuery(id+"F0.wireOp",EDGE,"E7.12.0"),sQuery(id+"F0.wireOp",EDGE,"E7.12.1"),sQuery(id+"F0.wireOp",EDGE,"E7.12.2"),sQuery(id+"F0.wireOp",EDGE,"E7.12.3"),sQuery(id+"F0.wireOp",EDGE,"E7.12.4"),sQuery(id+"F0.wireOp",EDGE,"E7.12.5"),sQuery(id+"F0.wireOp",EDGE,"E7.13.0"),sQuery(id+"F0.wireOp",EDGE,"E7.13.1"),sQuery(id+"F0.wireOp",EDGE,"E7.13.2"),sQuery(id+"F0.wireOp",EDGE,"E7.13.3"),sQuery(id+"F0.wireOp",EDGE,"E7.13.4"),sQuery(id+"F0.wireOp",EDGE,"E7.13.5"),sQuery(id+"F0.wireOp",EDGE,"E7.14.0"),sQuery(id+"F0.wireOp",EDGE,"E7.14.1"),sQuery(id+"F0.wireOp",EDGE,"E7.14.2"),sQuery(id+"F0.wireOp",EDGE,"E7.14.3"),sQuery(id+"F0.wireOp",EDGE,"E7.14.4"),sQuery(id+"F0.wireOp",EDGE,"E7.14.5"),sQuery(id+"F0.wireOp",EDGE,"E7.15.0"),sQuery(id+"F0.wireOp",EDGE,"E7.15.1"),sQuery(id+"F0.wireOp",EDGE,"E7.15.2"),sQuery(id+"F0.wireOp",EDGE,"E7.15.3"),sQuery(id+"F0.wireOp",EDGE,"E7.15.4"),sQuery(id+"F0.wireOp",EDGE,"E7.15.5"),sQuery(id+"F0.wireOp",EDGE,"E7.16.0"),sQuery(id+"F0.wireOp",EDGE,"E7.16.1"),sQuery(id+"F0.wireOp",EDGE,"E7.16.2"),sQuery(id+"F0.wireOp",EDGE,"E7.16.3"),sQuery(id+"F0.wireOp",EDGE,"E7.16.4"),sQuery(id+"F0.wireOp",EDGE,"E7.16.5"),sQuery(id+"F0.wireOp",EDGE,"E7.17.0"),sQuery(id+"F0.wireOp",EDGE,"E7.17.1"),sQuery(id+"F0.wireOp",EDGE,"E7.17.2"),sQuery(id+"F0.wireOp",EDGE,"E7.17.3"),sQuery(id+"F0.wireOp",EDGE,"E7.17.4"),sQuery(id+"F0.wireOp",EDGE,"E7.17.5"),sQuery(id+"F0.wireOp",EDGE,"E7.18.0"),sQuery(id+"F0.wireOp",EDGE,"E7.18.1"),sQuery(id+"F0.wireOp",EDGE,"E7.18.2"),sQuery(id+"F0.wireOp",EDGE,"E7.18.3"),sQuery(id+"F0.wireOp",EDGE,"E7.18.4"),sQuery(id+"F0.wireOp",EDGE,"E7.18.5"),sQuery(id+"F0.wireOp",EDGE,"E7.19.0"),sQuery(id+"F0.wireOp",EDGE,"E7.19.1"),sQuery(id+"F0.wireOp",EDGE,"E7.19.2"),sQuery(id+"F0.wireOp",EDGE,"E7.19.3"),sQuery(id+"F0.wireOp",EDGE,"E7.19.4"),sQuery(id+"F0.wireOp",EDGE,"E7.19.5"),sQuery(id+"F0.wireOp",EDGE,"E7.20.0"),sQuery(id+"F0.wireOp",EDGE,"E7.20.1"),sQuery(id+"F0.wireOp",EDGE,"E7.20.2"),sQuery(id+"F0.wireOp",EDGE,"E7.20.3"),sQuery(id+"F0.wireOp",EDGE,"E7.20.4"),sQuery(id+"F0.wireOp",EDGE,"E7.20.5"),sQuery(id+"F0.wireOp",EDGE,"E7.21.0"),sQuery(id+"F0.wireOp",EDGE,"E7.21.1"),sQuery(id+"F0.wireOp",EDGE,"E7.21.2"),sQuery(id+"F0.wireOp",EDGE,"E7.21.3"),sQuery(id+"F0.wireOp",EDGE,"E7.21.4"),sQuery(id+"F0.wireOp",EDGE,"E7.21.5"),sQuery(id+"F0.wireOp",EDGE,"E7.22.0"),sQuery(id+"F0.wireOp",EDGE,"E7.22.1"),sQuery(id+"F0.wireOp",EDGE,"E7.22.2"),sQuery(id+"F0.wireOp",EDGE,"E7.22.3"),sQuery(id+"F0.wireOp",EDGE,"E7.22.4"),sQuery(id+"F0.wireOp",EDGE,"E7.22.5"),sQuery(id+"F0.wireOp",EDGE,"E7.23.0"),sQuery(id+"F0.wireOp",EDGE,"E7.23.1"),sQuery(id+"F0.wireOp",EDGE,"E7.23.2"),sQuery(id+"F0.wireOp",EDGE,"E7.23.3"),sQuery(id+"F0.wireOp",EDGE,"E7.23.4"),sQuery(id+"F0.wireOp",EDGE,"E7.23.5"),sQuery(id+"F0.wireOp",EDGE,"E7.24.0"),sQuery(id+"F0.wireOp",EDGE,"E7.24.1"),sQuery(id+"F0.wireOp",EDGE,"E7.24.2"),sQuery(id+"F0.wireOp",EDGE,"E7.24.3"),sQuery(id+"F0.wireOp",EDGE,"E7.24.4"),sQuery(id+"F0.wireOp",EDGE,"E7.24.5"),sQuery(id+"F0.wireOp",EDGE,"E7.25.0"),sQuery(id+"F0.wireOp",EDGE,"E7.25.1"),sQuery(id+"F0.wireOp",EDGE,"E7.25.2"),sQuery(id+"F0.wireOp",EDGE,"E7.25.3"),sQuery(id+"F0.wireOp",EDGE,"E7.25.4"),sQuery(id+"F0.wireOp",EDGE,"E7.25.5"),sQuery(id+"F0.wireOp",EDGE,"E7.26.0"),sQuery(id+"F0.wireOp",EDGE,"E7.26.1"),sQuery(id+"F0.wireOp",EDGE,"E7.26.2"),sQuery(id+"F0.wireOp",EDGE,"E7.26.3"),sQuery(id+"F0.wireOp",EDGE,"E7.26.4"),sQuery(id+"F0.wireOp",EDGE,"E7.26.5"),sQuery(id+"F0.wireOp",EDGE,"E7.27.0"),sQuery(id+"F0.wireOp",EDGE,"E7.27.1"),sQuery(id+"F0.wireOp",EDGE,"E7.27.2"),sQuery(id+"F0.wireOp",EDGE,"E7.27.3"),sQuery(id+"F0.wireOp",EDGE,"E7.27.4"),sQuery(id+"F0.wireOp",EDGE,"E7.27.5"),sQuery(id+"F0.wireOp",EDGE,"E7.28.0"),sQuery(id+"F0.wireOp",EDGE,"E7.28.1"),sQuery(id+"F0.wireOp",EDGE,"E7.28.2"),sQuery(id+"F0.wireOp",EDGE,"E7.28.3"),sQuery(id+"F0.wireOp",EDGE,"E7.28.4"),sQuery(id+"F0.wireOp",EDGE,"E7.28.5"),sQuery(id+"F0.wireOp",EDGE,"E7.29.0"),sQuery(id+"F0.wireOp",EDGE,"E7.29.1"),sQuery(id+"F0.wireOp",EDGE,"E7.29.2"),sQuery(id+"F0.wireOp",EDGE,"E7.29.3"),sQuery(id+"F0.wireOp",EDGE,"E7.29.4"),sQuery(id+"F0.wireOp",EDGE,"E7.29.5"),sQuery(id+"F0.wireOp",EDGE,"E7.30.0"),sQuery(id+"F0.wireOp",EDGE,"E7.30.1"),sQuery(id+"F0.wireOp",EDGE,"E7.30.2"),sQuery(id+"F0.wireOp",EDGE,"E7.30.3"),sQuery(id+"F0.wireOp",EDGE,"E7.30.4"),sQuery(id+"F0.wireOp",EDGE,"E7.30.5"),sQuery(id+"F0.wireOp",EDGE,"E7.31.0"),sQuery(id+"F0.wireOp",EDGE,"E7.31.1"),sQuery(id+"F0.wireOp",EDGE,"E7.31.2"),sQuery(id+"F0.wireOp",EDGE,"E7.31.3"),sQuery(id+"F0.wireOp",EDGE,"E7.31.4"),sQuery(id+"F0.wireOp",EDGE,"E7.31.5"),sQuery(id+"F0.wireOp",EDGE,"E7.32.0"),sQuery(id+"F0.wireOp",EDGE,"E7.32.1"),sQuery(id+"F0.wireOp",EDGE,"E7.32.2"),sQuery(id+"F0.wireOp",EDGE,"E7.32.3"),sQuery(id+"F0.wireOp",EDGE,"E7.32.4"),sQuery(id+"F0.wireOp",EDGE,"E7.32.5"),sQuery(id+"F0.wireOp",EDGE,"E7.33.0"),sQuery(id+"F0.wireOp",EDGE,"E7.33.1"),sQuery(id+"F0.wireOp",EDGE,"E7.33.2"),sQuery(id+"F0.wireOp",EDGE,"E7.33.3"),sQuery(id+"F0.wireOp",EDGE,"E7.33.4"),sQuery(id+"F0.wireOp",EDGE,"E7.33.5"),sQuery(id+"F0.wireOp",EDGE,"E7.34.0"),sQuery(id+"F0.wireOp",EDGE,"E7.34.1"),sQuery(id+"F0.wireOp",EDGE,"E7.34.2"),sQuery(id+"F0.wireOp",EDGE,"E7.34.3"),sQuery(id+"F0.wireOp",EDGE,"E7.34.4"),sQuery(id+"F0.wireOp",EDGE,"E7.34.5"),sQuery(id+"F0.wireOp",EDGE,"E7.35.0"),sQuery(id+"F0.wireOp",EDGE,"E7.35.1"),sQuery(id+"F0.wireOp",EDGE,"E7.35.2"),sQuery(id+"F0.wireOp",EDGE,"E7.35.3"),sQuery(id+"F0.wireOp",EDGE,"E7.35.4"),sQuery(id+"F0.wireOp",EDGE,"E7.35.5"),sQuery(id+"F0.wireOp",EDGE,"E7.36.0"),sQuery(id+"F0.wireOp",EDGE,"E7.36.1"),sQuery(id+"F0.wireOp",EDGE,"E7.36.2"),sQuery(id+"F0.wireOp",EDGE,"E7.36.3"),sQuery(id+"F0.wireOp",EDGE,"E7.36.4"),sQuery(id+"F0.wireOp",EDGE,"E7.36.5"),sQuery(id+"F0.wireOp",EDGE,"E7.37.0"),sQuery(id+"F0.wireOp",EDGE,"E7.37.1"),sQuery(id+"F0.wireOp",EDGE,"E7.37.2"),sQuery(id+"F0.wireOp",EDGE,"E7.37.3"),sQuery(id+"F0.wireOp",EDGE,"E7.37.4"),sQuery(id+"F0.wireOp",EDGE,"E7.37.5"),sQuery(id+"F0.wireOp",EDGE,"E7.38.0"),sQuery(id+"F0.wireOp",EDGE,"E7.38.1"),sQuery(id+"F0.wireOp",EDGE,"E7.38.2"),sQuery(id+"F0.wireOp",EDGE,"E7.38.3"),sQuery(id+"F0.wireOp",EDGE,"E7.38.4"),sQuery(id+"F0.wireOp",EDGE,"E7.38.5"),sQuery(id+"F0.wireOp",EDGE,"E7.39.0"),sQuery(id+"F0.wireOp",EDGE,"E7.39.1"),sQuery(id+"F0.wireOp",EDGE,"E7.39.2"),sQuery(id+"F0.wireOp",EDGE,"E7.39.3"),sQuery(id+"F0.wireOp",EDGE,"E7.39.4"),sQuery(id+"F0.wireOp",EDGE,"E7.39.5"),sQuery(id+"F0.wireOp",EDGE,"E7.40.0"),sQuery(id+"F0.wireOp",EDGE,"E7.40.1"),sQuery(id+"F0.wireOp",EDGE,"E7.40.2"),sQuery(id+"F0.wireOp",EDGE,"E7.40.3"),sQuery(id+"F0.wireOp",EDGE,"E7.40.4"),sQuery(id+"F0.wireOp",EDGE,"E7.40.5"),sQuery(id+"F0.wireOp",EDGE,"E7.41.0"),sQuery(id+"F0.wireOp",EDGE,"E7.41.1"),sQuery(id+"F0.wireOp",EDGE,"E7.41.2"),sQuery(id+"F0.wireOp",EDGE,"E7.41.3"),sQuery(id+"F0.wireOp",EDGE,"E7.41.4"),sQuery(id+"F0.wireOp",EDGE,"E7.41.5"),sQuery(id+"F0.wireOp",EDGE,"E7.42.0"),sQuery(id+"F0.wireOp",EDGE,"E7.42.1"),sQuery(id+"F0.wireOp",EDGE,"E7.42.2"),sQuery(id+"F0.wireOp",EDGE,"E7.42.3"),sQuery(id+"F0.wireOp",EDGE,"E7.42.4"),sQuery(id+"F0.wireOp",EDGE,"E7.42.5"),sQuery(id+"F0.wireOp",EDGE,"E7.43.0"),sQuery(id+"F0.wireOp",EDGE,"E7.43.1"),sQuery(id+"F0.wireOp",EDGE,"E7.43.2"),sQuery(id+"F0.wireOp",EDGE,"E7.43.3"),sQuery(id+"F0.wireOp",EDGE,"E7.43.4"),sQuery(id+"F0.wireOp",EDGE,"E7.43.5"),sQuery(id+"F0.wireOp",EDGE,"E7.44.0"),sQuery(id+"F0.wireOp",EDGE,"E7.44.1"),sQuery(id+"F0.wireOp",EDGE,"E7.44.2"),sQuery(id+"F0.wireOp",EDGE,"E7.44.3"),sQuery(id+"F0.wireOp",EDGE,"E7.44.4"),sQuery(id+"F0.wireOp",EDGE,"E7.44.5"),sQuery(id+"F0.wireOp",EDGE,"E7.45.0"),sQuery(id+"F0.wireOp",EDGE,"E7.45.1"),sQuery(id+"F0.wireOp",EDGE,"E7.45.2"),sQuery(id+"F0.wireOp",EDGE,"E7.45.3"),sQuery(id+"F0.wireOp",EDGE,"E7.45.4"),sQuery(id+"F0.wireOp",EDGE,"E7.45.5"),sQuery(id+"F0.wireOp",EDGE,"E7.46.0"),sQuery(id+"F0.wireOp",EDGE,"E7.46.1"),sQuery(id+"F0.wireOp",EDGE,"E7.46.2"),sQuery(id+"F0.wireOp",EDGE,"E7.46.3"),sQuery(id+"F0.wireOp",EDGE,"E7.46.4"),sQuery(id+"F0.wireOp",EDGE,"E7.46.5"),sQuery(id+"F0.wireOp",EDGE,"E7.47.0"),sQuery(id+"F0.wireOp",EDGE,"E7.47.1"),sQuery(id+"F0.wireOp",EDGE,"E7.47.2"),sQuery(id+"F0.wireOp",EDGE,"E7.47.3"),sQuery(id+"F0.wireOp",EDGE,"E7.47.4"),sQuery(id+"F0.wireOp",EDGE,"E7.47.5"),sQuery(id+"F0.wireOp",EDGE,"E7.48.0"),sQuery(id+"F0.wireOp",EDGE,"E7.48.1"),sQuery(id+"F0.wireOp",EDGE,"E7.48.2"),sQuery(id+"F0.wireOp",EDGE,"E7.48.3"),sQuery(id+"F0.wireOp",EDGE,"E7.48.4"),sQuery(id+"F0.wireOp",EDGE,"E7.48.5"),sQuery(id+"F0.wireOp",EDGE,"E7.49.0"),sQuery(id+"F0.wireOp",EDGE,"E7.49.1"),sQuery(id+"F0.wireOp",EDGE,"E7.49.2"),sQuery(id+"F0.wireOp",EDGE,"E7.49.3"),sQuery(id+"F0.wireOp",EDGE,"E7.49.4"),sQuery(id+"F0.wireOp",EDGE,"E7.49.5"),sQuery(id+"F0.wireOp",EDGE,"E7.50.0"),sQuery(id+"F0.wireOp",EDGE,"E7.50.1"),sQuery(id+"F0.wireOp",EDGE,"E7.50.2"),sQuery(id+"F0.wireOp",EDGE,"E7.50.3"),sQuery(id+"F0.wireOp",EDGE,"E7.50.4"),sQuery(id+"F0.wireOp",EDGE,"E7.50.5"),sQuery(id+"F0.wireOp",EDGE,"E7.51.0"),sQuery(id+"F0.wireOp",EDGE,"E7.51.1"),sQuery(id+"F0.wireOp",EDGE,"E7.51.2"),sQuery(id+"F0.wireOp",EDGE,"E7.51.3"),sQuery(id+"F0.wireOp",EDGE,"E7.51.4"),sQuery(id+"F0.wireOp",EDGE,"E7.51.5"),sQuery(id+"F0.wireOp",EDGE,"E7.52.0"),sQuery(id+"F0.wireOp",EDGE,"E7.52.1"),sQuery(id+"F0.wireOp",EDGE,"E7.52.2"),sQuery(id+"F0.wireOp",EDGE,"E7.52.3"),sQuery(id+"F0.wireOp",EDGE,"E7.52.4"),sQuery(id+"F0.wireOp",EDGE,"E7.52.5"),sQuery(id+"F0.wireOp",EDGE,"E7.53.0"),sQuery(id+"F0.wireOp",EDGE,"E7.53.1"),sQuery(id+"F0.wireOp",EDGE,"E7.53.2"),sQuery(id+"F0.wireOp",EDGE,"E7.53.3"),sQuery(id+"F0.wireOp",EDGE,"E7.53.4"),sQuery(id+"F0.wireOp",EDGE,"E7.53.5"),sQuery(id+"F0.wireOp",EDGE,"E7.54.0"),sQuery(id+"F0.wireOp",EDGE,"E7.54.1"),sQuery(id+"F0.wireOp",EDGE,"E7.54.2"),sQuery(id+"F0.wireOp",EDGE,"E7.54.3"),sQuery(id+"F0.wireOp",EDGE,"E7.54.4"),sQuery(id+"F0.wireOp",EDGE,"E7.54.5"),sQuery(id+"F0.wireOp",EDGE,"E7.55.0"),sQuery(id+"F0.wireOp",EDGE,"E7.55.1"),sQuery(id+"F0.wireOp",EDGE,"E7.55.2"),sQuery(id+"F0.wireOp",EDGE,"E7.55.3"),sQuery(id+"F0.wireOp",EDGE,"E7.55.4"),sQuery(id+"F0.wireOp",EDGE,"E7.55.5"),sQuery(id+"F0.wireOp",EDGE,"E7.56.0"),sQuery(id+"F0.wireOp",EDGE,"E7.56.1"),sQuery(id+"F0.wireOp",EDGE,"E7.56.2"),sQuery(id+"F0.wireOp",EDGE,"E7.56.3"),sQuery(id+"F0.wireOp",EDGE,"E7.56.4"),sQuery(id+"F0.wireOp",EDGE,"E7.56.5"),sQuery(id+"F0.wireOp",EDGE,"E7.57.0"),sQuery(id+"F0.wireOp",EDGE,"E7.57.1"),sQuery(id+"F0.wireOp",EDGE,"E7.57.2"),sQuery(id+"F0.wireOp",EDGE,"E7.57.3"),sQuery(id+"F0.wireOp",EDGE,"E7.57.4"),sQuery(id+"F0.wireOp",EDGE,"E7.57.5"),sQuery(id+"F0.wireOp",EDGE,"E7.58.0"),sQuery(id+"F0.wireOp",EDGE,"E7.58.1"),sQuery(id+"F0.wireOp",EDGE,"E7.58.2"),sQuery(id+"F0.wireOp",EDGE,"E7.58.3"),sQuery(id+"F0.wireOp",EDGE,"E7.58.4"),sQuery(id+"F0.wireOp",EDGE,"E7.58.5"),sQuery(id+"F0.wireOp",EDGE,"E7.59.0"),sQuery(id+"F0.wireOp",EDGE,"E7.59.1"),sQuery(id+"F0.wireOp",EDGE,"E7.59.2"),sQuery(id+"F0.wireOp",EDGE,"E7.59.3"),sQuery(id+"F0.wireOp",EDGE,"E7.59.4"),sQuery(id+"F0.wireOp",EDGE,"E7.59.5"),sQuery(id+"F0.wireOp",EDGE,"E8"),sQuery(id+"F0.wireOp",EDGE,"E9"),sQuery(id+"F0.wireOp",EDGE,"E10"),sQuery(id+"F0.wireOp",EDGE,"E11.filletArc"),sQuery(id+"F0.wireOp",EDGE,"E12.filletArc"),sQuery(id+"F0.wireOp",EDGE,"E13.filletArc"),sQuery(id+"F0.wireOp",EDGE,"E14.MirrorCS"),sQuery(id+"F0.wireOp",EDGE,"E15.MirrorCS"),sQuery(id+"F0.wireOp",EDGE,"E16.MirrorCS"),sQuery(id+"F0.wireOp",EDGE,"E17.MirrorCS"),sQuery(id+"F0.wireOp",EDGE,"E18.MirrorCS"),sQuery(id+"F0.wireOp",EDGE,"E19.MirrorCS"),sQuery(id+"F0.wireOp",EDGE,"E21.MirrorCS"),sQuery(id+"F0.wireOp",EDGE,"E22.MirrorCS"),sQuery(id+"F0.wireOp",EDGE,"E23.MirrorCS"),sQuery(id+"F0.wireOp",EDGE,"E24.MirrorCS"),sQuery(id+"F0.wireOp",EDGE,"E25.MirrorCS"),sQuery(id+"F0.wireOp",EDGE,"E20.MirrorCS"),sQuery(id+"F0.wireOp",EDGE,"E27.MirrorCS"),sQuery(id+"F0.wireOp",EDGE,"E28.MirrorCS"),sQuery(id+"F0.wireOp",EDGE,"E29.MirrorCS"),sQuery(id+"F0.wireOp",EDGE,"E30.MirrorCS"),sQuery(id+"F0.wireOp",EDGE,"E31.MirrorCS"),sQuery(id+"F0.wireOp",EDGE,"E32.MirrorCS"),sQuery(id+"F0.wireOp",EDGE,"E33"),sQuery(id+"F0.wireOp",EDGE,"E34.1.0"),sQuery(id+"F0.wireOp",EDGE,"E34.2.0"),sQuery(id+"F0.wireOp",EDGE,"E34.3.0"),sQuery(id+"F0.wireOp",EDGE,"E34.4.0"),sQuery(id+"F0.wireOp",EDGE,"E34.5.0"),sQuery(id+"F0.wireOp",EDGE,"E34.6.0"),sQuery(id+"F0.wireOp",EDGE,"E34.7.0"),sQuery(id+"F0.wireOp",EDGE,"E34.8.0"),sQuery(id+"F0.wireOp",EDGE,"E34.9.0"),sQuery(id+"F0.wireOp",EDGE,"E34.10.0"),sQuery(id+"F0.wireOp",EDGE,"E34.11.0"),sQuery(id+"F0.wireOp",EDGE,"E34.12.0"),sQuery(id+"F0.wireOp",EDGE,"E34.13.0"),sQuery(id+"F0.wireOp",EDGE,"E34.14.0"),sQuery(id+"F0.wireOp",EDGE,"E34.15.0"),sQuery(id+"F0.wireOp",EDGE,"E34.16.0"),sQuery(id+"F0.wireOp",EDGE,"E34.17.0"),sQuery(id+"F0.wireOp",EDGE,"E34.18.0"),sQuery(id+"F0.wireOp",EDGE,"E34.19.0"),sQuery(id+"F0.wireOp",EDGE,"E34.20.0"),sQuery(id+"F0.wireOp",EDGE,"E34.21.0"),sQuery(id+"F0.wireOp",EDGE,"E34.22.0"),sQuery(id+"F0.wireOp",EDGE,"E34.23.0"),sQuery(id+"F0.wireOp",EDGE,"E34.24.0"),sQuery(id+"F0.wireOp",EDGE,"E34.25.0"),sQuery(id+"F0.wireOp",EDGE,"E34.26.0"),sQuery(id+"F0.wireOp",EDGE,"E34.27.0"),sQuery(id+"F0.wireOp",EDGE,"E34.28.0"),sQuery(id+"F0.wireOp",EDGE,"E34.29.0"),sQuery(id+"F0.wireOp",EDGE,"E34.30.0"),sQuery(id+"F0.wireOp",EDGE,"E34.31.0"),sQuery(id+"F0.wireOp",EDGE,"E34.32.0"),sQuery(id+"F0.wireOp",EDGE,"E34.33.0"),sQuery(id+"F0.wireOp",EDGE,"E34.34.0"),sQuery(id+"F0.wireOp",EDGE,"E34.35.0"),sQuery(id+"F0.wireOp",EDGE,"E34.36.0"),sQuery(id+"F0.wireOp",EDGE,"E34.37.0"),sQuery(id+"F0.wireOp",EDGE,"E34.38.0"),sQuery(id+"F0.wireOp",EDGE,"E34.39.0"),sQuery(id+"F0.wireOp",EDGE,"E34.40.0"),sQuery(id+"F0.wireOp",EDGE,"E34.41.0"),sQuery(id+"F0.wireOp",EDGE,"E34.42.0"),sQuery(id+"F0.wireOp",EDGE,"E34.43.0"),sQuery(id+"F0.wireOp",EDGE,"E34.44.0"),sQuery(id+"F0.wireOp",EDGE,"E34.45.0"),sQuery(id+"F0.wireOp",EDGE,"E34.46.0"),sQuery(id+"F0.wireOp",EDGE,"E34.47.0"),sQuery(id+"F0.wireOp",EDGE,"E34.48.0"),sQuery(id+"F0.wireOp",EDGE,"E34.49.0"),sQuery(id+"F0.wireOp",EDGE,"E34.50.0"),sQuery(id+"F0.wireOp",EDGE,"E34.51.0"),sQuery(id+"F0.wireOp",EDGE,"E34.52.0"),sQuery(id+"F0.wireOp",EDGE,"E34.53.0"),sQuery(id+"F0.wireOp",EDGE,"E34.54.0"),sQuery(id+"F0.wireOp",EDGE,"E34.55.0"),sQuery(id+"F0.wireOp",EDGE,"E34.56.0"),sQuery(id+"F0.wireOp",EDGE,"E34.57.0"),sQuery(id+"F0.wireOp",EDGE,"E34.58.0"),sQuery(id+"F0.wireOp",EDGE,"E34.59.0")])],"isStart":false}),"instanceName":"1"});
            var Q2;
            Q2=makeQuery(id+"F1.opExtrude","CAP_FACE",FACE,{"disambiguationData":[OSD([sQuery(id+"F0.wireOp",EDGE,"E0"),sQuery(id+"F0.wireOp",EDGE,"E1"),sQuery(id+"F0.wireOp",EDGE,"E2"),sQuery(id+"F0.wireOp",EDGE,"E3"),sQuery(id+"F0.wireOp",EDGE,"E4.MirrorCS"),sQuery(id+"F0.wireOp",EDGE,"E5.MirrorCS"),sQuery(id+"F0.wireOp",EDGE,"E6.MirrorCS"),sQuery(id+"F0.wireOp",EDGE,"E7.1.0"),sQuery(id+"F0.wireOp",EDGE,"E7.1.1"),sQuery(id+"F0.wireOp",EDGE,"E7.1.2"),sQuery(id+"F0.wireOp",EDGE,"E7.1.3"),sQuery(id+"F0.wireOp",EDGE,"E7.1.4"),sQuery(id+"F0.wireOp",EDGE,"E7.1.5"),sQuery(id+"F0.wireOp",EDGE,"E7.2.0"),sQuery(id+"F0.wireOp",EDGE,"E7.2.1"),sQuery(id+"F0.wireOp",EDGE,"E7.2.2"),sQuery(id+"F0.wireOp",EDGE,"E7.2.3"),sQuery(id+"F0.wireOp",EDGE,"E7.2.4"),sQuery(id+"F0.wireOp",EDGE,"E7.2.5"),sQuery(id+"F0.wireOp",EDGE,"E7.3.0"),sQuery(id+"F0.wireOp",EDGE,"E7.3.1"),sQuery(id+"F0.wireOp",EDGE,"E7.3.2"),sQuery(id+"F0.wireOp",EDGE,"E7.3.3"),sQuery(id+"F0.wireOp",EDGE,"E7.3.4"),sQuery(id+"F0.wireOp",EDGE,"E7.3.5"),sQuery(id+"F0.wireOp",EDGE,"E7.4.0"),sQuery(id+"F0.wireOp",EDGE,"E7.4.1"),sQuery(id+"F0.wireOp",EDGE,"E7.4.2"),sQuery(id+"F0.wireOp",EDGE,"E7.4.3"),sQuery(id+"F0.wireOp",EDGE,"E7.4.4"),sQuery(id+"F0.wireOp",EDGE,"E7.4.5"),sQuery(id+"F0.wireOp",EDGE,"E7.5.0"),sQuery(id+"F0.wireOp",EDGE,"E7.5.1"),sQuery(id+"F0.wireOp",EDGE,"E7.5.2"),sQuery(id+"F0.wireOp",EDGE,"E7.5.3"),sQuery(id+"F0.wireOp",EDGE,"E7.5.4"),sQuery(id+"F0.wireOp",EDGE,"E7.5.5"),sQuery(id+"F0.wireOp",EDGE,"E7.6.0"),sQuery(id+"F0.wireOp",EDGE,"E7.6.1"),sQuery(id+"F0.wireOp",EDGE,"E7.6.2"),sQuery(id+"F0.wireOp",EDGE,"E7.6.3"),sQuery(id+"F0.wireOp",EDGE,"E7.6.4"),sQuery(id+"F0.wireOp",EDGE,"E7.6.5"),sQuery(id+"F0.wireOp",EDGE,"E7.7.0"),sQuery(id+"F0.wireOp",EDGE,"E7.7.1"),sQuery(id+"F0.wireOp",EDGE,"E7.7.2"),sQuery(id+"F0.wireOp",EDGE,"E7.7.3"),sQuery(id+"F0.wireOp",EDGE,"E7.7.4"),sQuery(id+"F0.wireOp",EDGE,"E7.7.5"),sQuery(id+"F0.wireOp",EDGE,"E7.8.0"),sQuery(id+"F0.wireOp",EDGE,"E7.8.1"),sQuery(id+"F0.wireOp",EDGE,"E7.8.2"),sQuery(id+"F0.wireOp",EDGE,"E7.8.3"),sQuery(id+"F0.wireOp",EDGE,"E7.8.4"),sQuery(id+"F0.wireOp",EDGE,"E7.8.5"),sQuery(id+"F0.wireOp",EDGE,"E7.9.0"),sQuery(id+"F0.wireOp",EDGE,"E7.9.1"),sQuery(id+"F0.wireOp",EDGE,"E7.9.2"),sQuery(id+"F0.wireOp",EDGE,"E7.9.3"),sQuery(id+"F0.wireOp",EDGE,"E7.9.4"),sQuery(id+"F0.wireOp",EDGE,"E7.9.5"),sQuery(id+"F0.wireOp",EDGE,"E7.10.0"),sQuery(id+"F0.wireOp",EDGE,"E7.10.1"),sQuery(id+"F0.wireOp",EDGE,"E7.10.2"),sQuery(id+"F0.wireOp",EDGE,"E7.10.3"),sQuery(id+"F0.wireOp",EDGE,"E7.10.4"),sQuery(id+"F0.wireOp",EDGE,"E7.10.5"),sQuery(id+"F0.wireOp",EDGE,"E7.11.0"),sQuery(id+"F0.wireOp",EDGE,"E7.11.1"),sQuery(id+"F0.wireOp",EDGE,"E7.11.2"),sQuery(id+"F0.wireOp",EDGE,"E7.11.3"),sQuery(id+"F0.wireOp",EDGE,"E7.11.4"),sQuery(id+"F0.wireOp",EDGE,"E7.11.5"),sQuery(id+"F0.wireOp",EDGE,"E7.12.0"),sQuery(id+"F0.wireOp",EDGE,"E7.12.1"),sQuery(id+"F0.wireOp",EDGE,"E7.12.2"),sQuery(id+"F0.wireOp",EDGE,"E7.12.3"),sQuery(id+"F0.wireOp",EDGE,"E7.12.4"),sQuery(id+"F0.wireOp",EDGE,"E7.12.5"),sQuery(id+"F0.wireOp",EDGE,"E7.13.0"),sQuery(id+"F0.wireOp",EDGE,"E7.13.1"),sQuery(id+"F0.wireOp",EDGE,"E7.13.2"),sQuery(id+"F0.wireOp",EDGE,"E7.13.3"),sQuery(id+"F0.wireOp",EDGE,"E7.13.4"),sQuery(id+"F0.wireOp",EDGE,"E7.13.5"),sQuery(id+"F0.wireOp",EDGE,"E7.14.0"),sQuery(id+"F0.wireOp",EDGE,"E7.14.1"),sQuery(id+"F0.wireOp",EDGE,"E7.14.2"),sQuery(id+"F0.wireOp",EDGE,"E7.14.3"),sQuery(id+"F0.wireOp",EDGE,"E7.14.4"),sQuery(id+"F0.wireOp",EDGE,"E7.14.5"),sQuery(id+"F0.wireOp",EDGE,"E7.15.0"),sQuery(id+"F0.wireOp",EDGE,"E7.15.1"),sQuery(id+"F0.wireOp",EDGE,"E7.15.2"),sQuery(id+"F0.wireOp",EDGE,"E7.15.3"),sQuery(id+"F0.wireOp",EDGE,"E7.15.4"),sQuery(id+"F0.wireOp",EDGE,"E7.15.5"),sQuery(id+"F0.wireOp",EDGE,"E7.16.0"),sQuery(id+"F0.wireOp",EDGE,"E7.16.1"),sQuery(id+"F0.wireOp",EDGE,"E7.16.2"),sQuery(id+"F0.wireOp",EDGE,"E7.16.3"),sQuery(id+"F0.wireOp",EDGE,"E7.16.4"),sQuery(id+"F0.wireOp",EDGE,"E7.16.5"),sQuery(id+"F0.wireOp",EDGE,"E7.17.0"),sQuery(id+"F0.wireOp",EDGE,"E7.17.1"),sQuery(id+"F0.wireOp",EDGE,"E7.17.2"),sQuery(id+"F0.wireOp",EDGE,"E7.17.3"),sQuery(id+"F0.wireOp",EDGE,"E7.17.4"),sQuery(id+"F0.wireOp",EDGE,"E7.17.5"),sQuery(id+"F0.wireOp",EDGE,"E7.18.0"),sQuery(id+"F0.wireOp",EDGE,"E7.18.1"),sQuery(id+"F0.wireOp",EDGE,"E7.18.2"),sQuery(id+"F0.wireOp",EDGE,"E7.18.3"),sQuery(id+"F0.wireOp",EDGE,"E7.18.4"),sQuery(id+"F0.wireOp",EDGE,"E7.18.5"),sQuery(id+"F0.wireOp",EDGE,"E7.19.0"),sQuery(id+"F0.wireOp",EDGE,"E7.19.1"),sQuery(id+"F0.wireOp",EDGE,"E7.19.2"),sQuery(id+"F0.wireOp",EDGE,"E7.19.3"),sQuery(id+"F0.wireOp",EDGE,"E7.19.4"),sQuery(id+"F0.wireOp",EDGE,"E7.19.5"),sQuery(id+"F0.wireOp",EDGE,"E7.20.0"),sQuery(id+"F0.wireOp",EDGE,"E7.20.1"),sQuery(id+"F0.wireOp",EDGE,"E7.20.2"),sQuery(id+"F0.wireOp",EDGE,"E7.20.3"),sQuery(id+"F0.wireOp",EDGE,"E7.20.4"),sQuery(id+"F0.wireOp",EDGE,"E7.20.5"),sQuery(id+"F0.wireOp",EDGE,"E7.21.0"),sQuery(id+"F0.wireOp",EDGE,"E7.21.1"),sQuery(id+"F0.wireOp",EDGE,"E7.21.2"),sQuery(id+"F0.wireOp",EDGE,"E7.21.3"),sQuery(id+"F0.wireOp",EDGE,"E7.21.4"),sQuery(id+"F0.wireOp",EDGE,"E7.21.5"),sQuery(id+"F0.wireOp",EDGE,"E7.22.0"),sQuery(id+"F0.wireOp",EDGE,"E7.22.1"),sQuery(id+"F0.wireOp",EDGE,"E7.22.2"),sQuery(id+"F0.wireOp",EDGE,"E7.22.3"),sQuery(id+"F0.wireOp",EDGE,"E7.22.4"),sQuery(id+"F0.wireOp",EDGE,"E7.22.5"),sQuery(id+"F0.wireOp",EDGE,"E7.23.0"),sQuery(id+"F0.wireOp",EDGE,"E7.23.1"),sQuery(id+"F0.wireOp",EDGE,"E7.23.2"),sQuery(id+"F0.wireOp",EDGE,"E7.23.3"),sQuery(id+"F0.wireOp",EDGE,"E7.23.4"),sQuery(id+"F0.wireOp",EDGE,"E7.23.5"),sQuery(id+"F0.wireOp",EDGE,"E7.24.0"),sQuery(id+"F0.wireOp",EDGE,"E7.24.1"),sQuery(id+"F0.wireOp",EDGE,"E7.24.2"),sQuery(id+"F0.wireOp",EDGE,"E7.24.3"),sQuery(id+"F0.wireOp",EDGE,"E7.24.4"),sQuery(id+"F0.wireOp",EDGE,"E7.24.5"),sQuery(id+"F0.wireOp",EDGE,"E7.25.0"),sQuery(id+"F0.wireOp",EDGE,"E7.25.1"),sQuery(id+"F0.wireOp",EDGE,"E7.25.2"),sQuery(id+"F0.wireOp",EDGE,"E7.25.3"),sQuery(id+"F0.wireOp",EDGE,"E7.25.4"),sQuery(id+"F0.wireOp",EDGE,"E7.25.5"),sQuery(id+"F0.wireOp",EDGE,"E7.26.0"),sQuery(id+"F0.wireOp",EDGE,"E7.26.1"),sQuery(id+"F0.wireOp",EDGE,"E7.26.2"),sQuery(id+"F0.wireOp",EDGE,"E7.26.3"),sQuery(id+"F0.wireOp",EDGE,"E7.26.4"),sQuery(id+"F0.wireOp",EDGE,"E7.26.5"),sQuery(id+"F0.wireOp",EDGE,"E7.27.0"),sQuery(id+"F0.wireOp",EDGE,"E7.27.1"),sQuery(id+"F0.wireOp",EDGE,"E7.27.2"),sQuery(id+"F0.wireOp",EDGE,"E7.27.3"),sQuery(id+"F0.wireOp",EDGE,"E7.27.4"),sQuery(id+"F0.wireOp",EDGE,"E7.27.5"),sQuery(id+"F0.wireOp",EDGE,"E7.28.0"),sQuery(id+"F0.wireOp",EDGE,"E7.28.1"),sQuery(id+"F0.wireOp",EDGE,"E7.28.2"),sQuery(id+"F0.wireOp",EDGE,"E7.28.3"),sQuery(id+"F0.wireOp",EDGE,"E7.28.4"),sQuery(id+"F0.wireOp",EDGE,"E7.28.5"),sQuery(id+"F0.wireOp",EDGE,"E7.29.0"),sQuery(id+"F0.wireOp",EDGE,"E7.29.1"),sQuery(id+"F0.wireOp",EDGE,"E7.29.2"),sQuery(id+"F0.wireOp",EDGE,"E7.29.3"),sQuery(id+"F0.wireOp",EDGE,"E7.29.4"),sQuery(id+"F0.wireOp",EDGE,"E7.29.5"),sQuery(id+"F0.wireOp",EDGE,"E7.30.0"),sQuery(id+"F0.wireOp",EDGE,"E7.30.1"),sQuery(id+"F0.wireOp",EDGE,"E7.30.2"),sQuery(id+"F0.wireOp",EDGE,"E7.30.3"),sQuery(id+"F0.wireOp",EDGE,"E7.30.4"),sQuery(id+"F0.wireOp",EDGE,"E7.30.5"),sQuery(id+"F0.wireOp",EDGE,"E7.31.0"),sQuery(id+"F0.wireOp",EDGE,"E7.31.1"),sQuery(id+"F0.wireOp",EDGE,"E7.31.2"),sQuery(id+"F0.wireOp",EDGE,"E7.31.3"),sQuery(id+"F0.wireOp",EDGE,"E7.31.4"),sQuery(id+"F0.wireOp",EDGE,"E7.31.5"),sQuery(id+"F0.wireOp",EDGE,"E7.32.0"),sQuery(id+"F0.wireOp",EDGE,"E7.32.1"),sQuery(id+"F0.wireOp",EDGE,"E7.32.2"),sQuery(id+"F0.wireOp",EDGE,"E7.32.3"),sQuery(id+"F0.wireOp",EDGE,"E7.32.4"),sQuery(id+"F0.wireOp",EDGE,"E7.32.5"),sQuery(id+"F0.wireOp",EDGE,"E7.33.0"),sQuery(id+"F0.wireOp",EDGE,"E7.33.1"),sQuery(id+"F0.wireOp",EDGE,"E7.33.2"),sQuery(id+"F0.wireOp",EDGE,"E7.33.3"),sQuery(id+"F0.wireOp",EDGE,"E7.33.4"),sQuery(id+"F0.wireOp",EDGE,"E7.33.5"),sQuery(id+"F0.wireOp",EDGE,"E7.34.0"),sQuery(id+"F0.wireOp",EDGE,"E7.34.1"),sQuery(id+"F0.wireOp",EDGE,"E7.34.2"),sQuery(id+"F0.wireOp",EDGE,"E7.34.3"),sQuery(id+"F0.wireOp",EDGE,"E7.34.4"),sQuery(id+"F0.wireOp",EDGE,"E7.34.5"),sQuery(id+"F0.wireOp",EDGE,"E7.35.0"),sQuery(id+"F0.wireOp",EDGE,"E7.35.1"),sQuery(id+"F0.wireOp",EDGE,"E7.35.2"),sQuery(id+"F0.wireOp",EDGE,"E7.35.3"),sQuery(id+"F0.wireOp",EDGE,"E7.35.4"),sQuery(id+"F0.wireOp",EDGE,"E7.35.5"),sQuery(id+"F0.wireOp",EDGE,"E7.36.0"),sQuery(id+"F0.wireOp",EDGE,"E7.36.1"),sQuery(id+"F0.wireOp",EDGE,"E7.36.2"),sQuery(id+"F0.wireOp",EDGE,"E7.36.3"),sQuery(id+"F0.wireOp",EDGE,"E7.36.4"),sQuery(id+"F0.wireOp",EDGE,"E7.36.5"),sQuery(id+"F0.wireOp",EDGE,"E7.37.0"),sQuery(id+"F0.wireOp",EDGE,"E7.37.1"),sQuery(id+"F0.wireOp",EDGE,"E7.37.2"),sQuery(id+"F0.wireOp",EDGE,"E7.37.3"),sQuery(id+"F0.wireOp",EDGE,"E7.37.4"),sQuery(id+"F0.wireOp",EDGE,"E7.37.5"),sQuery(id+"F0.wireOp",EDGE,"E7.38.0"),sQuery(id+"F0.wireOp",EDGE,"E7.38.1"),sQuery(id+"F0.wireOp",EDGE,"E7.38.2"),sQuery(id+"F0.wireOp",EDGE,"E7.38.3"),sQuery(id+"F0.wireOp",EDGE,"E7.38.4"),sQuery(id+"F0.wireOp",EDGE,"E7.38.5"),sQuery(id+"F0.wireOp",EDGE,"E7.39.0"),sQuery(id+"F0.wireOp",EDGE,"E7.39.1"),sQuery(id+"F0.wireOp",EDGE,"E7.39.2"),sQuery(id+"F0.wireOp",EDGE,"E7.39.3"),sQuery(id+"F0.wireOp",EDGE,"E7.39.4"),sQuery(id+"F0.wireOp",EDGE,"E7.39.5"),sQuery(id+"F0.wireOp",EDGE,"E7.40.0"),sQuery(id+"F0.wireOp",EDGE,"E7.40.1"),sQuery(id+"F0.wireOp",EDGE,"E7.40.2"),sQuery(id+"F0.wireOp",EDGE,"E7.40.3"),sQuery(id+"F0.wireOp",EDGE,"E7.40.4"),sQuery(id+"F0.wireOp",EDGE,"E7.40.5"),sQuery(id+"F0.wireOp",EDGE,"E7.41.0"),sQuery(id+"F0.wireOp",EDGE,"E7.41.1"),sQuery(id+"F0.wireOp",EDGE,"E7.41.2"),sQuery(id+"F0.wireOp",EDGE,"E7.41.3"),sQuery(id+"F0.wireOp",EDGE,"E7.41.4"),sQuery(id+"F0.wireOp",EDGE,"E7.41.5"),sQuery(id+"F0.wireOp",EDGE,"E7.42.0"),sQuery(id+"F0.wireOp",EDGE,"E7.42.1"),sQuery(id+"F0.wireOp",EDGE,"E7.42.2"),sQuery(id+"F0.wireOp",EDGE,"E7.42.3"),sQuery(id+"F0.wireOp",EDGE,"E7.42.4"),sQuery(id+"F0.wireOp",EDGE,"E7.42.5"),sQuery(id+"F0.wireOp",EDGE,"E7.43.0"),sQuery(id+"F0.wireOp",EDGE,"E7.43.1"),sQuery(id+"F0.wireOp",EDGE,"E7.43.2"),sQuery(id+"F0.wireOp",EDGE,"E7.43.3"),sQuery(id+"F0.wireOp",EDGE,"E7.43.4"),sQuery(id+"F0.wireOp",EDGE,"E7.43.5"),sQuery(id+"F0.wireOp",EDGE,"E7.44.0"),sQuery(id+"F0.wireOp",EDGE,"E7.44.1"),sQuery(id+"F0.wireOp",EDGE,"E7.44.2"),sQuery(id+"F0.wireOp",EDGE,"E7.44.3"),sQuery(id+"F0.wireOp",EDGE,"E7.44.4"),sQuery(id+"F0.wireOp",EDGE,"E7.44.5"),sQuery(id+"F0.wireOp",EDGE,"E7.45.0"),sQuery(id+"F0.wireOp",EDGE,"E7.45.1"),sQuery(id+"F0.wireOp",EDGE,"E7.45.2"),sQuery(id+"F0.wireOp",EDGE,"E7.45.3"),sQuery(id+"F0.wireOp",EDGE,"E7.45.4"),sQuery(id+"F0.wireOp",EDGE,"E7.45.5"),sQuery(id+"F0.wireOp",EDGE,"E7.46.0"),sQuery(id+"F0.wireOp",EDGE,"E7.46.1"),sQuery(id+"F0.wireOp",EDGE,"E7.46.2"),sQuery(id+"F0.wireOp",EDGE,"E7.46.3"),sQuery(id+"F0.wireOp",EDGE,"E7.46.4"),sQuery(id+"F0.wireOp",EDGE,"E7.46.5"),sQuery(id+"F0.wireOp",EDGE,"E7.47.0"),sQuery(id+"F0.wireOp",EDGE,"E7.47.1"),sQuery(id+"F0.wireOp",EDGE,"E7.47.2"),sQuery(id+"F0.wireOp",EDGE,"E7.47.3"),sQuery(id+"F0.wireOp",EDGE,"E7.47.4"),sQuery(id+"F0.wireOp",EDGE,"E7.47.5"),sQuery(id+"F0.wireOp",EDGE,"E7.48.0"),sQuery(id+"F0.wireOp",EDGE,"E7.48.1"),sQuery(id+"F0.wireOp",EDGE,"E7.48.2"),sQuery(id+"F0.wireOp",EDGE,"E7.48.3"),sQuery(id+"F0.wireOp",EDGE,"E7.48.4"),sQuery(id+"F0.wireOp",EDGE,"E7.48.5"),sQuery(id+"F0.wireOp",EDGE,"E7.49.0"),sQuery(id+"F0.wireOp",EDGE,"E7.49.1"),sQuery(id+"F0.wireOp",EDGE,"E7.49.2"),sQuery(id+"F0.wireOp",EDGE,"E7.49.3"),sQuery(id+"F0.wireOp",EDGE,"E7.49.4"),sQuery(id+"F0.wireOp",EDGE,"E7.49.5"),sQuery(id+"F0.wireOp",EDGE,"E7.50.0"),sQuery(id+"F0.wireOp",EDGE,"E7.50.1"),sQuery(id+"F0.wireOp",EDGE,"E7.50.2"),sQuery(id+"F0.wireOp",EDGE,"E7.50.3"),sQuery(id+"F0.wireOp",EDGE,"E7.50.4"),sQuery(id+"F0.wireOp",EDGE,"E7.50.5"),sQuery(id+"F0.wireOp",EDGE,"E7.51.0"),sQuery(id+"F0.wireOp",EDGE,"E7.51.1"),sQuery(id+"F0.wireOp",EDGE,"E7.51.2"),sQuery(id+"F0.wireOp",EDGE,"E7.51.3"),sQuery(id+"F0.wireOp",EDGE,"E7.51.4"),sQuery(id+"F0.wireOp",EDGE,"E7.51.5"),sQuery(id+"F0.wireOp",EDGE,"E7.52.0"),sQuery(id+"F0.wireOp",EDGE,"E7.52.1"),sQuery(id+"F0.wireOp",EDGE,"E7.52.2"),sQuery(id+"F0.wireOp",EDGE,"E7.52.3"),sQuery(id+"F0.wireOp",EDGE,"E7.52.4"),sQuery(id+"F0.wireOp",EDGE,"E7.52.5"),sQuery(id+"F0.wireOp",EDGE,"E7.53.0"),sQuery(id+"F0.wireOp",EDGE,"E7.53.1"),sQuery(id+"F0.wireOp",EDGE,"E7.53.2"),sQuery(id+"F0.wireOp",EDGE,"E7.53.3"),sQuery(id+"F0.wireOp",EDGE,"E7.53.4"),sQuery(id+"F0.wireOp",EDGE,"E7.53.5"),sQuery(id+"F0.wireOp",EDGE,"E7.54.0"),sQuery(id+"F0.wireOp",EDGE,"E7.54.1"),sQuery(id+"F0.wireOp",EDGE,"E7.54.2"),sQuery(id+"F0.wireOp",EDGE,"E7.54.3"),sQuery(id+"F0.wireOp",EDGE,"E7.54.4"),sQuery(id+"F0.wireOp",EDGE,"E7.54.5"),sQuery(id+"F0.wireOp",EDGE,"E7.55.0"),sQuery(id+"F0.wireOp",EDGE,"E7.55.1"),sQuery(id+"F0.wireOp",EDGE,"E7.55.2"),sQuery(id+"F0.wireOp",EDGE,"E7.55.3"),sQuery(id+"F0.wireOp",EDGE,"E7.55.4"),sQuery(id+"F0.wireOp",EDGE,"E7.55.5"),sQuery(id+"F0.wireOp",EDGE,"E7.56.0"),sQuery(id+"F0.wireOp",EDGE,"E7.56.1"),sQuery(id+"F0.wireOp",EDGE,"E7.56.2"),sQuery(id+"F0.wireOp",EDGE,"E7.56.3"),sQuery(id+"F0.wireOp",EDGE,"E7.56.4"),sQuery(id+"F0.wireOp",EDGE,"E7.56.5"),sQuery(id+"F0.wireOp",EDGE,"E7.57.0"),sQuery(id+"F0.wireOp",EDGE,"E7.57.1"),sQuery(id+"F0.wireOp",EDGE,"E7.57.2"),sQuery(id+"F0.wireOp",EDGE,"E7.57.3"),sQuery(id+"F0.wireOp",EDGE,"E7.57.4"),sQuery(id+"F0.wireOp",EDGE,"E7.57.5"),sQuery(id+"F0.wireOp",EDGE,"E7.58.0"),sQuery(id+"F0.wireOp",EDGE,"E7.58.1"),sQuery(id+"F0.wireOp",EDGE,"E7.58.2"),sQuery(id+"F0.wireOp",EDGE,"E7.58.3"),sQuery(id+"F0.wireOp",EDGE,"E7.58.4"),sQuery(id+"F0.wireOp",EDGE,"E7.58.5"),sQuery(id+"F0.wireOp",EDGE,"E7.59.0"),sQuery(id+"F0.wireOp",EDGE,"E7.59.1"),sQuery(id+"F0.wireOp",EDGE,"E7.59.2"),sQuery(id+"F0.wireOp",EDGE,"E7.59.3"),sQuery(id+"F0.wireOp",EDGE,"E7.59.4"),sQuery(id+"F0.wireOp",EDGE,"E7.59.5"),sQuery(id+"F0.wireOp",EDGE,"E8"),sQuery(id+"F0.wireOp",EDGE,"E9"),sQuery(id+"F0.wireOp",EDGE,"E10"),sQuery(id+"F0.wireOp",EDGE,"E11.filletArc"),sQuery(id+"F0.wireOp",EDGE,"E12.filletArc"),sQuery(id+"F0.wireOp",EDGE,"E13.filletArc"),sQuery(id+"F0.wireOp",EDGE,"E14.MirrorCS"),sQuery(id+"F0.wireOp",EDGE,"E15.MirrorCS"),sQuery(id+"F0.wireOp",EDGE,"E16.MirrorCS"),sQuery(id+"F0.wireOp",EDGE,"E17.MirrorCS"),sQuery(id+"F0.wireOp",EDGE,"E18.MirrorCS"),sQuery(id+"F0.wireOp",EDGE,"E19.MirrorCS"),sQuery(id+"F0.wireOp",EDGE,"E21.MirrorCS"),sQuery(id+"F0.wireOp",EDGE,"E22.MirrorCS"),sQuery(id+"F0.wireOp",EDGE,"E23.MirrorCS"),sQuery(id+"F0.wireOp",EDGE,"E24.MirrorCS"),sQuery(id+"F0.wireOp",EDGE,"E25.MirrorCS"),sQuery(id+"F0.wireOp",EDGE,"E20.MirrorCS"),sQuery(id+"F0.wireOp",EDGE,"E27.MirrorCS"),sQuery(id+"F0.wireOp",EDGE,"E28.MirrorCS"),sQuery(id+"F0.wireOp",EDGE,"E29.MirrorCS"),sQuery(id+"F0.wireOp",EDGE,"E30.MirrorCS"),sQuery(id+"F0.wireOp",EDGE,"E31.MirrorCS"),sQuery(id+"F0.wireOp",EDGE,"E32.MirrorCS"),sQuery(id+"F0.wireOp",EDGE,"E33"),sQuery(id+"F0.wireOp",EDGE,"E34.1.0"),sQuery(id+"F0.wireOp",EDGE,"E34.2.0"),sQuery(id+"F0.wireOp",EDGE,"E34.3.0"),sQuery(id+"F0.wireOp",EDGE,"E34.4.0"),sQuery(id+"F0.wireOp",EDGE,"E34.5.0"),sQuery(id+"F0.wireOp",EDGE,"E34.6.0"),sQuery(id+"F0.wireOp",EDGE,"E34.7.0"),sQuery(id+"F0.wireOp",EDGE,"E34.8.0"),sQuery(id+"F0.wireOp",EDGE,"E34.9.0"),sQuery(id+"F0.wireOp",EDGE,"E34.10.0"),sQuery(id+"F0.wireOp",EDGE,"E34.11.0"),sQuery(id+"F0.wireOp",EDGE,"E34.12.0"),sQuery(id+"F0.wireOp",EDGE,"E34.13.0"),sQuery(id+"F0.wireOp",EDGE,"E34.14.0"),sQuery(id+"F0.wireOp",EDGE,"E34.15.0"),sQuery(id+"F0.wireOp",EDGE,"E34.16.0"),sQuery(id+"F0.wireOp",EDGE,"E34.17.0"),sQuery(id+"F0.wireOp",EDGE,"E34.18.0"),sQuery(id+"F0.wireOp",EDGE,"E34.19.0"),sQuery(id+"F0.wireOp",EDGE,"E34.20.0"),sQuery(id+"F0.wireOp",EDGE,"E34.21.0"),sQuery(id+"F0.wireOp",EDGE,"E34.22.0"),sQuery(id+"F0.wireOp",EDGE,"E34.23.0"),sQuery(id+"F0.wireOp",EDGE,"E34.24.0"),sQuery(id+"F0.wireOp",EDGE,"E34.25.0"),sQuery(id+"F0.wireOp",EDGE,"E34.26.0"),sQuery(id+"F0.wireOp",EDGE,"E34.27.0"),sQuery(id+"F0.wireOp",EDGE,"E34.28.0"),sQuery(id+"F0.wireOp",EDGE,"E34.29.0"),sQuery(id+"F0.wireOp",EDGE,"E34.30.0"),sQuery(id+"F0.wireOp",EDGE,"E34.31.0"),sQuery(id+"F0.wireOp",EDGE,"E34.32.0"),sQuery(id+"F0.wireOp",EDGE,"E34.33.0"),sQuery(id+"F0.wireOp",EDGE,"E34.34.0"),sQuery(id+"F0.wireOp",EDGE,"E34.35.0"),sQuery(id+"F0.wireOp",EDGE,"E34.36.0"),sQuery(id+"F0.wireOp",EDGE,"E34.37.0"),sQuery(id+"F0.wireOp",EDGE,"E34.38.0"),sQuery(id+"F0.wireOp",EDGE,"E34.39.0"),sQuery(id+"F0.wireOp",EDGE,"E34.40.0"),sQuery(id+"F0.wireOp",EDGE,"E34.41.0"),sQuery(id+"F0.wireOp",EDGE,"E34.42.0"),sQuery(id+"F0.wireOp",EDGE,"E34.43.0"),sQuery(id+"F0.wireOp",EDGE,"E34.44.0"),sQuery(id+"F0.wireOp",EDGE,"E34.45.0"),sQuery(id+"F0.wireOp",EDGE,"E34.46.0"),sQuery(id+"F0.wireOp",EDGE,"E34.47.0"),sQuery(id+"F0.wireOp",EDGE,"E34.48.0"),sQuery(id+"F0.wireOp",EDGE,"E34.49.0"),sQuery(id+"F0.wireOp",EDGE,"E34.50.0"),sQuery(id+"F0.wireOp",EDGE,"E34.51.0"),sQuery(id+"F0.wireOp",EDGE,"E34.52.0"),sQuery(id+"F0.wireOp",EDGE,"E34.53.0"),sQuery(id+"F0.wireOp",EDGE,"E34.54.0"),sQuery(id+"F0.wireOp",EDGE,"E34.55.0"),sQuery(id+"F0.wireOp",EDGE,"E34.56.0"),sQuery(id+"F0.wireOp",EDGE,"E34.57.0"),sQuery(id+"F0.wireOp",EDGE,"E34.58.0"),sQuery(id+"F0.wireOp",EDGE,"E34.59.0")])],"isStart":true});
            fillet(context, id + "F5", {"entities" : qUnion([Q0, Q1, Q2]), "radius" : 1.5 * mm, "tangentPropagation" : true, "allowEdgeOverflow" : false});
        }
    });
